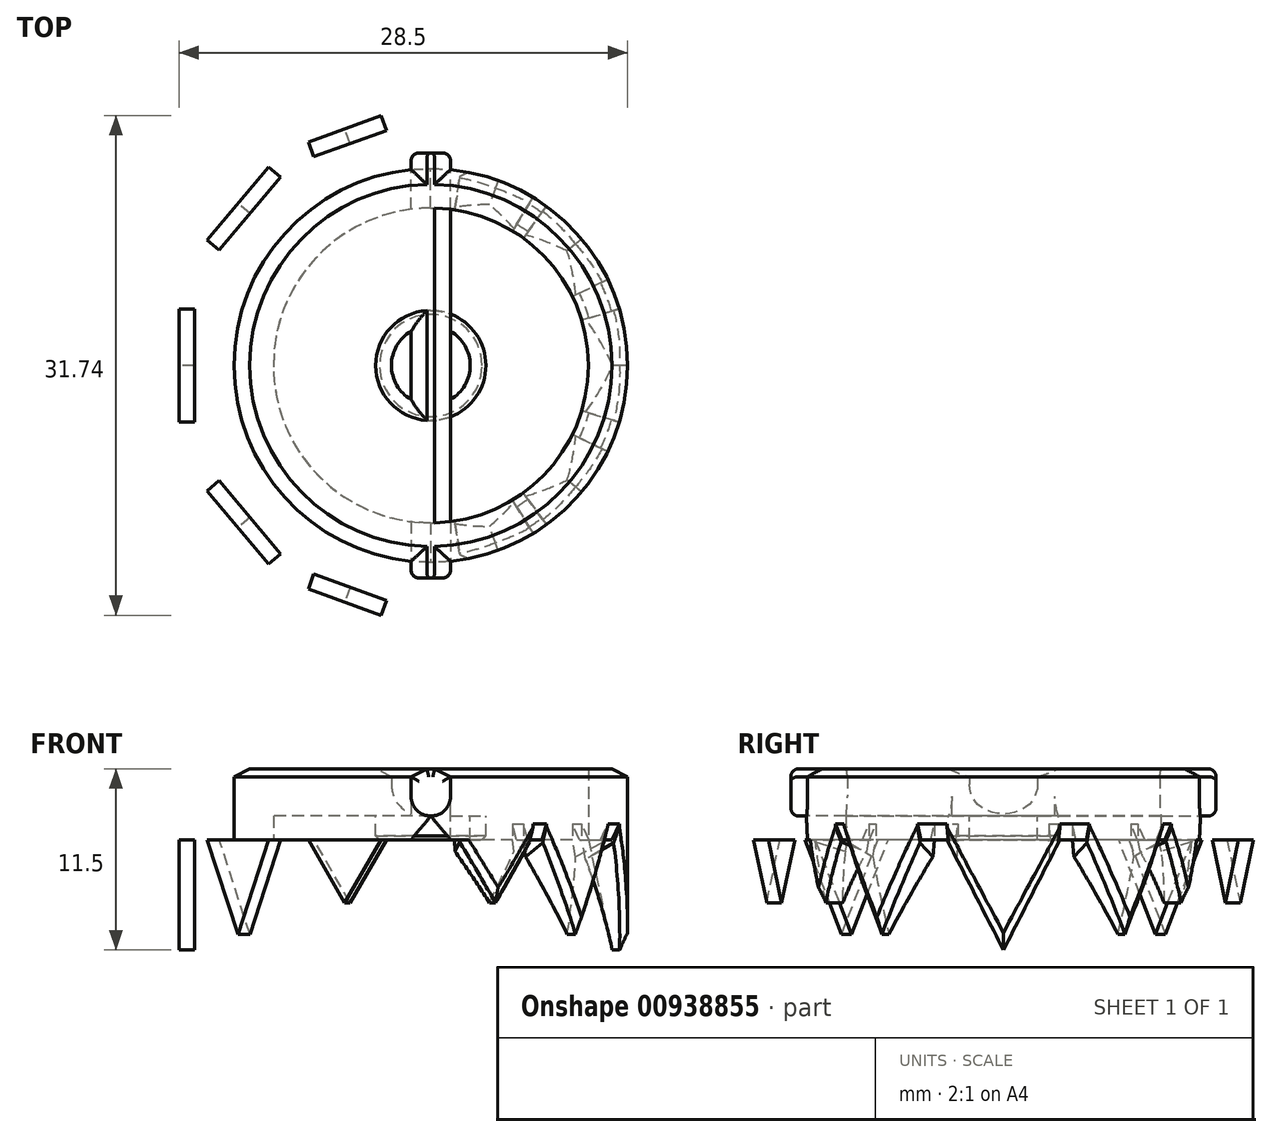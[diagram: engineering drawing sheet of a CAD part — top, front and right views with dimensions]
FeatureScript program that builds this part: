
annotation { "Feature Type Name" : "Feature", "Feature Type Description" : "" }
export const myFeature = defineFeature(function(context is Context, id is Id, definition is map)
    precondition{}
    {
        {
            var Q0;
            Q0=qCreatedBy(makeId("Top.planeOp"),FACE);
            var sketch = newSketch(context, id + "F0", { "sketchPlane" : qUnion([Q0])});
            skCircle(sketch, "E0", {"center": v(0, 0) * mm, "radius": 12.5 * mm});
            skArc(sketch, "E1", {"start": v(-1.25, 9.92) * mm, "mid": v(-10, 0) * mm, "end": v(-1.25, -9.92) * mm});
            skCircle(sketch, "E2", {"center": v(0, 0) * mm, "radius": 3.5 * mm});
            skLineSegment(sketch, "E3", {"start": v(0, 0) * mm, "end": v(1.25, 0) * mm, "construction": true});
            skLineSegment(sketch, "E4", {"start": v(1.25, 3.27) * mm, "end": v(1.25, 9.92) * mm});
            skLineSegment(sketch, "E5", {"start": v(0, 0) * mm, "end": v(-1.25, 0) * mm, "construction": true});
            skLineSegment(sketch, "E6", {"start": v(-1.25, 3.27) * mm, "end": v(-1.25, 9.92) * mm});
            skLineSegment(sketch, "E7", {"start": v(-1.25, -3.27) * mm, "end": v(-1.25, -9.92) * mm});
            skLineSegment(sketch, "E8", {"start": v(1.25, -3.27) * mm, "end": v(1.25, -9.92) * mm});
            skArc(sketch, "E9.trimOffspring", {"start": v(1.25, -9.92) * mm, "mid": v(10, 0) * mm, "end": v(1.25, 9.92) * mm});
            skCircle(sketch, "E10", {"center": v(0, 0) * mm, "radius": 10 * mm});
            skCircle(sketch, "E11", {"center": v(0, 0) * mm, "radius": 2.5 * mm});
            skLineSegment(sketch, "E12", {"start": v(-1.25, -9.92) * mm, "end": v(-1.25, 9.92) * mm});
            skLineSegment(sketch, "E13", {"start": v(1.25, -9.92) * mm, "end": v(1.25, 9.92) * mm});
            skSolve(sketch);
        }
        {
            var Q0;
            Q0 = qSketchRegion(id + "F0", true);
            var Q1;
            {var subQ0=sQuery(id+"F0.wireOp",EDGE,"E4");Q1=makeQuery(id+"F0.imprint","IMPRINT",FACE,{"disambiguationData":[TD([[makeQuery(id+"F0.imprint","IMPRINT",EDGE,{"derivedFrom":subQ0}),1.0]])]});}
            var Q2;
            {var subQ0=sQuery(id+"F0.wireOp",EDGE,"E7");Q2=makeQuery(id+"F0.imprint","IMPRINT",FACE,{"disambiguationData":[TD([[makeQuery(id+"F0.imprint","IMPRINT",EDGE,{"derivedFrom":subQ0}),1.0]])]});}
            var Q3;
            Q3=makeQuery(id+"F0.imprint","IMPRINT",FACE,{"disambiguationData":[TD([[makeQuery(id+"F0.imprint","IMPRINT",EDGE,{"derivedFrom":sQuery(id+"F0.wireOp",EDGE,"E11")}),1.0]])]});
            var Q4;
            {var subQ0=sQuery(id+"F0.wireOp",EDGE,"E12");var subQ1=sQuery(id+"F0.wireOp",EDGE,"E2");var subQ2=makeQuery(id+"F0.imprint","INTERSECT",VERTEX,{"disambiguationData":[OD(1.0)],"derivedFrom":[subQ1,subQ0]});Q4=makeQuery(id+"F0.imprint","IMPRINT",FACE,{"disambiguationData":[TD([[makeQuery(id+"F0.imprint","IMPRINT",EDGE,{"disambiguationData":[TD([[subQ2,-1.0]])],"derivedFrom":subQ1}),-1.0]])]});}
            var Q5;
            {var subQ0=sQuery(id+"F0.wireOp",EDGE,"E12");var subQ1=sQuery(id+"F0.wireOp",EDGE,"E2");var subQ2=makeQuery(id+"F0.imprint","INTERSECT",VERTEX,{"disambiguationData":[OD(1.0)],"derivedFrom":[subQ1,subQ0]});Q5=makeQuery(id+"F0.imprint","IMPRINT",FACE,{"disambiguationData":[TD([[makeQuery(id+"F0.imprint","IMPRINT",EDGE,{"disambiguationData":[TD([[subQ2,-1.0]])],"derivedFrom":subQ1}),1.0]])]});}
            var Q6;
            {var subQ0=sQuery(id+"F0.wireOp",EDGE,"E12");var subQ1=sQuery(id+"F0.wireOp",EDGE,"E11");var subQ2=makeQuery(id+"F0.imprint","INTERSECT",VERTEX,{"disambiguationData":[OD(0.0)],"derivedFrom":[subQ1,subQ0]});Q6=makeQuery(id+"F0.imprint","IMPRINT",FACE,{"disambiguationData":[TD([[makeQuery(id+"F0.imprint","IMPRINT",EDGE,{"disambiguationData":[TD([[subQ2,-1.0]])],"derivedFrom":subQ1}),1.0]])]});}
            var Q7;
            {var subQ0=sQuery(id+"F0.wireOp",EDGE,"E13");var subQ1=sQuery(id+"F0.wireOp",EDGE,"E11");var subQ2=makeQuery(id+"F0.imprint","INTERSECT",VERTEX,{"disambiguationData":[OD(0.0)],"derivedFrom":[subQ1,subQ0]});Q7=makeQuery(id+"F0.imprint","IMPRINT",FACE,{"disambiguationData":[TD([[makeQuery(id+"F0.imprint","IMPRINT",EDGE,{"disambiguationData":[TD([[subQ2,1.0]])],"derivedFrom":subQ1}),1.0]])]});}
            var Q8;
            {var subQ0=sQuery(id+"F0.wireOp",EDGE,"E12");var subQ1=sQuery(id+"F0.wireOp",EDGE,"E2");var subQ2=makeQuery(id+"F0.imprint","INTERSECT",VERTEX,{"disambiguationData":[OD(0.0)],"derivedFrom":[subQ1,subQ0]});Q8=makeQuery(id+"F0.imprint","IMPRINT",FACE,{"disambiguationData":[TD([[makeQuery(id+"F0.imprint","IMPRINT",EDGE,{"disambiguationData":[TD([[subQ2,1.0]])],"derivedFrom":subQ1}),1.0]])]});}
            var Q9;
            {var subQ0=sQuery(id+"F0.wireOp",EDGE,"E12");var subQ1=sQuery(id+"F0.wireOp",EDGE,"E2");var subQ2=makeQuery(id+"F0.imprint","INTERSECT",VERTEX,{"disambiguationData":[OD(0.0)],"derivedFrom":[subQ1,subQ0]});Q9=makeQuery(id+"F0.imprint","IMPRINT",FACE,{"disambiguationData":[TD([[makeQuery(id+"F0.imprint","IMPRINT",EDGE,{"disambiguationData":[TD([[subQ2,1.0]])],"derivedFrom":subQ1}),-1.0]])]});}
            extrude(context, id + "F1", {"entities" : qUnion([Q0, Q1, Q2, Q3, Q4, Q5, Q6, Q7, Q8, Q9]), "depth" : 3 * mm, "offsetDistance" : 25 * mm});
        }
        {
            var Q0;
            Q0=makeQuery(id+"F0.imprint","IMPRINT",FACE,{"disambiguationData":[TD([[makeQuery(id+"F0.imprint","IMPRINT",EDGE,{"derivedFrom":sQuery(id+"F0.wireOp",EDGE,"E0")}),1.0]])]});
            var Q1;
            {var subQ0=sQuery(id+"F0.wireOp",EDGE,"E12");var subQ1=sQuery(id+"F0.wireOp",EDGE,"E2");var subQ2=makeQuery(id+"F0.imprint","INTERSECT",VERTEX,{"disambiguationData":[OD(0.0)],"derivedFrom":[subQ1,subQ0]});Q1=makeQuery(id+"F0.imprint","IMPRINT",FACE,{"disambiguationData":[TD([[makeQuery(id+"F0.imprint","IMPRINT",EDGE,{"disambiguationData":[TD([[subQ2,-1.0]])],"derivedFrom":subQ1}),1.0]])]});}
            var Q2;
            {var subQ0=sQuery(id+"F0.wireOp",EDGE,"E12");var subQ1=sQuery(id+"F0.wireOp",EDGE,"E11");var subQ2=makeQuery(id+"F0.imprint","INTERSECT",VERTEX,{"disambiguationData":[OD(0.0)],"derivedFrom":[subQ1,subQ0]});Q2=makeQuery(id+"F0.imprint","IMPRINT",FACE,{"disambiguationData":[TD([[makeQuery(id+"F0.imprint","IMPRINT",EDGE,{"disambiguationData":[TD([[subQ2,-1.0]])],"derivedFrom":subQ1}),1.0]])]});}
            var Q3;
            {var subQ0=sQuery(id+"F0.wireOp",EDGE,"E12");var subQ1=sQuery(id+"F0.wireOp",EDGE,"E2");var subQ2=makeQuery(id+"F0.imprint","INTERSECT",VERTEX,{"disambiguationData":[OD(1.0)],"derivedFrom":[subQ1,subQ0]});Q3=makeQuery(id+"F0.imprint","IMPRINT",FACE,{"disambiguationData":[TD([[makeQuery(id+"F0.imprint","IMPRINT",EDGE,{"disambiguationData":[TD([[subQ2,-1.0]])],"derivedFrom":subQ1}),1.0]])]});}
            var Q4;
            {var subQ0=sQuery(id+"F0.wireOp",EDGE,"E13");var subQ1=sQuery(id+"F0.wireOp",EDGE,"E2");var subQ2=makeQuery(id+"F0.imprint","INTERSECT",VERTEX,{"disambiguationData":[OD(0.0)],"derivedFrom":[subQ1,subQ0]});Q4=makeQuery(id+"F0.imprint","IMPRINT",FACE,{"disambiguationData":[TD([[makeQuery(id+"F0.imprint","IMPRINT",EDGE,{"disambiguationData":[TD([[subQ2,1.0]])],"derivedFrom":subQ1}),1.0]])]});}
            var Q5;
            {var subQ0=sQuery(id+"F0.wireOp",EDGE,"E13");var subQ1=sQuery(id+"F0.wireOp",EDGE,"E11");var subQ2=makeQuery(id+"F0.imprint","INTERSECT",VERTEX,{"disambiguationData":[OD(0.0)],"derivedFrom":[subQ1,subQ0]});Q5=makeQuery(id+"F0.imprint","IMPRINT",FACE,{"disambiguationData":[TD([[makeQuery(id+"F0.imprint","IMPRINT",EDGE,{"disambiguationData":[TD([[subQ2,1.0]])],"derivedFrom":subQ1}),1.0]])]});}
            var Q6;
            {var subQ0=sQuery(id+"F0.wireOp",EDGE,"E12");var subQ1=sQuery(id+"F0.wireOp",EDGE,"E11");var subQ2=makeQuery(id+"F0.imprint","INTERSECT",VERTEX,{"disambiguationData":[OD(0.0)],"derivedFrom":[subQ1,subQ0]});Q6=makeQuery(id+"F0.imprint","IMPRINT",FACE,{"disambiguationData":[TD([[makeQuery(id+"F0.imprint","IMPRINT",EDGE,{"disambiguationData":[TD([[subQ2,1.0]])],"derivedFrom":subQ1}),1.0]])]});}
            var Q7;
            {var subQ0=sQuery(id+"F0.wireOp",EDGE,"E12");var subQ1=sQuery(id+"F0.wireOp",EDGE,"E2");var subQ2=makeQuery(id+"F0.imprint","INTERSECT",VERTEX,{"disambiguationData":[OD(0.0)],"derivedFrom":[subQ1,subQ0]});Q7=makeQuery(id+"F0.imprint","IMPRINT",FACE,{"disambiguationData":[TD([[makeQuery(id+"F0.imprint","IMPRINT",EDGE,{"disambiguationData":[TD([[subQ2,1.0]])],"derivedFrom":subQ1}),1.0]])]});}
            extrude(context, id + "F2", {"entities" : qUnion([Q0, Q1, Q2, Q3, Q4, Q5, Q6, Q7]), "operationType" : NewBodyOperationType.ADD, "oppositeDirection" : true, "depth" : 1.5 * mm, "offsetDistance" : 25 * mm});
        }
        {
            var Q0;
            Q0=makeQuery(id+"F2.opExtrude","CAP_FACE",FACE,{"disambiguationData":[OSD([sQuery(id+"F0.wireOp",EDGE,"E2")])],"isStart":false});
            var sketch = newSketch(context, id + "F3", { "sketchPlane" : qUnion([Q0])});
            skCircle(sketch, "E14", {"center": v(0, 0) * mm, "radius": 12.5 * mm});
            skLineSegment(sketch, "E15", {"start": v(0, 0) * mm, "end": v(0, 12.5) * mm, "construction": true});
            skLineSegment(sketch, "E16", {"start": v(0, 0) * mm, "end": v(0, -12.5) * mm, "construction": true});
            skLineSegment(sketch, "E17", {"start": v(0, 0) * mm, "end": v(-4.28, 11.75) * mm, "construction": true});
            skLineSegment(sketch, "E18", {"start": v(0, 0) * mm, "end": v(-9.58, 8.03) * mm, "construction": true});
            skLineSegment(sketch, "E19", {"start": v(0, 0) * mm, "end": v(-12.5, 0) * mm, "construction": true});
            skLineSegment(sketch, "E20", {"start": v(0, 0) * mm, "end": v(-9.58, -8.03) * mm, "construction": true});
            skLineSegment(sketch, "E21", {"start": v(0, 0) * mm, "end": v(-4.28, -11.75) * mm, "construction": true});
            skCircle(sketch, "E22", {"center": v(0, 0) * mm, "radius": 10 * mm});
            skLineSegment(sketch, "E23", {"start": v(-3.42, 9.4) * mm, "end": v(-1.54, 10.08) * mm, "construction": true});
            skLineSegment(sketch, "E24", {"start": v(-3.42, 9.4) * mm, "end": v(-5.3, 8.71) * mm, "construction": true});
            skLineSegment(sketch, "E25", {"start": v(-7.66, 6.43) * mm, "end": v(-6.05, 8.34) * mm, "construction": true});
            skLineSegment(sketch, "E26", {"start": v(-7.66, 6.43) * mm, "end": v(-9.27, 4.51) * mm, "construction": true});
            skLineSegment(sketch, "E27", {"start": v(-10, 0) * mm, "end": v(-10, 3) * mm, "construction": true});
            skLineSegment(sketch, "E28", {"start": v(-10, 0) * mm, "end": v(-10, -3) * mm, "construction": true});
            skLineSegment(sketch, "E29", {"start": v(-7.66, -6.43) * mm, "end": v(-9.27, -4.51) * mm, "construction": true});
            skLineSegment(sketch, "E30", {"start": v(-7.66, -6.43) * mm, "end": v(-6.05, -8.34) * mm, "construction": true});
            skLineSegment(sketch, "E31", {"start": v(-3.42, -9.4) * mm, "end": v(-5.3, -8.71) * mm, "construction": true});
            skLineSegment(sketch, "E32", {"start": v(-3.42, -9.4) * mm, "end": v(-1.54, -10.08) * mm, "construction": true});
            skLineSegment(sketch, "E33", {"start": v(-1.51, 9.89) * mm, "end": v(-1.54, 10.08) * mm});
            skLineSegment(sketch, "E34", {"start": v(-1.54, 10.08) * mm, "end": v(-1.89, 12.36) * mm});
            skLineSegment(sketch, "E35", {"start": v(-5.2, 8.54) * mm, "end": v(-5.3, 8.71) * mm});
            skLineSegment(sketch, "E36", {"start": v(-5.3, 8.71) * mm, "end": v(-6.5, 10.68) * mm});
            skLineSegment(sketch, "E37", {"start": v(-5.87, 8.1) * mm, "end": v(-6.05, 8.34) * mm});
            skLineSegment(sketch, "E38", {"start": v(-6.05, 8.34) * mm, "end": v(-7.34, 10.12) * mm});
            skLineSegment(sketch, "E39", {"start": v(-9, 4.38) * mm, "end": v(-9.27, 4.51) * mm});
            skLineSegment(sketch, "E40", {"start": v(-9.27, 4.51) * mm, "end": v(-11.24, 5.47) * mm});
            skLineSegment(sketch, "E41", {"start": v(-9.58, 2.87) * mm, "end": v(-10, 3) * mm});
            skLineSegment(sketch, "E42", {"start": v(-10, 3) * mm, "end": v(-11.97, 3.6) * mm});
            skLineSegment(sketch, "E43", {"start": v(-9.58, -2.87) * mm, "end": v(-10, -3) * mm});
            skLineSegment(sketch, "E44", {"start": v(-10, -3) * mm, "end": v(-11.97, -3.6) * mm});
            skLineSegment(sketch, "E45", {"start": v(-9, -4.38) * mm, "end": v(-9.27, -4.51) * mm});
            skLineSegment(sketch, "E46", {"start": v(-9.27, -4.51) * mm, "end": v(-11.24, -5.47) * mm});
            skLineSegment(sketch, "E47", {"start": v(-5.87, -8.1) * mm, "end": v(-6.05, -8.34) * mm});
            skLineSegment(sketch, "E48", {"start": v(-6.05, -8.34) * mm, "end": v(-7.34, -10.12) * mm});
            skLineSegment(sketch, "E49", {"start": v(-5.2, -8.54) * mm, "end": v(-5.3, -8.71) * mm});
            skLineSegment(sketch, "E50", {"start": v(-5.3, -8.71) * mm, "end": v(-6.5, -10.68) * mm});
            skLineSegment(sketch, "E51", {"start": v(-1.51, -9.89) * mm, "end": v(-1.54, -10.08) * mm});
            skLineSegment(sketch, "E52", {"start": v(-1.54, -10.08) * mm, "end": v(-1.89, -12.36) * mm});
            skLineSegment(sketch, "E53", {"start": v(-1.89, 12.36) * mm, "end": v(-1.51, 9.89) * mm});
            skLineSegment(sketch, "E54", {"start": v(-6.5, 10.68) * mm, "end": v(-5.2, 8.54) * mm});
            skLineSegment(sketch, "E55", {"start": v(-7.34, 10.12) * mm, "end": v(-5.87, 8.1) * mm});
            skLineSegment(sketch, "E56", {"start": v(-11.24, 5.47) * mm, "end": v(-9, 4.38) * mm});
            skLineSegment(sketch, "E57", {"start": v(-11.97, 3.6) * mm, "end": v(-9.58, 2.87) * mm});
            skLineSegment(sketch, "E58", {"start": v(-11.97, -3.6) * mm, "end": v(-9.58, -2.87) * mm});
            skLineSegment(sketch, "E59", {"start": v(-11.24, -5.47) * mm, "end": v(-9, -4.38) * mm});
            skLineSegment(sketch, "E60", {"start": v(-7.34, -10.12) * mm, "end": v(-5.87, -8.1) * mm});
            skLineSegment(sketch, "E61", {"start": v(-6.5, -10.68) * mm, "end": v(-5.2, -8.54) * mm});
            skLineSegment(sketch, "E62", {"start": v(-1.89, -12.36) * mm, "end": v(-1.51, -9.89) * mm});
            skLineSegment(sketch, "E63.trimOffspring", {"start": v(1.51, -9.89) * mm, "end": v(1.89, -12.36) * mm});
            skLineSegment(sketch, "E64.trimOffspring", {"start": v(5.2, -8.54) * mm, "end": v(6.5, -10.68) * mm});
            skLineSegment(sketch, "E65.trimOffspring", {"start": v(5.87, -8.1) * mm, "end": v(7.34, -10.12) * mm});
            skLineSegment(sketch, "E66.trimOffspring", {"start": v(9, -4.38) * mm, "end": v(11.24, -5.47) * mm});
            skLineSegment(sketch, "E67.trimOffspring", {"start": v(9.58, -2.87) * mm, "end": v(11.97, -3.6) * mm});
            skLineSegment(sketch, "E68.trimOffspring", {"start": v(9.58, 2.87) * mm, "end": v(11.97, 3.6) * mm});
            skLineSegment(sketch, "E69.trimOffspring", {"start": v(9, 4.38) * mm, "end": v(11.24, 5.47) * mm});
            skLineSegment(sketch, "E70.trimOffspring", {"start": v(5.87, 8.1) * mm, "end": v(7.34, 10.12) * mm});
            skLineSegment(sketch, "E71.trimOffspring", {"start": v(5.2, 8.54) * mm, "end": v(6.5, 10.68) * mm});
            skLineSegment(sketch, "E72.trimOffspring", {"start": v(1.51, 9.89) * mm, "end": v(1.89, 12.36) * mm});
            skLineSegment(sketch, "E73", {"start": v(-5.3, -8.71) * mm, "end": v(-7, -13.41) * mm, "construction": true});
            skLineSegment(sketch, "E74", {"start": v(-1.54, -10.08) * mm, "end": v(-3.25, -14.78) * mm, "construction": true});
            skLineSegment(sketch, "E75", {"start": v(-3.25, -14.78) * mm, "end": v(-7, -13.41) * mm, "construction": true});
            skLineSegment(sketch, "E76", {"start": v(-7, -13.41) * mm, "end": v(-8.42, -12.9) * mm, "construction": true});
            skLineSegment(sketch, "E77", {"start": v(-3.25, -14.78) * mm, "end": v(-1.84, -15.3) * mm, "construction": true});
            skLineSegment(sketch, "E78", {"start": v(-6.5, -10.68) * mm, "end": v(-7.43, -13.26) * mm, "construction": true});
            skLineSegment(sketch, "E79", {"start": v(-1.89, -12.36) * mm, "end": v(-2.83, -14.93) * mm, "construction": true});
            skLineSegment(sketch, "E80", {"start": v(-7.43, -13.26) * mm, "end": v(-7.78, -14.2) * mm});
            skLineSegment(sketch, "E81", {"start": v(-2.83, -14.93) * mm, "end": v(-3.17, -15.87) * mm});
            skLineSegment(sketch, "E82", {"start": v(-3.17, -15.87) * mm, "end": v(-7.78, -14.2) * mm});
            skLineSegment(sketch, "E83", {"start": v(-7.43, -13.26) * mm, "end": v(-2.83, -14.93) * mm});
            skLineSegment(sketch, "E84", {"start": v(-9.27, -4.51) * mm, "end": v(-13.1, -7.73) * mm, "construction": true});
            skLineSegment(sketch, "E85", {"start": v(-6.05, -8.34) * mm, "end": v(-9.88, -11.56) * mm, "construction": true});
            skLineSegment(sketch, "E86", {"start": v(-9.88, -11.56) * mm, "end": v(-13.1, -7.73) * mm, "construction": true});
            skLineSegment(sketch, "E87", {"start": v(-13.1, -7.73) * mm, "end": v(-14.06, -6.58) * mm, "construction": true});
            skLineSegment(sketch, "E88", {"start": v(-9.88, -11.56) * mm, "end": v(-8.92, -12.7) * mm, "construction": true});
            skLineSegment(sketch, "E89", {"start": v(-11.24, -5.47) * mm, "end": v(-13.44, -7.32) * mm, "construction": true});
            skLineSegment(sketch, "E90", {"start": v(-7.34, -10.12) * mm, "end": v(-9.54, -11.96) * mm, "construction": true});
            skLineSegment(sketch, "E91", {"start": v(-13.44, -7.32) * mm, "end": v(-9.54, -11.96) * mm});
            skLineSegment(sketch, "E92", {"start": v(-9.54, -11.96) * mm, "end": v(-10.3, -12.6) * mm});
            skLineSegment(sketch, "E93", {"start": v(-13.44, -7.32) * mm, "end": v(-14.2, -7.96) * mm});
            skLineSegment(sketch, "E94", {"start": v(-14.2, -7.96) * mm, "end": v(-10.3, -12.6) * mm});
            skLineSegment(sketch, "E95", {"start": v(-10, 3) * mm, "end": v(-15, 3) * mm, "construction": true});
            skLineSegment(sketch, "E96", {"start": v(-10, -3) * mm, "end": v(-15, -3) * mm, "construction": true});
            skLineSegment(sketch, "E97", {"start": v(-15, -3) * mm, "end": v(-15, 3) * mm, "construction": true});
            skLineSegment(sketch, "E98", {"start": v(-15, 3) * mm, "end": v(-15, 4) * mm, "construction": true});
            skLineSegment(sketch, "E99", {"start": v(-15, -3) * mm, "end": v(-15, -4) * mm, "construction": true});
            skLineSegment(sketch, "E100", {"start": v(-11.97, -3.6) * mm, "end": v(-15, -3.6) * mm, "construction": true});
            skLineSegment(sketch, "E101", {"start": v(-11.97, 3.6) * mm, "end": v(-15, 3.6) * mm, "construction": true});
            skLineSegment(sketch, "E102", {"start": v(-15, 3.6) * mm, "end": v(-16, 3.6) * mm});
            skLineSegment(sketch, "E103", {"start": v(-15, -3.6) * mm, "end": v(-16, -3.6) * mm});
            skLineSegment(sketch, "E104", {"start": v(-16, -3.6) * mm, "end": v(-16, 3.6) * mm});
            skLineSegment(sketch, "E105", {"start": v(-15, 3.6) * mm, "end": v(-15, -3.6) * mm});
            skLineSegment(sketch, "E106", {"start": v(-6.05, 8.34) * mm, "end": v(-9.88, 11.56) * mm, "construction": true});
            skLineSegment(sketch, "E107", {"start": v(-9.27, 4.51) * mm, "end": v(-13.1, 7.73) * mm, "construction": true});
            skLineSegment(sketch, "E108", {"start": v(-13.1, 7.73) * mm, "end": v(-9.88, 11.56) * mm, "construction": true});
            skLineSegment(sketch, "E109", {"start": v(-9.88, 11.56) * mm, "end": v(-9.24, 12.32) * mm, "construction": true});
            skLineSegment(sketch, "E110", {"start": v(-13.1, 7.73) * mm, "end": v(-13.74, 6.96) * mm, "construction": true});
            skLineSegment(sketch, "E111", {"start": v(-7.34, 10.12) * mm, "end": v(-9.54, 11.96) * mm, "construction": true});
            skLineSegment(sketch, "E112", {"start": v(-11.24, 5.47) * mm, "end": v(-13.44, 7.32) * mm, "construction": true});
            skLineSegment(sketch, "E113", {"start": v(-13.44, 7.32) * mm, "end": v(-14.2, 7.96) * mm});
            skLineSegment(sketch, "E114", {"start": v(-9.54, 11.96) * mm, "end": v(-10.3, 12.6) * mm});
            skLineSegment(sketch, "E115", {"start": v(-10.3, 12.6) * mm, "end": v(-14.2, 7.96) * mm});
            skLineSegment(sketch, "E116", {"start": v(-13.44, 7.32) * mm, "end": v(-9.54, 11.96) * mm});
            skLineSegment(sketch, "E117", {"start": v(-5.3, 8.71) * mm, "end": v(-7, 13.41) * mm, "construction": true});
            skLineSegment(sketch, "E118", {"start": v(-1.54, 10.08) * mm, "end": v(-3.25, 14.78) * mm, "construction": true});
            skLineSegment(sketch, "E119", {"start": v(-3.25, 14.78) * mm, "end": v(-7, 13.41) * mm, "construction": true});
            skLineSegment(sketch, "E120", {"start": v(-7, 13.41) * mm, "end": v(-7.95, 13.07) * mm, "construction": true});
            skLineSegment(sketch, "E121", {"start": v(-3.25, 14.78) * mm, "end": v(-2.31, 15.12) * mm, "construction": true});
            skLineSegment(sketch, "E122", {"start": v(-1.89, 12.36) * mm, "end": v(-2.83, 14.93) * mm, "construction": true});
            skLineSegment(sketch, "E123", {"start": v(-6.5, 10.68) * mm, "end": v(-7.43, 13.26) * mm, "construction": true});
            skLineSegment(sketch, "E124", {"start": v(-7.43, 13.26) * mm, "end": v(-7.78, 14.2) * mm});
            skLineSegment(sketch, "E125", {"start": v(-2.83, 14.93) * mm, "end": v(-3.17, 15.87) * mm});
            skLineSegment(sketch, "E126", {"start": v(-3.17, 15.87) * mm, "end": v(-7.78, 14.2) * mm});
            skLineSegment(sketch, "E127", {"start": v(-7.43, 13.26) * mm, "end": v(-2.83, 14.93) * mm});
            skSolve(sketch);
        }
        {
            var Q0;
            {var subQ0=sQuery(id+"F3.wireOp",EDGE,"E53");Q0=makeQuery(id+"F3.imprint","IMPRINT",FACE,{"disambiguationData":[TD([[makeQuery(id+"F3.imprint","IMPRINT",EDGE,{"derivedFrom":subQ0}),-1.0]])]});}
            var Q1;
            {var subQ0=sQuery(id+"F3.wireOp",EDGE,"E71.trimOffspring");Q1=makeQuery(id+"F3.imprint","IMPRINT",FACE,{"disambiguationData":[TD([[makeQuery(id+"F3.imprint","IMPRINT",EDGE,{"derivedFrom":subQ0}),1.0]])]});}
            var Q2;
            {var subQ0=sQuery(id+"F3.wireOp",EDGE,"E63.trimOffspring");Q2=makeQuery(id+"F3.imprint","IMPRINT",FACE,{"disambiguationData":[TD([[makeQuery(id+"F3.imprint","IMPRINT",EDGE,{"derivedFrom":subQ0}),1.0]])]});}
            var Q3;
            {var subQ0=sQuery(id+"F3.wireOp",EDGE,"E61");Q3=makeQuery(id+"F3.imprint","IMPRINT",FACE,{"disambiguationData":[TD([[makeQuery(id+"F3.imprint","IMPRINT",EDGE,{"derivedFrom":subQ0}),-1.0]])]});}
            extrude(context, id + "F4", {"entities" : qUnion([Q0, Q1, Q2, Q3]), "operationType" : NewBodyOperationType.ADD, "depth" : 4 * mm, "offsetDistance" : 25 * mm});
        }
        {
            var Q0;
            {var subQ0=sQuery(id+"F3.wireOp",EDGE,"E55");Q0=makeQuery(id+"F3.imprint","IMPRINT",FACE,{"disambiguationData":[TD([[makeQuery(id+"F3.imprint","IMPRINT",EDGE,{"derivedFrom":subQ0}),-1.0]])]});}
            var Q1;
            {var subQ0=sQuery(id+"F3.wireOp",EDGE,"E69.trimOffspring");Q1=makeQuery(id+"F3.imprint","IMPRINT",FACE,{"disambiguationData":[TD([[makeQuery(id+"F3.imprint","IMPRINT",EDGE,{"derivedFrom":subQ0}),1.0]])]});}
            var Q2;
            {var subQ0=sQuery(id+"F3.wireOp",EDGE,"E65.trimOffspring");Q2=makeQuery(id+"F3.imprint","IMPRINT",FACE,{"disambiguationData":[TD([[makeQuery(id+"F3.imprint","IMPRINT",EDGE,{"derivedFrom":subQ0}),1.0]])]});}
            var Q3;
            {var subQ0=sQuery(id+"F3.wireOp",EDGE,"E59");Q3=makeQuery(id+"F3.imprint","IMPRINT",FACE,{"disambiguationData":[TD([[makeQuery(id+"F3.imprint","IMPRINT",EDGE,{"derivedFrom":subQ0}),-1.0]])]});}
            extrude(context, id + "F5", {"entities" : qUnion([Q0, Q1, Q2, Q3]), "operationType" : NewBodyOperationType.ADD, "depth" : 6 * mm, "offsetDistance" : 25 * mm});
        }
        {
            var Q0;
            {var subQ0=sQuery(id+"F3.wireOp",EDGE,"E57");Q0=makeQuery(id+"F3.imprint","IMPRINT",FACE,{"disambiguationData":[TD([[makeQuery(id+"F3.imprint","IMPRINT",EDGE,{"derivedFrom":subQ0}),-1.0]])]});}
            var Q1;
            {var subQ0=sQuery(id+"F3.wireOp",EDGE,"E67.trimOffspring");Q1=makeQuery(id+"F3.imprint","IMPRINT",FACE,{"disambiguationData":[TD([[makeQuery(id+"F3.imprint","IMPRINT",EDGE,{"derivedFrom":subQ0}),1.0]])]});}
            extrude(context, id + "F6", {"entities" : qUnion([Q0, Q1]), "operationType" : NewBodyOperationType.ADD, "depth" : 7 * mm, "offsetDistance" : 25 * mm});
        }
        {
            var Q0;
            Q0=makeQuery(id+"F3.imprint","IMPRINT",FACE,{"disambiguationData":[TD([[makeQuery(id+"F3.imprint","IMPRINT",EDGE,{"derivedFrom":sQuery(id+"F3.wireOp",EDGE,"E80")}),1.0]])]});
            extrude(context, id + "F7", {"entities" : qUnion([Q0]), "depth" : 4 * mm, "offsetDistance" : 25 * mm});
        }
        {
            var Q0;
            Q0=makeQuery(id+"F7.opExtrude","SWEPT_FACE",FACE,{"disambiguationData":[OSD([sQuery(id+"F3.wireOp",EDGE,"E82")])]});
            var sketch = newSketch(context, id + "F8", { "sketchPlane" : qUnion([Q0])});
            skLineSegment(sketch, "E128", {"start": v(2.45, -1.5) * mm, "end": v(0, -5.5) * mm});
            skLineSegment(sketch, "E129", {"start": v(0, -5.5) * mm, "end": v(-2.45, -1.5) * mm});
            skSolve(sketch);
        }
        {
            var Q0;
            {var subQ0=sQuery(id+"F8.wireOp",EDGE,"E128");Q0=makeQuery(id+"F8.imprint","IMPRINT",FACE,{"disambiguationData":[TD([[makeQuery(id+"F8.imprint","IMPRINT",EDGE,{"derivedFrom":subQ0}),1.0]])]});}
            var Q1;
            {var subQ0=sQuery(id+"F8.wireOp",EDGE,"E129");Q1=makeQuery(id+"F8.imprint","IMPRINT",FACE,{"disambiguationData":[TD([[makeQuery(id+"F8.imprint","IMPRINT",EDGE,{"derivedFrom":subQ0}),1.0]])]});}
            extrude(context, id + "F9", {"entities" : qUnion([Q0, Q1]), "operationType" : NewBodyOperationType.REMOVE, "oppositeDirection" : true, "depth" : 40 * mm, "offsetDistance" : 25 * mm});
        }
        {
            var Q0;
            Q0=makeQuery(id+"F3.imprint","IMPRINT",FACE,{"disambiguationData":[TD([[makeQuery(id+"F3.imprint","IMPRINT",EDGE,{"derivedFrom":sQuery(id+"F3.wireOp",EDGE,"E91")}),-1.0]])]});
            extrude(context, id + "F10", {"entities" : qUnion([Q0]), "depth" : 6 * mm, "offsetDistance" : 25 * mm});
        }
        {
            var Q0;
            Q0=makeQuery(id+"F10.opExtrude","SWEPT_FACE",FACE,{"disambiguationData":[OSD([sQuery(id+"F3.wireOp",EDGE,"E94")])]});
            var sketch = newSketch(context, id + "F11", { "sketchPlane" : qUnion([Q0])});
            skLineSegment(sketch, "E130", {"start": v(3.03, -1.5) * mm, "end": v(0, -7.5) * mm});
            skLineSegment(sketch, "E131", {"start": v(0, -7.5) * mm, "end": v(-3.03, -1.5) * mm});
            skSolve(sketch);
        }
        {
            var Q0;
            {var subQ0=sQuery(id+"F11.wireOp",EDGE,"E130");Q0=makeQuery(id+"F11.imprint","IMPRINT",FACE,{"disambiguationData":[TD([[makeQuery(id+"F11.imprint","IMPRINT",EDGE,{"derivedFrom":subQ0}),1.0]])]});}
            var Q1;
            {var subQ0=sQuery(id+"F11.wireOp",EDGE,"E131");Q1=makeQuery(id+"F11.imprint","IMPRINT",FACE,{"disambiguationData":[TD([[makeQuery(id+"F11.imprint","IMPRINT",EDGE,{"derivedFrom":subQ0}),1.0]])]});}
            extrude(context, id + "F12", {"entities" : qUnion([Q0, Q1]), "operationType" : NewBodyOperationType.REMOVE, "oppositeDirection" : true, "depth" : 40 * mm, "offsetDistance" : 25 * mm});
        }
        {
            var Q0;
            Q0=makeQuery(id+"F3.imprint","IMPRINT",FACE,{"disambiguationData":[TD([[makeQuery(id+"F3.imprint","IMPRINT",EDGE,{"derivedFrom":sQuery(id+"F3.wireOp",EDGE,"E102")}),1.0]])]});
            extrude(context, id + "F13", {"entities" : qUnion([Q0]), "depth" : 7 * mm, "offsetDistance" : 25 * mm});
        }
        {
            var Q0;
            Q0=makeQuery(id+"F13.opExtrude","SWEPT_FACE",FACE,{"disambiguationData":[OSD([sQuery(id+"F3.wireOp",EDGE,"E104")])]});
            var sketch = newSketch(context, id + "F14", { "sketchPlane" : qUnion([Q0])});
            skLineSegment(sketch, "E132", {"start": v(3.6, -1.5) * mm, "end": v(0, -8.5) * mm});
            skLineSegment(sketch, "E133", {"start": v(0, -8.5) * mm, "end": v(-3.6, -1.5) * mm});
            skSolve(sketch);
        }
        {
            var Q0;
            {var subQ0=sQuery(id+"F14.wireOp",EDGE,"E132");Q0=makeQuery(id+"F14.imprint","IMPRINT",FACE,{"disambiguationData":[TD([[makeQuery(id+"F14.imprint","IMPRINT",EDGE,{"derivedFrom":subQ0}),1.0]])]});}
            var Q1;
            {var subQ0=sQuery(id+"F14.wireOp",EDGE,"E133");Q1=makeQuery(id+"F14.imprint","IMPRINT",FACE,{"disambiguationData":[TD([[makeQuery(id+"F14.imprint","IMPRINT",EDGE,{"derivedFrom":subQ0}),1.0]])]});}
            extrude(context, id + "F15", {"entities" : qUnion([Q0, Q1]), "operationType" : NewBodyOperationType.REMOVE, "oppositeDirection" : true, "depth" : 40 * mm, "offsetDistance" : 25 * mm});
        }
        {
            var Q0;
            Q0=makeQuery(id+"F3.imprint","IMPRINT",FACE,{"disambiguationData":[TD([[makeQuery(id+"F3.imprint","IMPRINT",EDGE,{"derivedFrom":sQuery(id+"F3.wireOp",EDGE,"E113")}),-1.0]])]});
            extrude(context, id + "F16", {"entities" : qUnion([Q0]), "depth" : 6 * mm, "offsetDistance" : 25 * mm});
        }
        {
            var Q0;
            Q0=makeQuery(id+"F3.imprint","IMPRINT",FACE,{"disambiguationData":[TD([[makeQuery(id+"F3.imprint","IMPRINT",EDGE,{"derivedFrom":sQuery(id+"F3.wireOp",EDGE,"E124")}),-1.0]])]});
            extrude(context, id + "F17", {"entities" : qUnion([Q0]), "depth" : 4 * mm, "offsetDistance" : 25 * mm});
        }
        {
            var Q0;
            Q0=makeQuery(id+"F16.opExtrude","SWEPT_FACE",FACE,{"disambiguationData":[OSD([sQuery(id+"F3.wireOp",EDGE,"E115")])]});
            var sketch = newSketch(context, id + "F18", { "sketchPlane" : qUnion([Q0])});
            skLineSegment(sketch, "E134", {"start": v(3.03, -1.5) * mm, "end": v(0, -7.5) * mm});
            skLineSegment(sketch, "E135", {"start": v(0, -7.5) * mm, "end": v(-3.03, -1.5) * mm});
            skSolve(sketch);
        }
        {
            var Q0;
            Q0=makeQuery(id+"F17.opExtrude","SWEPT_FACE",FACE,{"disambiguationData":[OSD([sQuery(id+"F3.wireOp",EDGE,"E126")])]});
            var sketch = newSketch(context, id + "F19", { "sketchPlane" : qUnion([Q0])});
            skLineSegment(sketch, "E136", {"start": v(2.45, -1.5) * mm, "end": v(0, -5.5) * mm});
            skLineSegment(sketch, "E137", {"start": v(0, -5.5) * mm, "end": v(-2.45, -1.5) * mm});
            skSolve(sketch);
        }
        {
            var Q0;
            {var subQ0=sQuery(id+"F18.wireOp",EDGE,"E134");Q0=makeQuery(id+"F18.imprint","IMPRINT",FACE,{"disambiguationData":[TD([[makeQuery(id+"F18.imprint","IMPRINT",EDGE,{"derivedFrom":subQ0}),1.0]])]});}
            var Q1;
            {var subQ0=sQuery(id+"F18.wireOp",EDGE,"E135");Q1=makeQuery(id+"F18.imprint","IMPRINT",FACE,{"disambiguationData":[TD([[makeQuery(id+"F18.imprint","IMPRINT",EDGE,{"derivedFrom":subQ0}),1.0]])]});}
            extrude(context, id + "F20", {"entities" : qUnion([Q0, Q1]), "operationType" : NewBodyOperationType.REMOVE, "oppositeDirection" : true, "depth" : 40 * mm, "offsetDistance" : 25 * mm});
        }
        {
            var Q0;
            {var subQ0=sQuery(id+"F19.wireOp",EDGE,"E136");Q0=makeQuery(id+"F19.imprint","IMPRINT",FACE,{"disambiguationData":[TD([[makeQuery(id+"F19.imprint","IMPRINT",EDGE,{"derivedFrom":subQ0}),1.0]])]});}
            var Q1;
            {var subQ0=sQuery(id+"F19.wireOp",EDGE,"E137");Q1=makeQuery(id+"F19.imprint","IMPRINT",FACE,{"disambiguationData":[TD([[makeQuery(id+"F19.imprint","IMPRINT",EDGE,{"derivedFrom":subQ0}),1.0]])]});}
            extrude(context, id + "F21", {"entities" : qUnion([Q0, Q1]), "operationType" : NewBodyOperationType.REMOVE, "oppositeDirection" : true, "depth" : 40 * mm, "offsetDistance" : 25 * mm});
        }
        {
            var Q0;
            Q0=qCreatedBy(makeId("Front.planeOp"),FACE);
            var sketch = newSketch(context, id + "F22", { "sketchPlane" : qUnion([Q0])});
            skLineSegment(sketch, "E138", {"start": v(0, 0) * mm, "end": v(-10, 0) * mm});
            skLineSegment(sketch, "E139", {"start": v(-11.3, -8.62) * mm, "end": v(-9.25, -8.62) * mm});
            skLineSegment(sketch, "E140", {"start": v(0, 0) * mm, "end": v(0, -14.5) * mm});
            skLineSegment(sketch, "E141", {"start": v(-10, 0) * mm, "end": v(-10, -1.5) * mm});
            skLineSegment(sketch, "E142", {"start": v(-9.25, -8.62) * mm, "end": v(-10, -1.5) * mm});
            skLineSegment(sketch, "E143", {"start": v(-11.3, -8.62) * mm, "end": v(-11.55, -8.62) * mm});
            skLineSegment(sketch, "E144", {"start": v(-11.55, -8.62) * mm, "end": v(-10, -1.5) * mm});
            skSolve(sketch);
        }
        {
            var Q0;
            Q0=makeQuery(id+"F22.imprint","IMPRINT",FACE,{"disambiguationData":[TD([[makeQuery(id+"F22.imprint","IMPRINT",EDGE,{"derivedFrom":sQuery(id+"F22.wireOp",EDGE,"E139")}),1.0]])]});
            var Q1;
            Q1=sQuery(id+"F22.wireOp",EDGE,"E140");
            revolve(context, id + "F23", {"operationType" : NewBodyOperationType.REMOVE, "surfaceOperationType" : NewSurfaceOperationType.NEW, "entities" : qUnion([Q0]), "axis" : qUnion([Q1]), "revolveType" : RevolveType.FULL, "oppositeDirection" : true});
        }
        {
            var Q0;
            {var subQ0=sQuery(id+"F0.wireOp",EDGE,"E12");var subQ1=sQuery(id+"F0.wireOp",EDGE,"E11");Q0=makeQuery(id+"F1.opExtrude","CAP_EDGE",EDGE,{"disambiguationData":[OSD([subQ1]),TDD([makeQuery(id+"F0.imprint","IMPRINT",EDGE,{"disambiguationData":[TD([[makeQuery(id+"F0.imprint","INTERSECT",VERTEX,{"disambiguationData":[OD(0.0)],"derivedFrom":[subQ1,subQ0]}),-1.0]])],"derivedFrom":subQ1})])],"isStart":true});}
            var Q1;
            {var subQ0=sQuery(id+"F0.wireOp",EDGE,"E13");var subQ1=sQuery(id+"F0.wireOp",EDGE,"E11");Q1=makeQuery(id+"F1.opExtrude","CAP_EDGE",EDGE,{"disambiguationData":[OSD([subQ1]),TDD([makeQuery(id+"F0.imprint","IMPRINT",EDGE,{"disambiguationData":[TD([[makeQuery(id+"F0.imprint","INTERSECT",VERTEX,{"disambiguationData":[OD(0.0)],"derivedFrom":[subQ1,subQ0]}),1.0]])],"derivedFrom":subQ1})])],"isStart":true});}
            fillet(context, id + "F24", {"entities" : qUnion([Q0, Q1]), "radius" : 2 * mm, "tangentPropagation" : true, "allowEdgeOverflow" : false});
        }
        {
            var Q0;
            {var subQ0=sQuery(id+"F3.wireOp",EDGE,"E14");var subQ1=sQuery(id+"F0.wireOp",EDGE,"E0");Q0=makeQuery(id+"F15.boolean.opBoolean","INTERSECT",EDGE,{"disambiguationData":[OD(1.0)],"derivedFrom":[makeQuery(id+"F6.boolean.opBoolean","MERGE",FACE,{"derivedFrom":[makeQuery(id+"F5.boolean.opBoolean","MERGE",FACE,{"derivedFrom":[makeQuery(id+"F4.boolean.opBoolean","MERGE",FACE,{"derivedFrom":[makeQuery(id+"F2.boolean.opBoolean","MERGE",FACE,{"derivedFrom":[makeQuery(id+"F1.opExtrude","SWEPT_FACE",FACE,{"disambiguationData":[OSD([subQ1])]}),makeQuery(id+"F2.opExtrude","SWEPT_FACE",FACE,{"disambiguationData":[OSD([subQ1])]})]}),makeQuery(id+"F4.opExtrude","SWEPT_FACE",FACE,{"disambiguationData":[OSD([subQ0]),TDD([makeQuery(id+"F3.imprint","IMPRINT",EDGE,{"disambiguationData":[TD([[makeQuery(id+"F3.imprint","INTERSECT",VERTEX,{"derivedFrom":[subQ0,sQuery(id+"F3.wireOp",EDGE,"E71.trimOffspring")]}),-1.0]])],"derivedFrom":subQ0})])]}),makeQuery(id+"F4.opExtrude","SWEPT_FACE",FACE,{"disambiguationData":[OSD([subQ0]),TDD([makeQuery(id+"F3.imprint","IMPRINT",EDGE,{"disambiguationData":[TD([[makeQuery(id+"F3.imprint","INTERSECT",VERTEX,{"derivedFrom":[subQ0,sQuery(id+"F3.wireOp",EDGE,"E53")]}),-1.0]])],"derivedFrom":subQ0})])]}),makeQuery(id+"F4.opExtrude","SWEPT_FACE",FACE,{"disambiguationData":[OSD([subQ0]),TDD([makeQuery(id+"F3.imprint","IMPRINT",EDGE,{"disambiguationData":[TD([[makeQuery(id+"F3.imprint","INTERSECT",VERTEX,{"derivedFrom":[subQ0,sQuery(id+"F3.wireOp",EDGE,"E61")]}),-1.0]])],"derivedFrom":subQ0})])]}),makeQuery(id+"F4.opExtrude","SWEPT_FACE",FACE,{"disambiguationData":[OSD([subQ0]),TDD([makeQuery(id+"F3.imprint","IMPRINT",EDGE,{"disambiguationData":[TD([[makeQuery(id+"F3.imprint","INTERSECT",VERTEX,{"derivedFrom":[subQ0,sQuery(id+"F3.wireOp",EDGE,"E63.trimOffspring")]}),-1.0]])],"derivedFrom":subQ0})])]})]}),makeQuery(id+"F5.opExtrude","SWEPT_FACE",FACE,{"disambiguationData":[OSD([subQ0]),TDD([makeQuery(id+"F3.imprint","IMPRINT",EDGE,{"disambiguationData":[TD([[makeQuery(id+"F3.imprint","INTERSECT",VERTEX,{"derivedFrom":[subQ0,sQuery(id+"F3.wireOp",EDGE,"E69.trimOffspring")]}),-1.0]])],"derivedFrom":subQ0})])]}),makeQuery(id+"F5.opExtrude","SWEPT_FACE",FACE,{"disambiguationData":[OSD([subQ0]),TDD([makeQuery(id+"F3.imprint","IMPRINT",EDGE,{"disambiguationData":[TD([[makeQuery(id+"F3.imprint","INTERSECT",VERTEX,{"derivedFrom":[subQ0,sQuery(id+"F3.wireOp",EDGE,"E55")]}),-1.0]])],"derivedFrom":subQ0})])]}),makeQuery(id+"F5.opExtrude","SWEPT_FACE",FACE,{"disambiguationData":[OSD([subQ0]),TDD([makeQuery(id+"F3.imprint","IMPRINT",EDGE,{"disambiguationData":[TD([[makeQuery(id+"F3.imprint","INTERSECT",VERTEX,{"derivedFrom":[subQ0,sQuery(id+"F3.wireOp",EDGE,"E59")]}),-1.0]])],"derivedFrom":subQ0})])]}),makeQuery(id+"F5.opExtrude","SWEPT_FACE",FACE,{"disambiguationData":[OSD([subQ0]),TDD([makeQuery(id+"F3.imprint","IMPRINT",EDGE,{"disambiguationData":[TD([[makeQuery(id+"F3.imprint","INTERSECT",VERTEX,{"derivedFrom":[subQ0,sQuery(id+"F3.wireOp",EDGE,"E65.trimOffspring")]}),-1.0]])],"derivedFrom":subQ0})])]})]}),makeQuery(id+"F6.opExtrude","SWEPT_FACE",FACE,{"disambiguationData":[OSD([subQ0]),TDD([makeQuery(id+"F3.imprint","IMPRINT",EDGE,{"disambiguationData":[TD([[makeQuery(id+"F3.imprint","INTERSECT",VERTEX,{"derivedFrom":[subQ0,sQuery(id+"F3.wireOp",EDGE,"E57")]}),-1.0]])],"derivedFrom":subQ0})])]}),makeQuery(id+"F6.opExtrude","SWEPT_FACE",FACE,{"disambiguationData":[OSD([subQ0]),TDD([makeQuery(id+"F3.imprint","IMPRINT",EDGE,{"disambiguationData":[TD([[makeQuery(id+"F3.imprint","INTERSECT",VERTEX,{"derivedFrom":[subQ0,sQuery(id+"F3.wireOp",EDGE,"E67.trimOffspring")]}),-1.0]])],"derivedFrom":subQ0})])]})]}),makeQuery(id+"F15.opExtrude","SWEPT_FACE",FACE,{"disambiguationData":[OSD([sQuery(id+"F14.wireOp",EDGE,"E133")])]})]});}
            var Q1;
            {var subQ0=sQuery(id+"F3.wireOp",EDGE,"E14");var subQ1=sQuery(id+"F0.wireOp",EDGE,"E0");Q1=makeQuery(id+"F15.boolean.opBoolean","INTERSECT",EDGE,{"disambiguationData":[OD(1.0)],"derivedFrom":[makeQuery(id+"F6.boolean.opBoolean","MERGE",FACE,{"derivedFrom":[makeQuery(id+"F5.boolean.opBoolean","MERGE",FACE,{"derivedFrom":[makeQuery(id+"F4.boolean.opBoolean","MERGE",FACE,{"derivedFrom":[makeQuery(id+"F2.boolean.opBoolean","MERGE",FACE,{"derivedFrom":[makeQuery(id+"F1.opExtrude","SWEPT_FACE",FACE,{"disambiguationData":[OSD([subQ1])]}),makeQuery(id+"F2.opExtrude","SWEPT_FACE",FACE,{"disambiguationData":[OSD([subQ1])]})]}),makeQuery(id+"F4.opExtrude","SWEPT_FACE",FACE,{"disambiguationData":[OSD([subQ0]),TDD([makeQuery(id+"F3.imprint","IMPRINT",EDGE,{"disambiguationData":[TD([[makeQuery(id+"F3.imprint","INTERSECT",VERTEX,{"derivedFrom":[subQ0,sQuery(id+"F3.wireOp",EDGE,"E71.trimOffspring")]}),-1.0]])],"derivedFrom":subQ0})])]}),makeQuery(id+"F4.opExtrude","SWEPT_FACE",FACE,{"disambiguationData":[OSD([subQ0]),TDD([makeQuery(id+"F3.imprint","IMPRINT",EDGE,{"disambiguationData":[TD([[makeQuery(id+"F3.imprint","INTERSECT",VERTEX,{"derivedFrom":[subQ0,sQuery(id+"F3.wireOp",EDGE,"E53")]}),-1.0]])],"derivedFrom":subQ0})])]}),makeQuery(id+"F4.opExtrude","SWEPT_FACE",FACE,{"disambiguationData":[OSD([subQ0]),TDD([makeQuery(id+"F3.imprint","IMPRINT",EDGE,{"disambiguationData":[TD([[makeQuery(id+"F3.imprint","INTERSECT",VERTEX,{"derivedFrom":[subQ0,sQuery(id+"F3.wireOp",EDGE,"E61")]}),-1.0]])],"derivedFrom":subQ0})])]}),makeQuery(id+"F4.opExtrude","SWEPT_FACE",FACE,{"disambiguationData":[OSD([subQ0]),TDD([makeQuery(id+"F3.imprint","IMPRINT",EDGE,{"disambiguationData":[TD([[makeQuery(id+"F3.imprint","INTERSECT",VERTEX,{"derivedFrom":[subQ0,sQuery(id+"F3.wireOp",EDGE,"E63.trimOffspring")]}),-1.0]])],"derivedFrom":subQ0})])]})]}),makeQuery(id+"F5.opExtrude","SWEPT_FACE",FACE,{"disambiguationData":[OSD([subQ0]),TDD([makeQuery(id+"F3.imprint","IMPRINT",EDGE,{"disambiguationData":[TD([[makeQuery(id+"F3.imprint","INTERSECT",VERTEX,{"derivedFrom":[subQ0,sQuery(id+"F3.wireOp",EDGE,"E69.trimOffspring")]}),-1.0]])],"derivedFrom":subQ0})])]}),makeQuery(id+"F5.opExtrude","SWEPT_FACE",FACE,{"disambiguationData":[OSD([subQ0]),TDD([makeQuery(id+"F3.imprint","IMPRINT",EDGE,{"disambiguationData":[TD([[makeQuery(id+"F3.imprint","INTERSECT",VERTEX,{"derivedFrom":[subQ0,sQuery(id+"F3.wireOp",EDGE,"E55")]}),-1.0]])],"derivedFrom":subQ0})])]}),makeQuery(id+"F5.opExtrude","SWEPT_FACE",FACE,{"disambiguationData":[OSD([subQ0]),TDD([makeQuery(id+"F3.imprint","IMPRINT",EDGE,{"disambiguationData":[TD([[makeQuery(id+"F3.imprint","INTERSECT",VERTEX,{"derivedFrom":[subQ0,sQuery(id+"F3.wireOp",EDGE,"E59")]}),-1.0]])],"derivedFrom":subQ0})])]}),makeQuery(id+"F5.opExtrude","SWEPT_FACE",FACE,{"disambiguationData":[OSD([subQ0]),TDD([makeQuery(id+"F3.imprint","IMPRINT",EDGE,{"disambiguationData":[TD([[makeQuery(id+"F3.imprint","INTERSECT",VERTEX,{"derivedFrom":[subQ0,sQuery(id+"F3.wireOp",EDGE,"E65.trimOffspring")]}),-1.0]])],"derivedFrom":subQ0})])]})]}),makeQuery(id+"F6.opExtrude","SWEPT_FACE",FACE,{"disambiguationData":[OSD([subQ0]),TDD([makeQuery(id+"F3.imprint","IMPRINT",EDGE,{"disambiguationData":[TD([[makeQuery(id+"F3.imprint","INTERSECT",VERTEX,{"derivedFrom":[subQ0,sQuery(id+"F3.wireOp",EDGE,"E57")]}),-1.0]])],"derivedFrom":subQ0})])]}),makeQuery(id+"F6.opExtrude","SWEPT_FACE",FACE,{"disambiguationData":[OSD([subQ0]),TDD([makeQuery(id+"F3.imprint","IMPRINT",EDGE,{"disambiguationData":[TD([[makeQuery(id+"F3.imprint","INTERSECT",VERTEX,{"derivedFrom":[subQ0,sQuery(id+"F3.wireOp",EDGE,"E67.trimOffspring")]}),-1.0]])],"derivedFrom":subQ0})])]})]}),makeQuery(id+"F15.opExtrude","SWEPT_FACE",FACE,{"disambiguationData":[OSD([sQuery(id+"F14.wireOp",EDGE,"E132")])]})]});}
            var Q2;
            {var subQ0=sQuery(id+"F3.wireOp",EDGE,"E14");var subQ1=sQuery(id+"F0.wireOp",EDGE,"E0");Q2=makeQuery(id+"F12.boolean.opBoolean","INTERSECT",EDGE,{"disambiguationData":[OD(1.0)],"derivedFrom":[makeQuery(id+"F6.boolean.opBoolean","MERGE",FACE,{"derivedFrom":[makeQuery(id+"F5.boolean.opBoolean","MERGE",FACE,{"derivedFrom":[makeQuery(id+"F4.boolean.opBoolean","MERGE",FACE,{"derivedFrom":[makeQuery(id+"F2.boolean.opBoolean","MERGE",FACE,{"derivedFrom":[makeQuery(id+"F1.opExtrude","SWEPT_FACE",FACE,{"disambiguationData":[OSD([subQ1])]}),makeQuery(id+"F2.opExtrude","SWEPT_FACE",FACE,{"disambiguationData":[OSD([subQ1])]})]}),makeQuery(id+"F4.opExtrude","SWEPT_FACE",FACE,{"disambiguationData":[OSD([subQ0]),TDD([makeQuery(id+"F3.imprint","IMPRINT",EDGE,{"disambiguationData":[TD([[makeQuery(id+"F3.imprint","INTERSECT",VERTEX,{"derivedFrom":[subQ0,sQuery(id+"F3.wireOp",EDGE,"E71.trimOffspring")]}),-1.0]])],"derivedFrom":subQ0})])]}),makeQuery(id+"F4.opExtrude","SWEPT_FACE",FACE,{"disambiguationData":[OSD([subQ0]),TDD([makeQuery(id+"F3.imprint","IMPRINT",EDGE,{"disambiguationData":[TD([[makeQuery(id+"F3.imprint","INTERSECT",VERTEX,{"derivedFrom":[subQ0,sQuery(id+"F3.wireOp",EDGE,"E53")]}),-1.0]])],"derivedFrom":subQ0})])]}),makeQuery(id+"F4.opExtrude","SWEPT_FACE",FACE,{"disambiguationData":[OSD([subQ0]),TDD([makeQuery(id+"F3.imprint","IMPRINT",EDGE,{"disambiguationData":[TD([[makeQuery(id+"F3.imprint","INTERSECT",VERTEX,{"derivedFrom":[subQ0,sQuery(id+"F3.wireOp",EDGE,"E61")]}),-1.0]])],"derivedFrom":subQ0})])]}),makeQuery(id+"F4.opExtrude","SWEPT_FACE",FACE,{"disambiguationData":[OSD([subQ0]),TDD([makeQuery(id+"F3.imprint","IMPRINT",EDGE,{"disambiguationData":[TD([[makeQuery(id+"F3.imprint","INTERSECT",VERTEX,{"derivedFrom":[subQ0,sQuery(id+"F3.wireOp",EDGE,"E63.trimOffspring")]}),-1.0]])],"derivedFrom":subQ0})])]})]}),makeQuery(id+"F5.opExtrude","SWEPT_FACE",FACE,{"disambiguationData":[OSD([subQ0]),TDD([makeQuery(id+"F3.imprint","IMPRINT",EDGE,{"disambiguationData":[TD([[makeQuery(id+"F3.imprint","INTERSECT",VERTEX,{"derivedFrom":[subQ0,sQuery(id+"F3.wireOp",EDGE,"E69.trimOffspring")]}),-1.0]])],"derivedFrom":subQ0})])]}),makeQuery(id+"F5.opExtrude","SWEPT_FACE",FACE,{"disambiguationData":[OSD([subQ0]),TDD([makeQuery(id+"F3.imprint","IMPRINT",EDGE,{"disambiguationData":[TD([[makeQuery(id+"F3.imprint","INTERSECT",VERTEX,{"derivedFrom":[subQ0,sQuery(id+"F3.wireOp",EDGE,"E55")]}),-1.0]])],"derivedFrom":subQ0})])]}),makeQuery(id+"F5.opExtrude","SWEPT_FACE",FACE,{"disambiguationData":[OSD([subQ0]),TDD([makeQuery(id+"F3.imprint","IMPRINT",EDGE,{"disambiguationData":[TD([[makeQuery(id+"F3.imprint","INTERSECT",VERTEX,{"derivedFrom":[subQ0,sQuery(id+"F3.wireOp",EDGE,"E59")]}),-1.0]])],"derivedFrom":subQ0})])]}),makeQuery(id+"F5.opExtrude","SWEPT_FACE",FACE,{"disambiguationData":[OSD([subQ0]),TDD([makeQuery(id+"F3.imprint","IMPRINT",EDGE,{"disambiguationData":[TD([[makeQuery(id+"F3.imprint","INTERSECT",VERTEX,{"derivedFrom":[subQ0,sQuery(id+"F3.wireOp",EDGE,"E65.trimOffspring")]}),-1.0]])],"derivedFrom":subQ0})])]})]}),makeQuery(id+"F6.opExtrude","SWEPT_FACE",FACE,{"disambiguationData":[OSD([subQ0]),TDD([makeQuery(id+"F3.imprint","IMPRINT",EDGE,{"disambiguationData":[TD([[makeQuery(id+"F3.imprint","INTERSECT",VERTEX,{"derivedFrom":[subQ0,sQuery(id+"F3.wireOp",EDGE,"E57")]}),-1.0]])],"derivedFrom":subQ0})])]}),makeQuery(id+"F6.opExtrude","SWEPT_FACE",FACE,{"disambiguationData":[OSD([subQ0]),TDD([makeQuery(id+"F3.imprint","IMPRINT",EDGE,{"disambiguationData":[TD([[makeQuery(id+"F3.imprint","INTERSECT",VERTEX,{"derivedFrom":[subQ0,sQuery(id+"F3.wireOp",EDGE,"E67.trimOffspring")]}),-1.0]])],"derivedFrom":subQ0})])]})]}),makeQuery(id+"F12.opExtrude","SWEPT_FACE",FACE,{"disambiguationData":[OSD([sQuery(id+"F11.wireOp",EDGE,"E131")])]})]});}
            var Q3;
            {var subQ0=sQuery(id+"F3.wireOp",EDGE,"E14");var subQ1=sQuery(id+"F0.wireOp",EDGE,"E0");Q3=makeQuery(id+"F12.boolean.opBoolean","INTERSECT",EDGE,{"disambiguationData":[OD(1.0)],"derivedFrom":[makeQuery(id+"F6.boolean.opBoolean","MERGE",FACE,{"derivedFrom":[makeQuery(id+"F5.boolean.opBoolean","MERGE",FACE,{"derivedFrom":[makeQuery(id+"F4.boolean.opBoolean","MERGE",FACE,{"derivedFrom":[makeQuery(id+"F2.boolean.opBoolean","MERGE",FACE,{"derivedFrom":[makeQuery(id+"F1.opExtrude","SWEPT_FACE",FACE,{"disambiguationData":[OSD([subQ1])]}),makeQuery(id+"F2.opExtrude","SWEPT_FACE",FACE,{"disambiguationData":[OSD([subQ1])]})]}),makeQuery(id+"F4.opExtrude","SWEPT_FACE",FACE,{"disambiguationData":[OSD([subQ0]),TDD([makeQuery(id+"F3.imprint","IMPRINT",EDGE,{"disambiguationData":[TD([[makeQuery(id+"F3.imprint","INTERSECT",VERTEX,{"derivedFrom":[subQ0,sQuery(id+"F3.wireOp",EDGE,"E71.trimOffspring")]}),-1.0]])],"derivedFrom":subQ0})])]}),makeQuery(id+"F4.opExtrude","SWEPT_FACE",FACE,{"disambiguationData":[OSD([subQ0]),TDD([makeQuery(id+"F3.imprint","IMPRINT",EDGE,{"disambiguationData":[TD([[makeQuery(id+"F3.imprint","INTERSECT",VERTEX,{"derivedFrom":[subQ0,sQuery(id+"F3.wireOp",EDGE,"E53")]}),-1.0]])],"derivedFrom":subQ0})])]}),makeQuery(id+"F4.opExtrude","SWEPT_FACE",FACE,{"disambiguationData":[OSD([subQ0]),TDD([makeQuery(id+"F3.imprint","IMPRINT",EDGE,{"disambiguationData":[TD([[makeQuery(id+"F3.imprint","INTERSECT",VERTEX,{"derivedFrom":[subQ0,sQuery(id+"F3.wireOp",EDGE,"E61")]}),-1.0]])],"derivedFrom":subQ0})])]}),makeQuery(id+"F4.opExtrude","SWEPT_FACE",FACE,{"disambiguationData":[OSD([subQ0]),TDD([makeQuery(id+"F3.imprint","IMPRINT",EDGE,{"disambiguationData":[TD([[makeQuery(id+"F3.imprint","INTERSECT",VERTEX,{"derivedFrom":[subQ0,sQuery(id+"F3.wireOp",EDGE,"E63.trimOffspring")]}),-1.0]])],"derivedFrom":subQ0})])]})]}),makeQuery(id+"F5.opExtrude","SWEPT_FACE",FACE,{"disambiguationData":[OSD([subQ0]),TDD([makeQuery(id+"F3.imprint","IMPRINT",EDGE,{"disambiguationData":[TD([[makeQuery(id+"F3.imprint","INTERSECT",VERTEX,{"derivedFrom":[subQ0,sQuery(id+"F3.wireOp",EDGE,"E69.trimOffspring")]}),-1.0]])],"derivedFrom":subQ0})])]}),makeQuery(id+"F5.opExtrude","SWEPT_FACE",FACE,{"disambiguationData":[OSD([subQ0]),TDD([makeQuery(id+"F3.imprint","IMPRINT",EDGE,{"disambiguationData":[TD([[makeQuery(id+"F3.imprint","INTERSECT",VERTEX,{"derivedFrom":[subQ0,sQuery(id+"F3.wireOp",EDGE,"E55")]}),-1.0]])],"derivedFrom":subQ0})])]}),makeQuery(id+"F5.opExtrude","SWEPT_FACE",FACE,{"disambiguationData":[OSD([subQ0]),TDD([makeQuery(id+"F3.imprint","IMPRINT",EDGE,{"disambiguationData":[TD([[makeQuery(id+"F3.imprint","INTERSECT",VERTEX,{"derivedFrom":[subQ0,sQuery(id+"F3.wireOp",EDGE,"E59")]}),-1.0]])],"derivedFrom":subQ0})])]}),makeQuery(id+"F5.opExtrude","SWEPT_FACE",FACE,{"disambiguationData":[OSD([subQ0]),TDD([makeQuery(id+"F3.imprint","IMPRINT",EDGE,{"disambiguationData":[TD([[makeQuery(id+"F3.imprint","INTERSECT",VERTEX,{"derivedFrom":[subQ0,sQuery(id+"F3.wireOp",EDGE,"E65.trimOffspring")]}),-1.0]])],"derivedFrom":subQ0})])]})]}),makeQuery(id+"F6.opExtrude","SWEPT_FACE",FACE,{"disambiguationData":[OSD([subQ0]),TDD([makeQuery(id+"F3.imprint","IMPRINT",EDGE,{"disambiguationData":[TD([[makeQuery(id+"F3.imprint","INTERSECT",VERTEX,{"derivedFrom":[subQ0,sQuery(id+"F3.wireOp",EDGE,"E57")]}),-1.0]])],"derivedFrom":subQ0})])]}),makeQuery(id+"F6.opExtrude","SWEPT_FACE",FACE,{"disambiguationData":[OSD([subQ0]),TDD([makeQuery(id+"F3.imprint","IMPRINT",EDGE,{"disambiguationData":[TD([[makeQuery(id+"F3.imprint","INTERSECT",VERTEX,{"derivedFrom":[subQ0,sQuery(id+"F3.wireOp",EDGE,"E67.trimOffspring")]}),-1.0]])],"derivedFrom":subQ0})])]})]}),makeQuery(id+"F12.opExtrude","SWEPT_FACE",FACE,{"disambiguationData":[OSD([sQuery(id+"F11.wireOp",EDGE,"E130")])]})]});}
            var Q4;
            {var subQ0=sQuery(id+"F3.wireOp",EDGE,"E14");var subQ1=sQuery(id+"F0.wireOp",EDGE,"E0");Q4=makeQuery(id+"F9.boolean.opBoolean","INTERSECT",EDGE,{"disambiguationData":[OD(1.0)],"derivedFrom":[makeQuery(id+"F6.boolean.opBoolean","MERGE",FACE,{"derivedFrom":[makeQuery(id+"F5.boolean.opBoolean","MERGE",FACE,{"derivedFrom":[makeQuery(id+"F4.boolean.opBoolean","MERGE",FACE,{"derivedFrom":[makeQuery(id+"F2.boolean.opBoolean","MERGE",FACE,{"derivedFrom":[makeQuery(id+"F1.opExtrude","SWEPT_FACE",FACE,{"disambiguationData":[OSD([subQ1])]}),makeQuery(id+"F2.opExtrude","SWEPT_FACE",FACE,{"disambiguationData":[OSD([subQ1])]})]}),makeQuery(id+"F4.opExtrude","SWEPT_FACE",FACE,{"disambiguationData":[OSD([subQ0]),TDD([makeQuery(id+"F3.imprint","IMPRINT",EDGE,{"disambiguationData":[TD([[makeQuery(id+"F3.imprint","INTERSECT",VERTEX,{"derivedFrom":[subQ0,sQuery(id+"F3.wireOp",EDGE,"E71.trimOffspring")]}),-1.0]])],"derivedFrom":subQ0})])]}),makeQuery(id+"F4.opExtrude","SWEPT_FACE",FACE,{"disambiguationData":[OSD([subQ0]),TDD([makeQuery(id+"F3.imprint","IMPRINT",EDGE,{"disambiguationData":[TD([[makeQuery(id+"F3.imprint","INTERSECT",VERTEX,{"derivedFrom":[subQ0,sQuery(id+"F3.wireOp",EDGE,"E53")]}),-1.0]])],"derivedFrom":subQ0})])]}),makeQuery(id+"F4.opExtrude","SWEPT_FACE",FACE,{"disambiguationData":[OSD([subQ0]),TDD([makeQuery(id+"F3.imprint","IMPRINT",EDGE,{"disambiguationData":[TD([[makeQuery(id+"F3.imprint","INTERSECT",VERTEX,{"derivedFrom":[subQ0,sQuery(id+"F3.wireOp",EDGE,"E61")]}),-1.0]])],"derivedFrom":subQ0})])]}),makeQuery(id+"F4.opExtrude","SWEPT_FACE",FACE,{"disambiguationData":[OSD([subQ0]),TDD([makeQuery(id+"F3.imprint","IMPRINT",EDGE,{"disambiguationData":[TD([[makeQuery(id+"F3.imprint","INTERSECT",VERTEX,{"derivedFrom":[subQ0,sQuery(id+"F3.wireOp",EDGE,"E63.trimOffspring")]}),-1.0]])],"derivedFrom":subQ0})])]})]}),makeQuery(id+"F5.opExtrude","SWEPT_FACE",FACE,{"disambiguationData":[OSD([subQ0]),TDD([makeQuery(id+"F3.imprint","IMPRINT",EDGE,{"disambiguationData":[TD([[makeQuery(id+"F3.imprint","INTERSECT",VERTEX,{"derivedFrom":[subQ0,sQuery(id+"F3.wireOp",EDGE,"E69.trimOffspring")]}),-1.0]])],"derivedFrom":subQ0})])]}),makeQuery(id+"F5.opExtrude","SWEPT_FACE",FACE,{"disambiguationData":[OSD([subQ0]),TDD([makeQuery(id+"F3.imprint","IMPRINT",EDGE,{"disambiguationData":[TD([[makeQuery(id+"F3.imprint","INTERSECT",VERTEX,{"derivedFrom":[subQ0,sQuery(id+"F3.wireOp",EDGE,"E55")]}),-1.0]])],"derivedFrom":subQ0})])]}),makeQuery(id+"F5.opExtrude","SWEPT_FACE",FACE,{"disambiguationData":[OSD([subQ0]),TDD([makeQuery(id+"F3.imprint","IMPRINT",EDGE,{"disambiguationData":[TD([[makeQuery(id+"F3.imprint","INTERSECT",VERTEX,{"derivedFrom":[subQ0,sQuery(id+"F3.wireOp",EDGE,"E59")]}),-1.0]])],"derivedFrom":subQ0})])]}),makeQuery(id+"F5.opExtrude","SWEPT_FACE",FACE,{"disambiguationData":[OSD([subQ0]),TDD([makeQuery(id+"F3.imprint","IMPRINT",EDGE,{"disambiguationData":[TD([[makeQuery(id+"F3.imprint","INTERSECT",VERTEX,{"derivedFrom":[subQ0,sQuery(id+"F3.wireOp",EDGE,"E65.trimOffspring")]}),-1.0]])],"derivedFrom":subQ0})])]})]}),makeQuery(id+"F6.opExtrude","SWEPT_FACE",FACE,{"disambiguationData":[OSD([subQ0]),TDD([makeQuery(id+"F3.imprint","IMPRINT",EDGE,{"disambiguationData":[TD([[makeQuery(id+"F3.imprint","INTERSECT",VERTEX,{"derivedFrom":[subQ0,sQuery(id+"F3.wireOp",EDGE,"E57")]}),-1.0]])],"derivedFrom":subQ0})])]}),makeQuery(id+"F6.opExtrude","SWEPT_FACE",FACE,{"disambiguationData":[OSD([subQ0]),TDD([makeQuery(id+"F3.imprint","IMPRINT",EDGE,{"disambiguationData":[TD([[makeQuery(id+"F3.imprint","INTERSECT",VERTEX,{"derivedFrom":[subQ0,sQuery(id+"F3.wireOp",EDGE,"E67.trimOffspring")]}),-1.0]])],"derivedFrom":subQ0})])]})]}),makeQuery(id+"F9.opExtrude","SWEPT_FACE",FACE,{"disambiguationData":[OSD([sQuery(id+"F8.wireOp",EDGE,"E129")])]})]});}
            var Q5;
            {var subQ0=sQuery(id+"F3.wireOp",EDGE,"E14");var subQ1=sQuery(id+"F0.wireOp",EDGE,"E0");Q5=makeQuery(id+"F9.boolean.opBoolean","INTERSECT",EDGE,{"disambiguationData":[OD(1.0)],"derivedFrom":[makeQuery(id+"F6.boolean.opBoolean","MERGE",FACE,{"derivedFrom":[makeQuery(id+"F5.boolean.opBoolean","MERGE",FACE,{"derivedFrom":[makeQuery(id+"F4.boolean.opBoolean","MERGE",FACE,{"derivedFrom":[makeQuery(id+"F2.boolean.opBoolean","MERGE",FACE,{"derivedFrom":[makeQuery(id+"F1.opExtrude","SWEPT_FACE",FACE,{"disambiguationData":[OSD([subQ1])]}),makeQuery(id+"F2.opExtrude","SWEPT_FACE",FACE,{"disambiguationData":[OSD([subQ1])]})]}),makeQuery(id+"F4.opExtrude","SWEPT_FACE",FACE,{"disambiguationData":[OSD([subQ0]),TDD([makeQuery(id+"F3.imprint","IMPRINT",EDGE,{"disambiguationData":[TD([[makeQuery(id+"F3.imprint","INTERSECT",VERTEX,{"derivedFrom":[subQ0,sQuery(id+"F3.wireOp",EDGE,"E71.trimOffspring")]}),-1.0]])],"derivedFrom":subQ0})])]}),makeQuery(id+"F4.opExtrude","SWEPT_FACE",FACE,{"disambiguationData":[OSD([subQ0]),TDD([makeQuery(id+"F3.imprint","IMPRINT",EDGE,{"disambiguationData":[TD([[makeQuery(id+"F3.imprint","INTERSECT",VERTEX,{"derivedFrom":[subQ0,sQuery(id+"F3.wireOp",EDGE,"E53")]}),-1.0]])],"derivedFrom":subQ0})])]}),makeQuery(id+"F4.opExtrude","SWEPT_FACE",FACE,{"disambiguationData":[OSD([subQ0]),TDD([makeQuery(id+"F3.imprint","IMPRINT",EDGE,{"disambiguationData":[TD([[makeQuery(id+"F3.imprint","INTERSECT",VERTEX,{"derivedFrom":[subQ0,sQuery(id+"F3.wireOp",EDGE,"E61")]}),-1.0]])],"derivedFrom":subQ0})])]}),makeQuery(id+"F4.opExtrude","SWEPT_FACE",FACE,{"disambiguationData":[OSD([subQ0]),TDD([makeQuery(id+"F3.imprint","IMPRINT",EDGE,{"disambiguationData":[TD([[makeQuery(id+"F3.imprint","INTERSECT",VERTEX,{"derivedFrom":[subQ0,sQuery(id+"F3.wireOp",EDGE,"E63.trimOffspring")]}),-1.0]])],"derivedFrom":subQ0})])]})]}),makeQuery(id+"F5.opExtrude","SWEPT_FACE",FACE,{"disambiguationData":[OSD([subQ0]),TDD([makeQuery(id+"F3.imprint","IMPRINT",EDGE,{"disambiguationData":[TD([[makeQuery(id+"F3.imprint","INTERSECT",VERTEX,{"derivedFrom":[subQ0,sQuery(id+"F3.wireOp",EDGE,"E69.trimOffspring")]}),-1.0]])],"derivedFrom":subQ0})])]}),makeQuery(id+"F5.opExtrude","SWEPT_FACE",FACE,{"disambiguationData":[OSD([subQ0]),TDD([makeQuery(id+"F3.imprint","IMPRINT",EDGE,{"disambiguationData":[TD([[makeQuery(id+"F3.imprint","INTERSECT",VERTEX,{"derivedFrom":[subQ0,sQuery(id+"F3.wireOp",EDGE,"E55")]}),-1.0]])],"derivedFrom":subQ0})])]}),makeQuery(id+"F5.opExtrude","SWEPT_FACE",FACE,{"disambiguationData":[OSD([subQ0]),TDD([makeQuery(id+"F3.imprint","IMPRINT",EDGE,{"disambiguationData":[TD([[makeQuery(id+"F3.imprint","INTERSECT",VERTEX,{"derivedFrom":[subQ0,sQuery(id+"F3.wireOp",EDGE,"E59")]}),-1.0]])],"derivedFrom":subQ0})])]}),makeQuery(id+"F5.opExtrude","SWEPT_FACE",FACE,{"disambiguationData":[OSD([subQ0]),TDD([makeQuery(id+"F3.imprint","IMPRINT",EDGE,{"disambiguationData":[TD([[makeQuery(id+"F3.imprint","INTERSECT",VERTEX,{"derivedFrom":[subQ0,sQuery(id+"F3.wireOp",EDGE,"E65.trimOffspring")]}),-1.0]])],"derivedFrom":subQ0})])]})]}),makeQuery(id+"F6.opExtrude","SWEPT_FACE",FACE,{"disambiguationData":[OSD([subQ0]),TDD([makeQuery(id+"F3.imprint","IMPRINT",EDGE,{"disambiguationData":[TD([[makeQuery(id+"F3.imprint","INTERSECT",VERTEX,{"derivedFrom":[subQ0,sQuery(id+"F3.wireOp",EDGE,"E57")]}),-1.0]])],"derivedFrom":subQ0})])]}),makeQuery(id+"F6.opExtrude","SWEPT_FACE",FACE,{"disambiguationData":[OSD([subQ0]),TDD([makeQuery(id+"F3.imprint","IMPRINT",EDGE,{"disambiguationData":[TD([[makeQuery(id+"F3.imprint","INTERSECT",VERTEX,{"derivedFrom":[subQ0,sQuery(id+"F3.wireOp",EDGE,"E67.trimOffspring")]}),-1.0]])],"derivedFrom":subQ0})])]})]}),makeQuery(id+"F9.opExtrude","SWEPT_FACE",FACE,{"disambiguationData":[OSD([sQuery(id+"F8.wireOp",EDGE,"E128")])]})]});}
            var Q6;
            {var subQ0=sQuery(id+"F3.wireOp",EDGE,"E14");var subQ1=sQuery(id+"F0.wireOp",EDGE,"E0");Q6=makeQuery(id+"F21.boolean.opBoolean","INTERSECT",EDGE,{"disambiguationData":[OD(0.0)],"derivedFrom":[makeQuery(id+"F6.boolean.opBoolean","MERGE",FACE,{"derivedFrom":[makeQuery(id+"F5.boolean.opBoolean","MERGE",FACE,{"derivedFrom":[makeQuery(id+"F4.boolean.opBoolean","MERGE",FACE,{"derivedFrom":[makeQuery(id+"F2.boolean.opBoolean","MERGE",FACE,{"derivedFrom":[makeQuery(id+"F1.opExtrude","SWEPT_FACE",FACE,{"disambiguationData":[OSD([subQ1])]}),makeQuery(id+"F2.opExtrude","SWEPT_FACE",FACE,{"disambiguationData":[OSD([subQ1])]})]}),makeQuery(id+"F4.opExtrude","SWEPT_FACE",FACE,{"disambiguationData":[OSD([subQ0]),TDD([makeQuery(id+"F3.imprint","IMPRINT",EDGE,{"disambiguationData":[TD([[makeQuery(id+"F3.imprint","INTERSECT",VERTEX,{"derivedFrom":[subQ0,sQuery(id+"F3.wireOp",EDGE,"E71.trimOffspring")]}),-1.0]])],"derivedFrom":subQ0})])]}),makeQuery(id+"F4.opExtrude","SWEPT_FACE",FACE,{"disambiguationData":[OSD([subQ0]),TDD([makeQuery(id+"F3.imprint","IMPRINT",EDGE,{"disambiguationData":[TD([[makeQuery(id+"F3.imprint","INTERSECT",VERTEX,{"derivedFrom":[subQ0,sQuery(id+"F3.wireOp",EDGE,"E53")]}),-1.0]])],"derivedFrom":subQ0})])]}),makeQuery(id+"F4.opExtrude","SWEPT_FACE",FACE,{"disambiguationData":[OSD([subQ0]),TDD([makeQuery(id+"F3.imprint","IMPRINT",EDGE,{"disambiguationData":[TD([[makeQuery(id+"F3.imprint","INTERSECT",VERTEX,{"derivedFrom":[subQ0,sQuery(id+"F3.wireOp",EDGE,"E61")]}),-1.0]])],"derivedFrom":subQ0})])]}),makeQuery(id+"F4.opExtrude","SWEPT_FACE",FACE,{"disambiguationData":[OSD([subQ0]),TDD([makeQuery(id+"F3.imprint","IMPRINT",EDGE,{"disambiguationData":[TD([[makeQuery(id+"F3.imprint","INTERSECT",VERTEX,{"derivedFrom":[subQ0,sQuery(id+"F3.wireOp",EDGE,"E63.trimOffspring")]}),-1.0]])],"derivedFrom":subQ0})])]})]}),makeQuery(id+"F5.opExtrude","SWEPT_FACE",FACE,{"disambiguationData":[OSD([subQ0]),TDD([makeQuery(id+"F3.imprint","IMPRINT",EDGE,{"disambiguationData":[TD([[makeQuery(id+"F3.imprint","INTERSECT",VERTEX,{"derivedFrom":[subQ0,sQuery(id+"F3.wireOp",EDGE,"E69.trimOffspring")]}),-1.0]])],"derivedFrom":subQ0})])]}),makeQuery(id+"F5.opExtrude","SWEPT_FACE",FACE,{"disambiguationData":[OSD([subQ0]),TDD([makeQuery(id+"F3.imprint","IMPRINT",EDGE,{"disambiguationData":[TD([[makeQuery(id+"F3.imprint","INTERSECT",VERTEX,{"derivedFrom":[subQ0,sQuery(id+"F3.wireOp",EDGE,"E55")]}),-1.0]])],"derivedFrom":subQ0})])]}),makeQuery(id+"F5.opExtrude","SWEPT_FACE",FACE,{"disambiguationData":[OSD([subQ0]),TDD([makeQuery(id+"F3.imprint","IMPRINT",EDGE,{"disambiguationData":[TD([[makeQuery(id+"F3.imprint","INTERSECT",VERTEX,{"derivedFrom":[subQ0,sQuery(id+"F3.wireOp",EDGE,"E59")]}),-1.0]])],"derivedFrom":subQ0})])]}),makeQuery(id+"F5.opExtrude","SWEPT_FACE",FACE,{"disambiguationData":[OSD([subQ0]),TDD([makeQuery(id+"F3.imprint","IMPRINT",EDGE,{"disambiguationData":[TD([[makeQuery(id+"F3.imprint","INTERSECT",VERTEX,{"derivedFrom":[subQ0,sQuery(id+"F3.wireOp",EDGE,"E65.trimOffspring")]}),-1.0]])],"derivedFrom":subQ0})])]})]}),makeQuery(id+"F6.opExtrude","SWEPT_FACE",FACE,{"disambiguationData":[OSD([subQ0]),TDD([makeQuery(id+"F3.imprint","IMPRINT",EDGE,{"disambiguationData":[TD([[makeQuery(id+"F3.imprint","INTERSECT",VERTEX,{"derivedFrom":[subQ0,sQuery(id+"F3.wireOp",EDGE,"E57")]}),-1.0]])],"derivedFrom":subQ0})])]}),makeQuery(id+"F6.opExtrude","SWEPT_FACE",FACE,{"disambiguationData":[OSD([subQ0]),TDD([makeQuery(id+"F3.imprint","IMPRINT",EDGE,{"disambiguationData":[TD([[makeQuery(id+"F3.imprint","INTERSECT",VERTEX,{"derivedFrom":[subQ0,sQuery(id+"F3.wireOp",EDGE,"E67.trimOffspring")]}),-1.0]])],"derivedFrom":subQ0})])]})]}),makeQuery(id+"F21.opExtrude","SWEPT_FACE",FACE,{"disambiguationData":[OSD([sQuery(id+"F19.wireOp",EDGE,"E136")])]})]});}
            var Q7;
            {var subQ0=sQuery(id+"F3.wireOp",EDGE,"E14");var subQ1=sQuery(id+"F0.wireOp",EDGE,"E0");Q7=makeQuery(id+"F21.boolean.opBoolean","INTERSECT",EDGE,{"disambiguationData":[OD(0.0)],"derivedFrom":[makeQuery(id+"F6.boolean.opBoolean","MERGE",FACE,{"derivedFrom":[makeQuery(id+"F5.boolean.opBoolean","MERGE",FACE,{"derivedFrom":[makeQuery(id+"F4.boolean.opBoolean","MERGE",FACE,{"derivedFrom":[makeQuery(id+"F2.boolean.opBoolean","MERGE",FACE,{"derivedFrom":[makeQuery(id+"F1.opExtrude","SWEPT_FACE",FACE,{"disambiguationData":[OSD([subQ1])]}),makeQuery(id+"F2.opExtrude","SWEPT_FACE",FACE,{"disambiguationData":[OSD([subQ1])]})]}),makeQuery(id+"F4.opExtrude","SWEPT_FACE",FACE,{"disambiguationData":[OSD([subQ0]),TDD([makeQuery(id+"F3.imprint","IMPRINT",EDGE,{"disambiguationData":[TD([[makeQuery(id+"F3.imprint","INTERSECT",VERTEX,{"derivedFrom":[subQ0,sQuery(id+"F3.wireOp",EDGE,"E71.trimOffspring")]}),-1.0]])],"derivedFrom":subQ0})])]}),makeQuery(id+"F4.opExtrude","SWEPT_FACE",FACE,{"disambiguationData":[OSD([subQ0]),TDD([makeQuery(id+"F3.imprint","IMPRINT",EDGE,{"disambiguationData":[TD([[makeQuery(id+"F3.imprint","INTERSECT",VERTEX,{"derivedFrom":[subQ0,sQuery(id+"F3.wireOp",EDGE,"E53")]}),-1.0]])],"derivedFrom":subQ0})])]}),makeQuery(id+"F4.opExtrude","SWEPT_FACE",FACE,{"disambiguationData":[OSD([subQ0]),TDD([makeQuery(id+"F3.imprint","IMPRINT",EDGE,{"disambiguationData":[TD([[makeQuery(id+"F3.imprint","INTERSECT",VERTEX,{"derivedFrom":[subQ0,sQuery(id+"F3.wireOp",EDGE,"E61")]}),-1.0]])],"derivedFrom":subQ0})])]}),makeQuery(id+"F4.opExtrude","SWEPT_FACE",FACE,{"disambiguationData":[OSD([subQ0]),TDD([makeQuery(id+"F3.imprint","IMPRINT",EDGE,{"disambiguationData":[TD([[makeQuery(id+"F3.imprint","INTERSECT",VERTEX,{"derivedFrom":[subQ0,sQuery(id+"F3.wireOp",EDGE,"E63.trimOffspring")]}),-1.0]])],"derivedFrom":subQ0})])]})]}),makeQuery(id+"F5.opExtrude","SWEPT_FACE",FACE,{"disambiguationData":[OSD([subQ0]),TDD([makeQuery(id+"F3.imprint","IMPRINT",EDGE,{"disambiguationData":[TD([[makeQuery(id+"F3.imprint","INTERSECT",VERTEX,{"derivedFrom":[subQ0,sQuery(id+"F3.wireOp",EDGE,"E69.trimOffspring")]}),-1.0]])],"derivedFrom":subQ0})])]}),makeQuery(id+"F5.opExtrude","SWEPT_FACE",FACE,{"disambiguationData":[OSD([subQ0]),TDD([makeQuery(id+"F3.imprint","IMPRINT",EDGE,{"disambiguationData":[TD([[makeQuery(id+"F3.imprint","INTERSECT",VERTEX,{"derivedFrom":[subQ0,sQuery(id+"F3.wireOp",EDGE,"E55")]}),-1.0]])],"derivedFrom":subQ0})])]}),makeQuery(id+"F5.opExtrude","SWEPT_FACE",FACE,{"disambiguationData":[OSD([subQ0]),TDD([makeQuery(id+"F3.imprint","IMPRINT",EDGE,{"disambiguationData":[TD([[makeQuery(id+"F3.imprint","INTERSECT",VERTEX,{"derivedFrom":[subQ0,sQuery(id+"F3.wireOp",EDGE,"E59")]}),-1.0]])],"derivedFrom":subQ0})])]}),makeQuery(id+"F5.opExtrude","SWEPT_FACE",FACE,{"disambiguationData":[OSD([subQ0]),TDD([makeQuery(id+"F3.imprint","IMPRINT",EDGE,{"disambiguationData":[TD([[makeQuery(id+"F3.imprint","INTERSECT",VERTEX,{"derivedFrom":[subQ0,sQuery(id+"F3.wireOp",EDGE,"E65.trimOffspring")]}),-1.0]])],"derivedFrom":subQ0})])]})]}),makeQuery(id+"F6.opExtrude","SWEPT_FACE",FACE,{"disambiguationData":[OSD([subQ0]),TDD([makeQuery(id+"F3.imprint","IMPRINT",EDGE,{"disambiguationData":[TD([[makeQuery(id+"F3.imprint","INTERSECT",VERTEX,{"derivedFrom":[subQ0,sQuery(id+"F3.wireOp",EDGE,"E57")]}),-1.0]])],"derivedFrom":subQ0})])]}),makeQuery(id+"F6.opExtrude","SWEPT_FACE",FACE,{"disambiguationData":[OSD([subQ0]),TDD([makeQuery(id+"F3.imprint","IMPRINT",EDGE,{"disambiguationData":[TD([[makeQuery(id+"F3.imprint","INTERSECT",VERTEX,{"derivedFrom":[subQ0,sQuery(id+"F3.wireOp",EDGE,"E67.trimOffspring")]}),-1.0]])],"derivedFrom":subQ0})])]})]}),makeQuery(id+"F21.opExtrude","SWEPT_FACE",FACE,{"disambiguationData":[OSD([sQuery(id+"F19.wireOp",EDGE,"E137")])]})]});}
            var Q8;
            {var subQ0=sQuery(id+"F3.wireOp",EDGE,"E14");var subQ1=sQuery(id+"F0.wireOp",EDGE,"E0");Q8=makeQuery(id+"F20.boolean.opBoolean","INTERSECT",EDGE,{"disambiguationData":[OD(0.0)],"derivedFrom":[makeQuery(id+"F6.boolean.opBoolean","MERGE",FACE,{"derivedFrom":[makeQuery(id+"F5.boolean.opBoolean","MERGE",FACE,{"derivedFrom":[makeQuery(id+"F4.boolean.opBoolean","MERGE",FACE,{"derivedFrom":[makeQuery(id+"F2.boolean.opBoolean","MERGE",FACE,{"derivedFrom":[makeQuery(id+"F1.opExtrude","SWEPT_FACE",FACE,{"disambiguationData":[OSD([subQ1])]}),makeQuery(id+"F2.opExtrude","SWEPT_FACE",FACE,{"disambiguationData":[OSD([subQ1])]})]}),makeQuery(id+"F4.opExtrude","SWEPT_FACE",FACE,{"disambiguationData":[OSD([subQ0]),TDD([makeQuery(id+"F3.imprint","IMPRINT",EDGE,{"disambiguationData":[TD([[makeQuery(id+"F3.imprint","INTERSECT",VERTEX,{"derivedFrom":[subQ0,sQuery(id+"F3.wireOp",EDGE,"E71.trimOffspring")]}),-1.0]])],"derivedFrom":subQ0})])]}),makeQuery(id+"F4.opExtrude","SWEPT_FACE",FACE,{"disambiguationData":[OSD([subQ0]),TDD([makeQuery(id+"F3.imprint","IMPRINT",EDGE,{"disambiguationData":[TD([[makeQuery(id+"F3.imprint","INTERSECT",VERTEX,{"derivedFrom":[subQ0,sQuery(id+"F3.wireOp",EDGE,"E53")]}),-1.0]])],"derivedFrom":subQ0})])]}),makeQuery(id+"F4.opExtrude","SWEPT_FACE",FACE,{"disambiguationData":[OSD([subQ0]),TDD([makeQuery(id+"F3.imprint","IMPRINT",EDGE,{"disambiguationData":[TD([[makeQuery(id+"F3.imprint","INTERSECT",VERTEX,{"derivedFrom":[subQ0,sQuery(id+"F3.wireOp",EDGE,"E61")]}),-1.0]])],"derivedFrom":subQ0})])]}),makeQuery(id+"F4.opExtrude","SWEPT_FACE",FACE,{"disambiguationData":[OSD([subQ0]),TDD([makeQuery(id+"F3.imprint","IMPRINT",EDGE,{"disambiguationData":[TD([[makeQuery(id+"F3.imprint","INTERSECT",VERTEX,{"derivedFrom":[subQ0,sQuery(id+"F3.wireOp",EDGE,"E63.trimOffspring")]}),-1.0]])],"derivedFrom":subQ0})])]})]}),makeQuery(id+"F5.opExtrude","SWEPT_FACE",FACE,{"disambiguationData":[OSD([subQ0]),TDD([makeQuery(id+"F3.imprint","IMPRINT",EDGE,{"disambiguationData":[TD([[makeQuery(id+"F3.imprint","INTERSECT",VERTEX,{"derivedFrom":[subQ0,sQuery(id+"F3.wireOp",EDGE,"E69.trimOffspring")]}),-1.0]])],"derivedFrom":subQ0})])]}),makeQuery(id+"F5.opExtrude","SWEPT_FACE",FACE,{"disambiguationData":[OSD([subQ0]),TDD([makeQuery(id+"F3.imprint","IMPRINT",EDGE,{"disambiguationData":[TD([[makeQuery(id+"F3.imprint","INTERSECT",VERTEX,{"derivedFrom":[subQ0,sQuery(id+"F3.wireOp",EDGE,"E55")]}),-1.0]])],"derivedFrom":subQ0})])]}),makeQuery(id+"F5.opExtrude","SWEPT_FACE",FACE,{"disambiguationData":[OSD([subQ0]),TDD([makeQuery(id+"F3.imprint","IMPRINT",EDGE,{"disambiguationData":[TD([[makeQuery(id+"F3.imprint","INTERSECT",VERTEX,{"derivedFrom":[subQ0,sQuery(id+"F3.wireOp",EDGE,"E59")]}),-1.0]])],"derivedFrom":subQ0})])]}),makeQuery(id+"F5.opExtrude","SWEPT_FACE",FACE,{"disambiguationData":[OSD([subQ0]),TDD([makeQuery(id+"F3.imprint","IMPRINT",EDGE,{"disambiguationData":[TD([[makeQuery(id+"F3.imprint","INTERSECT",VERTEX,{"derivedFrom":[subQ0,sQuery(id+"F3.wireOp",EDGE,"E65.trimOffspring")]}),-1.0]])],"derivedFrom":subQ0})])]})]}),makeQuery(id+"F6.opExtrude","SWEPT_FACE",FACE,{"disambiguationData":[OSD([subQ0]),TDD([makeQuery(id+"F3.imprint","IMPRINT",EDGE,{"disambiguationData":[TD([[makeQuery(id+"F3.imprint","INTERSECT",VERTEX,{"derivedFrom":[subQ0,sQuery(id+"F3.wireOp",EDGE,"E57")]}),-1.0]])],"derivedFrom":subQ0})])]}),makeQuery(id+"F6.opExtrude","SWEPT_FACE",FACE,{"disambiguationData":[OSD([subQ0]),TDD([makeQuery(id+"F3.imprint","IMPRINT",EDGE,{"disambiguationData":[TD([[makeQuery(id+"F3.imprint","INTERSECT",VERTEX,{"derivedFrom":[subQ0,sQuery(id+"F3.wireOp",EDGE,"E67.trimOffspring")]}),-1.0]])],"derivedFrom":subQ0})])]})]}),makeQuery(id+"F20.opExtrude","SWEPT_FACE",FACE,{"disambiguationData":[OSD([sQuery(id+"F18.wireOp",EDGE,"E134")])]})]});}
            var Q9;
            {var subQ0=sQuery(id+"F3.wireOp",EDGE,"E14");var subQ1=sQuery(id+"F0.wireOp",EDGE,"E0");Q9=makeQuery(id+"F20.boolean.opBoolean","INTERSECT",EDGE,{"disambiguationData":[OD(0.0)],"derivedFrom":[makeQuery(id+"F6.boolean.opBoolean","MERGE",FACE,{"derivedFrom":[makeQuery(id+"F5.boolean.opBoolean","MERGE",FACE,{"derivedFrom":[makeQuery(id+"F4.boolean.opBoolean","MERGE",FACE,{"derivedFrom":[makeQuery(id+"F2.boolean.opBoolean","MERGE",FACE,{"derivedFrom":[makeQuery(id+"F1.opExtrude","SWEPT_FACE",FACE,{"disambiguationData":[OSD([subQ1])]}),makeQuery(id+"F2.opExtrude","SWEPT_FACE",FACE,{"disambiguationData":[OSD([subQ1])]})]}),makeQuery(id+"F4.opExtrude","SWEPT_FACE",FACE,{"disambiguationData":[OSD([subQ0]),TDD([makeQuery(id+"F3.imprint","IMPRINT",EDGE,{"disambiguationData":[TD([[makeQuery(id+"F3.imprint","INTERSECT",VERTEX,{"derivedFrom":[subQ0,sQuery(id+"F3.wireOp",EDGE,"E71.trimOffspring")]}),-1.0]])],"derivedFrom":subQ0})])]}),makeQuery(id+"F4.opExtrude","SWEPT_FACE",FACE,{"disambiguationData":[OSD([subQ0]),TDD([makeQuery(id+"F3.imprint","IMPRINT",EDGE,{"disambiguationData":[TD([[makeQuery(id+"F3.imprint","INTERSECT",VERTEX,{"derivedFrom":[subQ0,sQuery(id+"F3.wireOp",EDGE,"E53")]}),-1.0]])],"derivedFrom":subQ0})])]}),makeQuery(id+"F4.opExtrude","SWEPT_FACE",FACE,{"disambiguationData":[OSD([subQ0]),TDD([makeQuery(id+"F3.imprint","IMPRINT",EDGE,{"disambiguationData":[TD([[makeQuery(id+"F3.imprint","INTERSECT",VERTEX,{"derivedFrom":[subQ0,sQuery(id+"F3.wireOp",EDGE,"E61")]}),-1.0]])],"derivedFrom":subQ0})])]}),makeQuery(id+"F4.opExtrude","SWEPT_FACE",FACE,{"disambiguationData":[OSD([subQ0]),TDD([makeQuery(id+"F3.imprint","IMPRINT",EDGE,{"disambiguationData":[TD([[makeQuery(id+"F3.imprint","INTERSECT",VERTEX,{"derivedFrom":[subQ0,sQuery(id+"F3.wireOp",EDGE,"E63.trimOffspring")]}),-1.0]])],"derivedFrom":subQ0})])]})]}),makeQuery(id+"F5.opExtrude","SWEPT_FACE",FACE,{"disambiguationData":[OSD([subQ0]),TDD([makeQuery(id+"F3.imprint","IMPRINT",EDGE,{"disambiguationData":[TD([[makeQuery(id+"F3.imprint","INTERSECT",VERTEX,{"derivedFrom":[subQ0,sQuery(id+"F3.wireOp",EDGE,"E69.trimOffspring")]}),-1.0]])],"derivedFrom":subQ0})])]}),makeQuery(id+"F5.opExtrude","SWEPT_FACE",FACE,{"disambiguationData":[OSD([subQ0]),TDD([makeQuery(id+"F3.imprint","IMPRINT",EDGE,{"disambiguationData":[TD([[makeQuery(id+"F3.imprint","INTERSECT",VERTEX,{"derivedFrom":[subQ0,sQuery(id+"F3.wireOp",EDGE,"E55")]}),-1.0]])],"derivedFrom":subQ0})])]}),makeQuery(id+"F5.opExtrude","SWEPT_FACE",FACE,{"disambiguationData":[OSD([subQ0]),TDD([makeQuery(id+"F3.imprint","IMPRINT",EDGE,{"disambiguationData":[TD([[makeQuery(id+"F3.imprint","INTERSECT",VERTEX,{"derivedFrom":[subQ0,sQuery(id+"F3.wireOp",EDGE,"E59")]}),-1.0]])],"derivedFrom":subQ0})])]}),makeQuery(id+"F5.opExtrude","SWEPT_FACE",FACE,{"disambiguationData":[OSD([subQ0]),TDD([makeQuery(id+"F3.imprint","IMPRINT",EDGE,{"disambiguationData":[TD([[makeQuery(id+"F3.imprint","INTERSECT",VERTEX,{"derivedFrom":[subQ0,sQuery(id+"F3.wireOp",EDGE,"E65.trimOffspring")]}),-1.0]])],"derivedFrom":subQ0})])]})]}),makeQuery(id+"F6.opExtrude","SWEPT_FACE",FACE,{"disambiguationData":[OSD([subQ0]),TDD([makeQuery(id+"F3.imprint","IMPRINT",EDGE,{"disambiguationData":[TD([[makeQuery(id+"F3.imprint","INTERSECT",VERTEX,{"derivedFrom":[subQ0,sQuery(id+"F3.wireOp",EDGE,"E57")]}),-1.0]])],"derivedFrom":subQ0})])]}),makeQuery(id+"F6.opExtrude","SWEPT_FACE",FACE,{"disambiguationData":[OSD([subQ0]),TDD([makeQuery(id+"F3.imprint","IMPRINT",EDGE,{"disambiguationData":[TD([[makeQuery(id+"F3.imprint","INTERSECT",VERTEX,{"derivedFrom":[subQ0,sQuery(id+"F3.wireOp",EDGE,"E67.trimOffspring")]}),-1.0]])],"derivedFrom":subQ0})])]})]}),makeQuery(id+"F20.opExtrude","SWEPT_FACE",FACE,{"disambiguationData":[OSD([sQuery(id+"F18.wireOp",EDGE,"E135")])]})]});}
            var Q10;
            {var subQ0=sQuery(id+"F3.wireOp",EDGE,"E14");var subQ1=sQuery(id+"F0.wireOp",EDGE,"E0");Q10=makeQuery(id+"F15.boolean.opBoolean","INTERSECT",EDGE,{"disambiguationData":[OD(0.0)],"derivedFrom":[makeQuery(id+"F6.boolean.opBoolean","MERGE",FACE,{"derivedFrom":[makeQuery(id+"F5.boolean.opBoolean","MERGE",FACE,{"derivedFrom":[makeQuery(id+"F4.boolean.opBoolean","MERGE",FACE,{"derivedFrom":[makeQuery(id+"F2.boolean.opBoolean","MERGE",FACE,{"derivedFrom":[makeQuery(id+"F1.opExtrude","SWEPT_FACE",FACE,{"disambiguationData":[OSD([subQ1])]}),makeQuery(id+"F2.opExtrude","SWEPT_FACE",FACE,{"disambiguationData":[OSD([subQ1])]})]}),makeQuery(id+"F4.opExtrude","SWEPT_FACE",FACE,{"disambiguationData":[OSD([subQ0]),TDD([makeQuery(id+"F3.imprint","IMPRINT",EDGE,{"disambiguationData":[TD([[makeQuery(id+"F3.imprint","INTERSECT",VERTEX,{"derivedFrom":[subQ0,sQuery(id+"F3.wireOp",EDGE,"E71.trimOffspring")]}),-1.0]])],"derivedFrom":subQ0})])]}),makeQuery(id+"F4.opExtrude","SWEPT_FACE",FACE,{"disambiguationData":[OSD([subQ0]),TDD([makeQuery(id+"F3.imprint","IMPRINT",EDGE,{"disambiguationData":[TD([[makeQuery(id+"F3.imprint","INTERSECT",VERTEX,{"derivedFrom":[subQ0,sQuery(id+"F3.wireOp",EDGE,"E53")]}),-1.0]])],"derivedFrom":subQ0})])]}),makeQuery(id+"F4.opExtrude","SWEPT_FACE",FACE,{"disambiguationData":[OSD([subQ0]),TDD([makeQuery(id+"F3.imprint","IMPRINT",EDGE,{"disambiguationData":[TD([[makeQuery(id+"F3.imprint","INTERSECT",VERTEX,{"derivedFrom":[subQ0,sQuery(id+"F3.wireOp",EDGE,"E61")]}),-1.0]])],"derivedFrom":subQ0})])]}),makeQuery(id+"F4.opExtrude","SWEPT_FACE",FACE,{"disambiguationData":[OSD([subQ0]),TDD([makeQuery(id+"F3.imprint","IMPRINT",EDGE,{"disambiguationData":[TD([[makeQuery(id+"F3.imprint","INTERSECT",VERTEX,{"derivedFrom":[subQ0,sQuery(id+"F3.wireOp",EDGE,"E63.trimOffspring")]}),-1.0]])],"derivedFrom":subQ0})])]})]}),makeQuery(id+"F5.opExtrude","SWEPT_FACE",FACE,{"disambiguationData":[OSD([subQ0]),TDD([makeQuery(id+"F3.imprint","IMPRINT",EDGE,{"disambiguationData":[TD([[makeQuery(id+"F3.imprint","INTERSECT",VERTEX,{"derivedFrom":[subQ0,sQuery(id+"F3.wireOp",EDGE,"E69.trimOffspring")]}),-1.0]])],"derivedFrom":subQ0})])]}),makeQuery(id+"F5.opExtrude","SWEPT_FACE",FACE,{"disambiguationData":[OSD([subQ0]),TDD([makeQuery(id+"F3.imprint","IMPRINT",EDGE,{"disambiguationData":[TD([[makeQuery(id+"F3.imprint","INTERSECT",VERTEX,{"derivedFrom":[subQ0,sQuery(id+"F3.wireOp",EDGE,"E55")]}),-1.0]])],"derivedFrom":subQ0})])]}),makeQuery(id+"F5.opExtrude","SWEPT_FACE",FACE,{"disambiguationData":[OSD([subQ0]),TDD([makeQuery(id+"F3.imprint","IMPRINT",EDGE,{"disambiguationData":[TD([[makeQuery(id+"F3.imprint","INTERSECT",VERTEX,{"derivedFrom":[subQ0,sQuery(id+"F3.wireOp",EDGE,"E59")]}),-1.0]])],"derivedFrom":subQ0})])]}),makeQuery(id+"F5.opExtrude","SWEPT_FACE",FACE,{"disambiguationData":[OSD([subQ0]),TDD([makeQuery(id+"F3.imprint","IMPRINT",EDGE,{"disambiguationData":[TD([[makeQuery(id+"F3.imprint","INTERSECT",VERTEX,{"derivedFrom":[subQ0,sQuery(id+"F3.wireOp",EDGE,"E65.trimOffspring")]}),-1.0]])],"derivedFrom":subQ0})])]})]}),makeQuery(id+"F6.opExtrude","SWEPT_FACE",FACE,{"disambiguationData":[OSD([subQ0]),TDD([makeQuery(id+"F3.imprint","IMPRINT",EDGE,{"disambiguationData":[TD([[makeQuery(id+"F3.imprint","INTERSECT",VERTEX,{"derivedFrom":[subQ0,sQuery(id+"F3.wireOp",EDGE,"E57")]}),-1.0]])],"derivedFrom":subQ0})])]}),makeQuery(id+"F6.opExtrude","SWEPT_FACE",FACE,{"disambiguationData":[OSD([subQ0]),TDD([makeQuery(id+"F3.imprint","IMPRINT",EDGE,{"disambiguationData":[TD([[makeQuery(id+"F3.imprint","INTERSECT",VERTEX,{"derivedFrom":[subQ0,sQuery(id+"F3.wireOp",EDGE,"E67.trimOffspring")]}),-1.0]])],"derivedFrom":subQ0})])]})]}),makeQuery(id+"F15.opExtrude","SWEPT_FACE",FACE,{"disambiguationData":[OSD([sQuery(id+"F14.wireOp",EDGE,"E132")])]})]});}
            var Q11;
            {var subQ0=sQuery(id+"F3.wireOp",EDGE,"E14");var subQ1=sQuery(id+"F0.wireOp",EDGE,"E0");Q11=makeQuery(id+"F15.boolean.opBoolean","INTERSECT",EDGE,{"disambiguationData":[OD(0.0)],"derivedFrom":[makeQuery(id+"F6.boolean.opBoolean","MERGE",FACE,{"derivedFrom":[makeQuery(id+"F5.boolean.opBoolean","MERGE",FACE,{"derivedFrom":[makeQuery(id+"F4.boolean.opBoolean","MERGE",FACE,{"derivedFrom":[makeQuery(id+"F2.boolean.opBoolean","MERGE",FACE,{"derivedFrom":[makeQuery(id+"F1.opExtrude","SWEPT_FACE",FACE,{"disambiguationData":[OSD([subQ1])]}),makeQuery(id+"F2.opExtrude","SWEPT_FACE",FACE,{"disambiguationData":[OSD([subQ1])]})]}),makeQuery(id+"F4.opExtrude","SWEPT_FACE",FACE,{"disambiguationData":[OSD([subQ0]),TDD([makeQuery(id+"F3.imprint","IMPRINT",EDGE,{"disambiguationData":[TD([[makeQuery(id+"F3.imprint","INTERSECT",VERTEX,{"derivedFrom":[subQ0,sQuery(id+"F3.wireOp",EDGE,"E71.trimOffspring")]}),-1.0]])],"derivedFrom":subQ0})])]}),makeQuery(id+"F4.opExtrude","SWEPT_FACE",FACE,{"disambiguationData":[OSD([subQ0]),TDD([makeQuery(id+"F3.imprint","IMPRINT",EDGE,{"disambiguationData":[TD([[makeQuery(id+"F3.imprint","INTERSECT",VERTEX,{"derivedFrom":[subQ0,sQuery(id+"F3.wireOp",EDGE,"E53")]}),-1.0]])],"derivedFrom":subQ0})])]}),makeQuery(id+"F4.opExtrude","SWEPT_FACE",FACE,{"disambiguationData":[OSD([subQ0]),TDD([makeQuery(id+"F3.imprint","IMPRINT",EDGE,{"disambiguationData":[TD([[makeQuery(id+"F3.imprint","INTERSECT",VERTEX,{"derivedFrom":[subQ0,sQuery(id+"F3.wireOp",EDGE,"E61")]}),-1.0]])],"derivedFrom":subQ0})])]}),makeQuery(id+"F4.opExtrude","SWEPT_FACE",FACE,{"disambiguationData":[OSD([subQ0]),TDD([makeQuery(id+"F3.imprint","IMPRINT",EDGE,{"disambiguationData":[TD([[makeQuery(id+"F3.imprint","INTERSECT",VERTEX,{"derivedFrom":[subQ0,sQuery(id+"F3.wireOp",EDGE,"E63.trimOffspring")]}),-1.0]])],"derivedFrom":subQ0})])]})]}),makeQuery(id+"F5.opExtrude","SWEPT_FACE",FACE,{"disambiguationData":[OSD([subQ0]),TDD([makeQuery(id+"F3.imprint","IMPRINT",EDGE,{"disambiguationData":[TD([[makeQuery(id+"F3.imprint","INTERSECT",VERTEX,{"derivedFrom":[subQ0,sQuery(id+"F3.wireOp",EDGE,"E69.trimOffspring")]}),-1.0]])],"derivedFrom":subQ0})])]}),makeQuery(id+"F5.opExtrude","SWEPT_FACE",FACE,{"disambiguationData":[OSD([subQ0]),TDD([makeQuery(id+"F3.imprint","IMPRINT",EDGE,{"disambiguationData":[TD([[makeQuery(id+"F3.imprint","INTERSECT",VERTEX,{"derivedFrom":[subQ0,sQuery(id+"F3.wireOp",EDGE,"E55")]}),-1.0]])],"derivedFrom":subQ0})])]}),makeQuery(id+"F5.opExtrude","SWEPT_FACE",FACE,{"disambiguationData":[OSD([subQ0]),TDD([makeQuery(id+"F3.imprint","IMPRINT",EDGE,{"disambiguationData":[TD([[makeQuery(id+"F3.imprint","INTERSECT",VERTEX,{"derivedFrom":[subQ0,sQuery(id+"F3.wireOp",EDGE,"E59")]}),-1.0]])],"derivedFrom":subQ0})])]}),makeQuery(id+"F5.opExtrude","SWEPT_FACE",FACE,{"disambiguationData":[OSD([subQ0]),TDD([makeQuery(id+"F3.imprint","IMPRINT",EDGE,{"disambiguationData":[TD([[makeQuery(id+"F3.imprint","INTERSECT",VERTEX,{"derivedFrom":[subQ0,sQuery(id+"F3.wireOp",EDGE,"E65.trimOffspring")]}),-1.0]])],"derivedFrom":subQ0})])]})]}),makeQuery(id+"F6.opExtrude","SWEPT_FACE",FACE,{"disambiguationData":[OSD([subQ0]),TDD([makeQuery(id+"F3.imprint","IMPRINT",EDGE,{"disambiguationData":[TD([[makeQuery(id+"F3.imprint","INTERSECT",VERTEX,{"derivedFrom":[subQ0,sQuery(id+"F3.wireOp",EDGE,"E57")]}),-1.0]])],"derivedFrom":subQ0})])]}),makeQuery(id+"F6.opExtrude","SWEPT_FACE",FACE,{"disambiguationData":[OSD([subQ0]),TDD([makeQuery(id+"F3.imprint","IMPRINT",EDGE,{"disambiguationData":[TD([[makeQuery(id+"F3.imprint","INTERSECT",VERTEX,{"derivedFrom":[subQ0,sQuery(id+"F3.wireOp",EDGE,"E67.trimOffspring")]}),-1.0]])],"derivedFrom":subQ0})])]})]}),makeQuery(id+"F15.opExtrude","SWEPT_FACE",FACE,{"disambiguationData":[OSD([sQuery(id+"F14.wireOp",EDGE,"E133")])]})]});}
            var Q12;
            {var subQ0=sQuery(id+"F3.wireOp",EDGE,"E14");var subQ1=sQuery(id+"F0.wireOp",EDGE,"E0");Q12=makeQuery(id+"F12.boolean.opBoolean","INTERSECT",EDGE,{"disambiguationData":[OD(0.0)],"derivedFrom":[makeQuery(id+"F6.boolean.opBoolean","MERGE",FACE,{"derivedFrom":[makeQuery(id+"F5.boolean.opBoolean","MERGE",FACE,{"derivedFrom":[makeQuery(id+"F4.boolean.opBoolean","MERGE",FACE,{"derivedFrom":[makeQuery(id+"F2.boolean.opBoolean","MERGE",FACE,{"derivedFrom":[makeQuery(id+"F1.opExtrude","SWEPT_FACE",FACE,{"disambiguationData":[OSD([subQ1])]}),makeQuery(id+"F2.opExtrude","SWEPT_FACE",FACE,{"disambiguationData":[OSD([subQ1])]})]}),makeQuery(id+"F4.opExtrude","SWEPT_FACE",FACE,{"disambiguationData":[OSD([subQ0]),TDD([makeQuery(id+"F3.imprint","IMPRINT",EDGE,{"disambiguationData":[TD([[makeQuery(id+"F3.imprint","INTERSECT",VERTEX,{"derivedFrom":[subQ0,sQuery(id+"F3.wireOp",EDGE,"E71.trimOffspring")]}),-1.0]])],"derivedFrom":subQ0})])]}),makeQuery(id+"F4.opExtrude","SWEPT_FACE",FACE,{"disambiguationData":[OSD([subQ0]),TDD([makeQuery(id+"F3.imprint","IMPRINT",EDGE,{"disambiguationData":[TD([[makeQuery(id+"F3.imprint","INTERSECT",VERTEX,{"derivedFrom":[subQ0,sQuery(id+"F3.wireOp",EDGE,"E53")]}),-1.0]])],"derivedFrom":subQ0})])]}),makeQuery(id+"F4.opExtrude","SWEPT_FACE",FACE,{"disambiguationData":[OSD([subQ0]),TDD([makeQuery(id+"F3.imprint","IMPRINT",EDGE,{"disambiguationData":[TD([[makeQuery(id+"F3.imprint","INTERSECT",VERTEX,{"derivedFrom":[subQ0,sQuery(id+"F3.wireOp",EDGE,"E61")]}),-1.0]])],"derivedFrom":subQ0})])]}),makeQuery(id+"F4.opExtrude","SWEPT_FACE",FACE,{"disambiguationData":[OSD([subQ0]),TDD([makeQuery(id+"F3.imprint","IMPRINT",EDGE,{"disambiguationData":[TD([[makeQuery(id+"F3.imprint","INTERSECT",VERTEX,{"derivedFrom":[subQ0,sQuery(id+"F3.wireOp",EDGE,"E63.trimOffspring")]}),-1.0]])],"derivedFrom":subQ0})])]})]}),makeQuery(id+"F5.opExtrude","SWEPT_FACE",FACE,{"disambiguationData":[OSD([subQ0]),TDD([makeQuery(id+"F3.imprint","IMPRINT",EDGE,{"disambiguationData":[TD([[makeQuery(id+"F3.imprint","INTERSECT",VERTEX,{"derivedFrom":[subQ0,sQuery(id+"F3.wireOp",EDGE,"E69.trimOffspring")]}),-1.0]])],"derivedFrom":subQ0})])]}),makeQuery(id+"F5.opExtrude","SWEPT_FACE",FACE,{"disambiguationData":[OSD([subQ0]),TDD([makeQuery(id+"F3.imprint","IMPRINT",EDGE,{"disambiguationData":[TD([[makeQuery(id+"F3.imprint","INTERSECT",VERTEX,{"derivedFrom":[subQ0,sQuery(id+"F3.wireOp",EDGE,"E55")]}),-1.0]])],"derivedFrom":subQ0})])]}),makeQuery(id+"F5.opExtrude","SWEPT_FACE",FACE,{"disambiguationData":[OSD([subQ0]),TDD([makeQuery(id+"F3.imprint","IMPRINT",EDGE,{"disambiguationData":[TD([[makeQuery(id+"F3.imprint","INTERSECT",VERTEX,{"derivedFrom":[subQ0,sQuery(id+"F3.wireOp",EDGE,"E59")]}),-1.0]])],"derivedFrom":subQ0})])]}),makeQuery(id+"F5.opExtrude","SWEPT_FACE",FACE,{"disambiguationData":[OSD([subQ0]),TDD([makeQuery(id+"F3.imprint","IMPRINT",EDGE,{"disambiguationData":[TD([[makeQuery(id+"F3.imprint","INTERSECT",VERTEX,{"derivedFrom":[subQ0,sQuery(id+"F3.wireOp",EDGE,"E65.trimOffspring")]}),-1.0]])],"derivedFrom":subQ0})])]})]}),makeQuery(id+"F6.opExtrude","SWEPT_FACE",FACE,{"disambiguationData":[OSD([subQ0]),TDD([makeQuery(id+"F3.imprint","IMPRINT",EDGE,{"disambiguationData":[TD([[makeQuery(id+"F3.imprint","INTERSECT",VERTEX,{"derivedFrom":[subQ0,sQuery(id+"F3.wireOp",EDGE,"E57")]}),-1.0]])],"derivedFrom":subQ0})])]}),makeQuery(id+"F6.opExtrude","SWEPT_FACE",FACE,{"disambiguationData":[OSD([subQ0]),TDD([makeQuery(id+"F3.imprint","IMPRINT",EDGE,{"disambiguationData":[TD([[makeQuery(id+"F3.imprint","INTERSECT",VERTEX,{"derivedFrom":[subQ0,sQuery(id+"F3.wireOp",EDGE,"E67.trimOffspring")]}),-1.0]])],"derivedFrom":subQ0})])]})]}),makeQuery(id+"F12.opExtrude","SWEPT_FACE",FACE,{"disambiguationData":[OSD([sQuery(id+"F11.wireOp",EDGE,"E130")])]})]});}
            var Q13;
            {var subQ0=sQuery(id+"F3.wireOp",EDGE,"E14");var subQ1=sQuery(id+"F0.wireOp",EDGE,"E0");Q13=makeQuery(id+"F12.boolean.opBoolean","INTERSECT",EDGE,{"disambiguationData":[OD(0.0)],"derivedFrom":[makeQuery(id+"F6.boolean.opBoolean","MERGE",FACE,{"derivedFrom":[makeQuery(id+"F5.boolean.opBoolean","MERGE",FACE,{"derivedFrom":[makeQuery(id+"F4.boolean.opBoolean","MERGE",FACE,{"derivedFrom":[makeQuery(id+"F2.boolean.opBoolean","MERGE",FACE,{"derivedFrom":[makeQuery(id+"F1.opExtrude","SWEPT_FACE",FACE,{"disambiguationData":[OSD([subQ1])]}),makeQuery(id+"F2.opExtrude","SWEPT_FACE",FACE,{"disambiguationData":[OSD([subQ1])]})]}),makeQuery(id+"F4.opExtrude","SWEPT_FACE",FACE,{"disambiguationData":[OSD([subQ0]),TDD([makeQuery(id+"F3.imprint","IMPRINT",EDGE,{"disambiguationData":[TD([[makeQuery(id+"F3.imprint","INTERSECT",VERTEX,{"derivedFrom":[subQ0,sQuery(id+"F3.wireOp",EDGE,"E71.trimOffspring")]}),-1.0]])],"derivedFrom":subQ0})])]}),makeQuery(id+"F4.opExtrude","SWEPT_FACE",FACE,{"disambiguationData":[OSD([subQ0]),TDD([makeQuery(id+"F3.imprint","IMPRINT",EDGE,{"disambiguationData":[TD([[makeQuery(id+"F3.imprint","INTERSECT",VERTEX,{"derivedFrom":[subQ0,sQuery(id+"F3.wireOp",EDGE,"E53")]}),-1.0]])],"derivedFrom":subQ0})])]}),makeQuery(id+"F4.opExtrude","SWEPT_FACE",FACE,{"disambiguationData":[OSD([subQ0]),TDD([makeQuery(id+"F3.imprint","IMPRINT",EDGE,{"disambiguationData":[TD([[makeQuery(id+"F3.imprint","INTERSECT",VERTEX,{"derivedFrom":[subQ0,sQuery(id+"F3.wireOp",EDGE,"E61")]}),-1.0]])],"derivedFrom":subQ0})])]}),makeQuery(id+"F4.opExtrude","SWEPT_FACE",FACE,{"disambiguationData":[OSD([subQ0]),TDD([makeQuery(id+"F3.imprint","IMPRINT",EDGE,{"disambiguationData":[TD([[makeQuery(id+"F3.imprint","INTERSECT",VERTEX,{"derivedFrom":[subQ0,sQuery(id+"F3.wireOp",EDGE,"E63.trimOffspring")]}),-1.0]])],"derivedFrom":subQ0})])]})]}),makeQuery(id+"F5.opExtrude","SWEPT_FACE",FACE,{"disambiguationData":[OSD([subQ0]),TDD([makeQuery(id+"F3.imprint","IMPRINT",EDGE,{"disambiguationData":[TD([[makeQuery(id+"F3.imprint","INTERSECT",VERTEX,{"derivedFrom":[subQ0,sQuery(id+"F3.wireOp",EDGE,"E69.trimOffspring")]}),-1.0]])],"derivedFrom":subQ0})])]}),makeQuery(id+"F5.opExtrude","SWEPT_FACE",FACE,{"disambiguationData":[OSD([subQ0]),TDD([makeQuery(id+"F3.imprint","IMPRINT",EDGE,{"disambiguationData":[TD([[makeQuery(id+"F3.imprint","INTERSECT",VERTEX,{"derivedFrom":[subQ0,sQuery(id+"F3.wireOp",EDGE,"E55")]}),-1.0]])],"derivedFrom":subQ0})])]}),makeQuery(id+"F5.opExtrude","SWEPT_FACE",FACE,{"disambiguationData":[OSD([subQ0]),TDD([makeQuery(id+"F3.imprint","IMPRINT",EDGE,{"disambiguationData":[TD([[makeQuery(id+"F3.imprint","INTERSECT",VERTEX,{"derivedFrom":[subQ0,sQuery(id+"F3.wireOp",EDGE,"E59")]}),-1.0]])],"derivedFrom":subQ0})])]}),makeQuery(id+"F5.opExtrude","SWEPT_FACE",FACE,{"disambiguationData":[OSD([subQ0]),TDD([makeQuery(id+"F3.imprint","IMPRINT",EDGE,{"disambiguationData":[TD([[makeQuery(id+"F3.imprint","INTERSECT",VERTEX,{"derivedFrom":[subQ0,sQuery(id+"F3.wireOp",EDGE,"E65.trimOffspring")]}),-1.0]])],"derivedFrom":subQ0})])]})]}),makeQuery(id+"F6.opExtrude","SWEPT_FACE",FACE,{"disambiguationData":[OSD([subQ0]),TDD([makeQuery(id+"F3.imprint","IMPRINT",EDGE,{"disambiguationData":[TD([[makeQuery(id+"F3.imprint","INTERSECT",VERTEX,{"derivedFrom":[subQ0,sQuery(id+"F3.wireOp",EDGE,"E57")]}),-1.0]])],"derivedFrom":subQ0})])]}),makeQuery(id+"F6.opExtrude","SWEPT_FACE",FACE,{"disambiguationData":[OSD([subQ0]),TDD([makeQuery(id+"F3.imprint","IMPRINT",EDGE,{"disambiguationData":[TD([[makeQuery(id+"F3.imprint","INTERSECT",VERTEX,{"derivedFrom":[subQ0,sQuery(id+"F3.wireOp",EDGE,"E67.trimOffspring")]}),-1.0]])],"derivedFrom":subQ0})])]})]}),makeQuery(id+"F12.opExtrude","SWEPT_FACE",FACE,{"disambiguationData":[OSD([sQuery(id+"F11.wireOp",EDGE,"E131")])]})]});}
            var Q14;
            {var subQ0=sQuery(id+"F3.wireOp",EDGE,"E14");var subQ1=sQuery(id+"F0.wireOp",EDGE,"E0");Q14=makeQuery(id+"F9.boolean.opBoolean","INTERSECT",EDGE,{"disambiguationData":[OD(0.0)],"derivedFrom":[makeQuery(id+"F6.boolean.opBoolean","MERGE",FACE,{"derivedFrom":[makeQuery(id+"F5.boolean.opBoolean","MERGE",FACE,{"derivedFrom":[makeQuery(id+"F4.boolean.opBoolean","MERGE",FACE,{"derivedFrom":[makeQuery(id+"F2.boolean.opBoolean","MERGE",FACE,{"derivedFrom":[makeQuery(id+"F1.opExtrude","SWEPT_FACE",FACE,{"disambiguationData":[OSD([subQ1])]}),makeQuery(id+"F2.opExtrude","SWEPT_FACE",FACE,{"disambiguationData":[OSD([subQ1])]})]}),makeQuery(id+"F4.opExtrude","SWEPT_FACE",FACE,{"disambiguationData":[OSD([subQ0]),TDD([makeQuery(id+"F3.imprint","IMPRINT",EDGE,{"disambiguationData":[TD([[makeQuery(id+"F3.imprint","INTERSECT",VERTEX,{"derivedFrom":[subQ0,sQuery(id+"F3.wireOp",EDGE,"E71.trimOffspring")]}),-1.0]])],"derivedFrom":subQ0})])]}),makeQuery(id+"F4.opExtrude","SWEPT_FACE",FACE,{"disambiguationData":[OSD([subQ0]),TDD([makeQuery(id+"F3.imprint","IMPRINT",EDGE,{"disambiguationData":[TD([[makeQuery(id+"F3.imprint","INTERSECT",VERTEX,{"derivedFrom":[subQ0,sQuery(id+"F3.wireOp",EDGE,"E53")]}),-1.0]])],"derivedFrom":subQ0})])]}),makeQuery(id+"F4.opExtrude","SWEPT_FACE",FACE,{"disambiguationData":[OSD([subQ0]),TDD([makeQuery(id+"F3.imprint","IMPRINT",EDGE,{"disambiguationData":[TD([[makeQuery(id+"F3.imprint","INTERSECT",VERTEX,{"derivedFrom":[subQ0,sQuery(id+"F3.wireOp",EDGE,"E61")]}),-1.0]])],"derivedFrom":subQ0})])]}),makeQuery(id+"F4.opExtrude","SWEPT_FACE",FACE,{"disambiguationData":[OSD([subQ0]),TDD([makeQuery(id+"F3.imprint","IMPRINT",EDGE,{"disambiguationData":[TD([[makeQuery(id+"F3.imprint","INTERSECT",VERTEX,{"derivedFrom":[subQ0,sQuery(id+"F3.wireOp",EDGE,"E63.trimOffspring")]}),-1.0]])],"derivedFrom":subQ0})])]})]}),makeQuery(id+"F5.opExtrude","SWEPT_FACE",FACE,{"disambiguationData":[OSD([subQ0]),TDD([makeQuery(id+"F3.imprint","IMPRINT",EDGE,{"disambiguationData":[TD([[makeQuery(id+"F3.imprint","INTERSECT",VERTEX,{"derivedFrom":[subQ0,sQuery(id+"F3.wireOp",EDGE,"E69.trimOffspring")]}),-1.0]])],"derivedFrom":subQ0})])]}),makeQuery(id+"F5.opExtrude","SWEPT_FACE",FACE,{"disambiguationData":[OSD([subQ0]),TDD([makeQuery(id+"F3.imprint","IMPRINT",EDGE,{"disambiguationData":[TD([[makeQuery(id+"F3.imprint","INTERSECT",VERTEX,{"derivedFrom":[subQ0,sQuery(id+"F3.wireOp",EDGE,"E55")]}),-1.0]])],"derivedFrom":subQ0})])]}),makeQuery(id+"F5.opExtrude","SWEPT_FACE",FACE,{"disambiguationData":[OSD([subQ0]),TDD([makeQuery(id+"F3.imprint","IMPRINT",EDGE,{"disambiguationData":[TD([[makeQuery(id+"F3.imprint","INTERSECT",VERTEX,{"derivedFrom":[subQ0,sQuery(id+"F3.wireOp",EDGE,"E59")]}),-1.0]])],"derivedFrom":subQ0})])]}),makeQuery(id+"F5.opExtrude","SWEPT_FACE",FACE,{"disambiguationData":[OSD([subQ0]),TDD([makeQuery(id+"F3.imprint","IMPRINT",EDGE,{"disambiguationData":[TD([[makeQuery(id+"F3.imprint","INTERSECT",VERTEX,{"derivedFrom":[subQ0,sQuery(id+"F3.wireOp",EDGE,"E65.trimOffspring")]}),-1.0]])],"derivedFrom":subQ0})])]})]}),makeQuery(id+"F6.opExtrude","SWEPT_FACE",FACE,{"disambiguationData":[OSD([subQ0]),TDD([makeQuery(id+"F3.imprint","IMPRINT",EDGE,{"disambiguationData":[TD([[makeQuery(id+"F3.imprint","INTERSECT",VERTEX,{"derivedFrom":[subQ0,sQuery(id+"F3.wireOp",EDGE,"E57")]}),-1.0]])],"derivedFrom":subQ0})])]}),makeQuery(id+"F6.opExtrude","SWEPT_FACE",FACE,{"disambiguationData":[OSD([subQ0]),TDD([makeQuery(id+"F3.imprint","IMPRINT",EDGE,{"disambiguationData":[TD([[makeQuery(id+"F3.imprint","INTERSECT",VERTEX,{"derivedFrom":[subQ0,sQuery(id+"F3.wireOp",EDGE,"E67.trimOffspring")]}),-1.0]])],"derivedFrom":subQ0})])]})]}),makeQuery(id+"F9.opExtrude","SWEPT_FACE",FACE,{"disambiguationData":[OSD([sQuery(id+"F8.wireOp",EDGE,"E129")])]})]});}
            var Q15;
            {var subQ0=sQuery(id+"F3.wireOp",EDGE,"E14");var subQ1=sQuery(id+"F0.wireOp",EDGE,"E0");Q15=makeQuery(id+"F9.boolean.opBoolean","INTERSECT",EDGE,{"disambiguationData":[OD(0.0)],"derivedFrom":[makeQuery(id+"F6.boolean.opBoolean","MERGE",FACE,{"derivedFrom":[makeQuery(id+"F5.boolean.opBoolean","MERGE",FACE,{"derivedFrom":[makeQuery(id+"F4.boolean.opBoolean","MERGE",FACE,{"derivedFrom":[makeQuery(id+"F2.boolean.opBoolean","MERGE",FACE,{"derivedFrom":[makeQuery(id+"F1.opExtrude","SWEPT_FACE",FACE,{"disambiguationData":[OSD([subQ1])]}),makeQuery(id+"F2.opExtrude","SWEPT_FACE",FACE,{"disambiguationData":[OSD([subQ1])]})]}),makeQuery(id+"F4.opExtrude","SWEPT_FACE",FACE,{"disambiguationData":[OSD([subQ0]),TDD([makeQuery(id+"F3.imprint","IMPRINT",EDGE,{"disambiguationData":[TD([[makeQuery(id+"F3.imprint","INTERSECT",VERTEX,{"derivedFrom":[subQ0,sQuery(id+"F3.wireOp",EDGE,"E71.trimOffspring")]}),-1.0]])],"derivedFrom":subQ0})])]}),makeQuery(id+"F4.opExtrude","SWEPT_FACE",FACE,{"disambiguationData":[OSD([subQ0]),TDD([makeQuery(id+"F3.imprint","IMPRINT",EDGE,{"disambiguationData":[TD([[makeQuery(id+"F3.imprint","INTERSECT",VERTEX,{"derivedFrom":[subQ0,sQuery(id+"F3.wireOp",EDGE,"E53")]}),-1.0]])],"derivedFrom":subQ0})])]}),makeQuery(id+"F4.opExtrude","SWEPT_FACE",FACE,{"disambiguationData":[OSD([subQ0]),TDD([makeQuery(id+"F3.imprint","IMPRINT",EDGE,{"disambiguationData":[TD([[makeQuery(id+"F3.imprint","INTERSECT",VERTEX,{"derivedFrom":[subQ0,sQuery(id+"F3.wireOp",EDGE,"E61")]}),-1.0]])],"derivedFrom":subQ0})])]}),makeQuery(id+"F4.opExtrude","SWEPT_FACE",FACE,{"disambiguationData":[OSD([subQ0]),TDD([makeQuery(id+"F3.imprint","IMPRINT",EDGE,{"disambiguationData":[TD([[makeQuery(id+"F3.imprint","INTERSECT",VERTEX,{"derivedFrom":[subQ0,sQuery(id+"F3.wireOp",EDGE,"E63.trimOffspring")]}),-1.0]])],"derivedFrom":subQ0})])]})]}),makeQuery(id+"F5.opExtrude","SWEPT_FACE",FACE,{"disambiguationData":[OSD([subQ0]),TDD([makeQuery(id+"F3.imprint","IMPRINT",EDGE,{"disambiguationData":[TD([[makeQuery(id+"F3.imprint","INTERSECT",VERTEX,{"derivedFrom":[subQ0,sQuery(id+"F3.wireOp",EDGE,"E69.trimOffspring")]}),-1.0]])],"derivedFrom":subQ0})])]}),makeQuery(id+"F5.opExtrude","SWEPT_FACE",FACE,{"disambiguationData":[OSD([subQ0]),TDD([makeQuery(id+"F3.imprint","IMPRINT",EDGE,{"disambiguationData":[TD([[makeQuery(id+"F3.imprint","INTERSECT",VERTEX,{"derivedFrom":[subQ0,sQuery(id+"F3.wireOp",EDGE,"E55")]}),-1.0]])],"derivedFrom":subQ0})])]}),makeQuery(id+"F5.opExtrude","SWEPT_FACE",FACE,{"disambiguationData":[OSD([subQ0]),TDD([makeQuery(id+"F3.imprint","IMPRINT",EDGE,{"disambiguationData":[TD([[makeQuery(id+"F3.imprint","INTERSECT",VERTEX,{"derivedFrom":[subQ0,sQuery(id+"F3.wireOp",EDGE,"E59")]}),-1.0]])],"derivedFrom":subQ0})])]}),makeQuery(id+"F5.opExtrude","SWEPT_FACE",FACE,{"disambiguationData":[OSD([subQ0]),TDD([makeQuery(id+"F3.imprint","IMPRINT",EDGE,{"disambiguationData":[TD([[makeQuery(id+"F3.imprint","INTERSECT",VERTEX,{"derivedFrom":[subQ0,sQuery(id+"F3.wireOp",EDGE,"E65.trimOffspring")]}),-1.0]])],"derivedFrom":subQ0})])]})]}),makeQuery(id+"F6.opExtrude","SWEPT_FACE",FACE,{"disambiguationData":[OSD([subQ0]),TDD([makeQuery(id+"F3.imprint","IMPRINT",EDGE,{"disambiguationData":[TD([[makeQuery(id+"F3.imprint","INTERSECT",VERTEX,{"derivedFrom":[subQ0,sQuery(id+"F3.wireOp",EDGE,"E57")]}),-1.0]])],"derivedFrom":subQ0})])]}),makeQuery(id+"F6.opExtrude","SWEPT_FACE",FACE,{"disambiguationData":[OSD([subQ0]),TDD([makeQuery(id+"F3.imprint","IMPRINT",EDGE,{"disambiguationData":[TD([[makeQuery(id+"F3.imprint","INTERSECT",VERTEX,{"derivedFrom":[subQ0,sQuery(id+"F3.wireOp",EDGE,"E67.trimOffspring")]}),-1.0]])],"derivedFrom":subQ0})])]})]}),makeQuery(id+"F9.opExtrude","SWEPT_FACE",FACE,{"disambiguationData":[OSD([sQuery(id+"F8.wireOp",EDGE,"E128")])]})]});}
            var Q16;
            {var subQ0=sQuery(id+"F3.wireOp",EDGE,"E14");var subQ1=sQuery(id+"F0.wireOp",EDGE,"E0");Q16=makeQuery(id+"F21.boolean.opBoolean","INTERSECT",EDGE,{"disambiguationData":[OD(1.0)],"derivedFrom":[makeQuery(id+"F6.boolean.opBoolean","MERGE",FACE,{"derivedFrom":[makeQuery(id+"F5.boolean.opBoolean","MERGE",FACE,{"derivedFrom":[makeQuery(id+"F4.boolean.opBoolean","MERGE",FACE,{"derivedFrom":[makeQuery(id+"F2.boolean.opBoolean","MERGE",FACE,{"derivedFrom":[makeQuery(id+"F1.opExtrude","SWEPT_FACE",FACE,{"disambiguationData":[OSD([subQ1])]}),makeQuery(id+"F2.opExtrude","SWEPT_FACE",FACE,{"disambiguationData":[OSD([subQ1])]})]}),makeQuery(id+"F4.opExtrude","SWEPT_FACE",FACE,{"disambiguationData":[OSD([subQ0]),TDD([makeQuery(id+"F3.imprint","IMPRINT",EDGE,{"disambiguationData":[TD([[makeQuery(id+"F3.imprint","INTERSECT",VERTEX,{"derivedFrom":[subQ0,sQuery(id+"F3.wireOp",EDGE,"E71.trimOffspring")]}),-1.0]])],"derivedFrom":subQ0})])]}),makeQuery(id+"F4.opExtrude","SWEPT_FACE",FACE,{"disambiguationData":[OSD([subQ0]),TDD([makeQuery(id+"F3.imprint","IMPRINT",EDGE,{"disambiguationData":[TD([[makeQuery(id+"F3.imprint","INTERSECT",VERTEX,{"derivedFrom":[subQ0,sQuery(id+"F3.wireOp",EDGE,"E53")]}),-1.0]])],"derivedFrom":subQ0})])]}),makeQuery(id+"F4.opExtrude","SWEPT_FACE",FACE,{"disambiguationData":[OSD([subQ0]),TDD([makeQuery(id+"F3.imprint","IMPRINT",EDGE,{"disambiguationData":[TD([[makeQuery(id+"F3.imprint","INTERSECT",VERTEX,{"derivedFrom":[subQ0,sQuery(id+"F3.wireOp",EDGE,"E61")]}),-1.0]])],"derivedFrom":subQ0})])]}),makeQuery(id+"F4.opExtrude","SWEPT_FACE",FACE,{"disambiguationData":[OSD([subQ0]),TDD([makeQuery(id+"F3.imprint","IMPRINT",EDGE,{"disambiguationData":[TD([[makeQuery(id+"F3.imprint","INTERSECT",VERTEX,{"derivedFrom":[subQ0,sQuery(id+"F3.wireOp",EDGE,"E63.trimOffspring")]}),-1.0]])],"derivedFrom":subQ0})])]})]}),makeQuery(id+"F5.opExtrude","SWEPT_FACE",FACE,{"disambiguationData":[OSD([subQ0]),TDD([makeQuery(id+"F3.imprint","IMPRINT",EDGE,{"disambiguationData":[TD([[makeQuery(id+"F3.imprint","INTERSECT",VERTEX,{"derivedFrom":[subQ0,sQuery(id+"F3.wireOp",EDGE,"E69.trimOffspring")]}),-1.0]])],"derivedFrom":subQ0})])]}),makeQuery(id+"F5.opExtrude","SWEPT_FACE",FACE,{"disambiguationData":[OSD([subQ0]),TDD([makeQuery(id+"F3.imprint","IMPRINT",EDGE,{"disambiguationData":[TD([[makeQuery(id+"F3.imprint","INTERSECT",VERTEX,{"derivedFrom":[subQ0,sQuery(id+"F3.wireOp",EDGE,"E55")]}),-1.0]])],"derivedFrom":subQ0})])]}),makeQuery(id+"F5.opExtrude","SWEPT_FACE",FACE,{"disambiguationData":[OSD([subQ0]),TDD([makeQuery(id+"F3.imprint","IMPRINT",EDGE,{"disambiguationData":[TD([[makeQuery(id+"F3.imprint","INTERSECT",VERTEX,{"derivedFrom":[subQ0,sQuery(id+"F3.wireOp",EDGE,"E59")]}),-1.0]])],"derivedFrom":subQ0})])]}),makeQuery(id+"F5.opExtrude","SWEPT_FACE",FACE,{"disambiguationData":[OSD([subQ0]),TDD([makeQuery(id+"F3.imprint","IMPRINT",EDGE,{"disambiguationData":[TD([[makeQuery(id+"F3.imprint","INTERSECT",VERTEX,{"derivedFrom":[subQ0,sQuery(id+"F3.wireOp",EDGE,"E65.trimOffspring")]}),-1.0]])],"derivedFrom":subQ0})])]})]}),makeQuery(id+"F6.opExtrude","SWEPT_FACE",FACE,{"disambiguationData":[OSD([subQ0]),TDD([makeQuery(id+"F3.imprint","IMPRINT",EDGE,{"disambiguationData":[TD([[makeQuery(id+"F3.imprint","INTERSECT",VERTEX,{"derivedFrom":[subQ0,sQuery(id+"F3.wireOp",EDGE,"E57")]}),-1.0]])],"derivedFrom":subQ0})])]}),makeQuery(id+"F6.opExtrude","SWEPT_FACE",FACE,{"disambiguationData":[OSD([subQ0]),TDD([makeQuery(id+"F3.imprint","IMPRINT",EDGE,{"disambiguationData":[TD([[makeQuery(id+"F3.imprint","INTERSECT",VERTEX,{"derivedFrom":[subQ0,sQuery(id+"F3.wireOp",EDGE,"E67.trimOffspring")]}),-1.0]])],"derivedFrom":subQ0})])]})]}),makeQuery(id+"F21.opExtrude","SWEPT_FACE",FACE,{"disambiguationData":[OSD([sQuery(id+"F19.wireOp",EDGE,"E136")])]})]});}
            var Q17;
            {var subQ0=sQuery(id+"F3.wireOp",EDGE,"E14");var subQ1=sQuery(id+"F0.wireOp",EDGE,"E0");Q17=makeQuery(id+"F21.boolean.opBoolean","INTERSECT",EDGE,{"disambiguationData":[OD(1.0)],"derivedFrom":[makeQuery(id+"F6.boolean.opBoolean","MERGE",FACE,{"derivedFrom":[makeQuery(id+"F5.boolean.opBoolean","MERGE",FACE,{"derivedFrom":[makeQuery(id+"F4.boolean.opBoolean","MERGE",FACE,{"derivedFrom":[makeQuery(id+"F2.boolean.opBoolean","MERGE",FACE,{"derivedFrom":[makeQuery(id+"F1.opExtrude","SWEPT_FACE",FACE,{"disambiguationData":[OSD([subQ1])]}),makeQuery(id+"F2.opExtrude","SWEPT_FACE",FACE,{"disambiguationData":[OSD([subQ1])]})]}),makeQuery(id+"F4.opExtrude","SWEPT_FACE",FACE,{"disambiguationData":[OSD([subQ0]),TDD([makeQuery(id+"F3.imprint","IMPRINT",EDGE,{"disambiguationData":[TD([[makeQuery(id+"F3.imprint","INTERSECT",VERTEX,{"derivedFrom":[subQ0,sQuery(id+"F3.wireOp",EDGE,"E71.trimOffspring")]}),-1.0]])],"derivedFrom":subQ0})])]}),makeQuery(id+"F4.opExtrude","SWEPT_FACE",FACE,{"disambiguationData":[OSD([subQ0]),TDD([makeQuery(id+"F3.imprint","IMPRINT",EDGE,{"disambiguationData":[TD([[makeQuery(id+"F3.imprint","INTERSECT",VERTEX,{"derivedFrom":[subQ0,sQuery(id+"F3.wireOp",EDGE,"E53")]}),-1.0]])],"derivedFrom":subQ0})])]}),makeQuery(id+"F4.opExtrude","SWEPT_FACE",FACE,{"disambiguationData":[OSD([subQ0]),TDD([makeQuery(id+"F3.imprint","IMPRINT",EDGE,{"disambiguationData":[TD([[makeQuery(id+"F3.imprint","INTERSECT",VERTEX,{"derivedFrom":[subQ0,sQuery(id+"F3.wireOp",EDGE,"E61")]}),-1.0]])],"derivedFrom":subQ0})])]}),makeQuery(id+"F4.opExtrude","SWEPT_FACE",FACE,{"disambiguationData":[OSD([subQ0]),TDD([makeQuery(id+"F3.imprint","IMPRINT",EDGE,{"disambiguationData":[TD([[makeQuery(id+"F3.imprint","INTERSECT",VERTEX,{"derivedFrom":[subQ0,sQuery(id+"F3.wireOp",EDGE,"E63.trimOffspring")]}),-1.0]])],"derivedFrom":subQ0})])]})]}),makeQuery(id+"F5.opExtrude","SWEPT_FACE",FACE,{"disambiguationData":[OSD([subQ0]),TDD([makeQuery(id+"F3.imprint","IMPRINT",EDGE,{"disambiguationData":[TD([[makeQuery(id+"F3.imprint","INTERSECT",VERTEX,{"derivedFrom":[subQ0,sQuery(id+"F3.wireOp",EDGE,"E69.trimOffspring")]}),-1.0]])],"derivedFrom":subQ0})])]}),makeQuery(id+"F5.opExtrude","SWEPT_FACE",FACE,{"disambiguationData":[OSD([subQ0]),TDD([makeQuery(id+"F3.imprint","IMPRINT",EDGE,{"disambiguationData":[TD([[makeQuery(id+"F3.imprint","INTERSECT",VERTEX,{"derivedFrom":[subQ0,sQuery(id+"F3.wireOp",EDGE,"E55")]}),-1.0]])],"derivedFrom":subQ0})])]}),makeQuery(id+"F5.opExtrude","SWEPT_FACE",FACE,{"disambiguationData":[OSD([subQ0]),TDD([makeQuery(id+"F3.imprint","IMPRINT",EDGE,{"disambiguationData":[TD([[makeQuery(id+"F3.imprint","INTERSECT",VERTEX,{"derivedFrom":[subQ0,sQuery(id+"F3.wireOp",EDGE,"E59")]}),-1.0]])],"derivedFrom":subQ0})])]}),makeQuery(id+"F5.opExtrude","SWEPT_FACE",FACE,{"disambiguationData":[OSD([subQ0]),TDD([makeQuery(id+"F3.imprint","IMPRINT",EDGE,{"disambiguationData":[TD([[makeQuery(id+"F3.imprint","INTERSECT",VERTEX,{"derivedFrom":[subQ0,sQuery(id+"F3.wireOp",EDGE,"E65.trimOffspring")]}),-1.0]])],"derivedFrom":subQ0})])]})]}),makeQuery(id+"F6.opExtrude","SWEPT_FACE",FACE,{"disambiguationData":[OSD([subQ0]),TDD([makeQuery(id+"F3.imprint","IMPRINT",EDGE,{"disambiguationData":[TD([[makeQuery(id+"F3.imprint","INTERSECT",VERTEX,{"derivedFrom":[subQ0,sQuery(id+"F3.wireOp",EDGE,"E57")]}),-1.0]])],"derivedFrom":subQ0})])]}),makeQuery(id+"F6.opExtrude","SWEPT_FACE",FACE,{"disambiguationData":[OSD([subQ0]),TDD([makeQuery(id+"F3.imprint","IMPRINT",EDGE,{"disambiguationData":[TD([[makeQuery(id+"F3.imprint","INTERSECT",VERTEX,{"derivedFrom":[subQ0,sQuery(id+"F3.wireOp",EDGE,"E67.trimOffspring")]}),-1.0]])],"derivedFrom":subQ0})])]})]}),makeQuery(id+"F21.opExtrude","SWEPT_FACE",FACE,{"disambiguationData":[OSD([sQuery(id+"F19.wireOp",EDGE,"E137")])]})]});}
            var Q18;
            {var subQ0=sQuery(id+"F3.wireOp",EDGE,"E14");var subQ1=sQuery(id+"F0.wireOp",EDGE,"E0");Q18=makeQuery(id+"F20.boolean.opBoolean","INTERSECT",EDGE,{"disambiguationData":[OD(1.0)],"derivedFrom":[makeQuery(id+"F6.boolean.opBoolean","MERGE",FACE,{"derivedFrom":[makeQuery(id+"F5.boolean.opBoolean","MERGE",FACE,{"derivedFrom":[makeQuery(id+"F4.boolean.opBoolean","MERGE",FACE,{"derivedFrom":[makeQuery(id+"F2.boolean.opBoolean","MERGE",FACE,{"derivedFrom":[makeQuery(id+"F1.opExtrude","SWEPT_FACE",FACE,{"disambiguationData":[OSD([subQ1])]}),makeQuery(id+"F2.opExtrude","SWEPT_FACE",FACE,{"disambiguationData":[OSD([subQ1])]})]}),makeQuery(id+"F4.opExtrude","SWEPT_FACE",FACE,{"disambiguationData":[OSD([subQ0]),TDD([makeQuery(id+"F3.imprint","IMPRINT",EDGE,{"disambiguationData":[TD([[makeQuery(id+"F3.imprint","INTERSECT",VERTEX,{"derivedFrom":[subQ0,sQuery(id+"F3.wireOp",EDGE,"E71.trimOffspring")]}),-1.0]])],"derivedFrom":subQ0})])]}),makeQuery(id+"F4.opExtrude","SWEPT_FACE",FACE,{"disambiguationData":[OSD([subQ0]),TDD([makeQuery(id+"F3.imprint","IMPRINT",EDGE,{"disambiguationData":[TD([[makeQuery(id+"F3.imprint","INTERSECT",VERTEX,{"derivedFrom":[subQ0,sQuery(id+"F3.wireOp",EDGE,"E53")]}),-1.0]])],"derivedFrom":subQ0})])]}),makeQuery(id+"F4.opExtrude","SWEPT_FACE",FACE,{"disambiguationData":[OSD([subQ0]),TDD([makeQuery(id+"F3.imprint","IMPRINT",EDGE,{"disambiguationData":[TD([[makeQuery(id+"F3.imprint","INTERSECT",VERTEX,{"derivedFrom":[subQ0,sQuery(id+"F3.wireOp",EDGE,"E61")]}),-1.0]])],"derivedFrom":subQ0})])]}),makeQuery(id+"F4.opExtrude","SWEPT_FACE",FACE,{"disambiguationData":[OSD([subQ0]),TDD([makeQuery(id+"F3.imprint","IMPRINT",EDGE,{"disambiguationData":[TD([[makeQuery(id+"F3.imprint","INTERSECT",VERTEX,{"derivedFrom":[subQ0,sQuery(id+"F3.wireOp",EDGE,"E63.trimOffspring")]}),-1.0]])],"derivedFrom":subQ0})])]})]}),makeQuery(id+"F5.opExtrude","SWEPT_FACE",FACE,{"disambiguationData":[OSD([subQ0]),TDD([makeQuery(id+"F3.imprint","IMPRINT",EDGE,{"disambiguationData":[TD([[makeQuery(id+"F3.imprint","INTERSECT",VERTEX,{"derivedFrom":[subQ0,sQuery(id+"F3.wireOp",EDGE,"E69.trimOffspring")]}),-1.0]])],"derivedFrom":subQ0})])]}),makeQuery(id+"F5.opExtrude","SWEPT_FACE",FACE,{"disambiguationData":[OSD([subQ0]),TDD([makeQuery(id+"F3.imprint","IMPRINT",EDGE,{"disambiguationData":[TD([[makeQuery(id+"F3.imprint","INTERSECT",VERTEX,{"derivedFrom":[subQ0,sQuery(id+"F3.wireOp",EDGE,"E55")]}),-1.0]])],"derivedFrom":subQ0})])]}),makeQuery(id+"F5.opExtrude","SWEPT_FACE",FACE,{"disambiguationData":[OSD([subQ0]),TDD([makeQuery(id+"F3.imprint","IMPRINT",EDGE,{"disambiguationData":[TD([[makeQuery(id+"F3.imprint","INTERSECT",VERTEX,{"derivedFrom":[subQ0,sQuery(id+"F3.wireOp",EDGE,"E59")]}),-1.0]])],"derivedFrom":subQ0})])]}),makeQuery(id+"F5.opExtrude","SWEPT_FACE",FACE,{"disambiguationData":[OSD([subQ0]),TDD([makeQuery(id+"F3.imprint","IMPRINT",EDGE,{"disambiguationData":[TD([[makeQuery(id+"F3.imprint","INTERSECT",VERTEX,{"derivedFrom":[subQ0,sQuery(id+"F3.wireOp",EDGE,"E65.trimOffspring")]}),-1.0]])],"derivedFrom":subQ0})])]})]}),makeQuery(id+"F6.opExtrude","SWEPT_FACE",FACE,{"disambiguationData":[OSD([subQ0]),TDD([makeQuery(id+"F3.imprint","IMPRINT",EDGE,{"disambiguationData":[TD([[makeQuery(id+"F3.imprint","INTERSECT",VERTEX,{"derivedFrom":[subQ0,sQuery(id+"F3.wireOp",EDGE,"E57")]}),-1.0]])],"derivedFrom":subQ0})])]}),makeQuery(id+"F6.opExtrude","SWEPT_FACE",FACE,{"disambiguationData":[OSD([subQ0]),TDD([makeQuery(id+"F3.imprint","IMPRINT",EDGE,{"disambiguationData":[TD([[makeQuery(id+"F3.imprint","INTERSECT",VERTEX,{"derivedFrom":[subQ0,sQuery(id+"F3.wireOp",EDGE,"E67.trimOffspring")]}),-1.0]])],"derivedFrom":subQ0})])]})]}),makeQuery(id+"F20.opExtrude","SWEPT_FACE",FACE,{"disambiguationData":[OSD([sQuery(id+"F18.wireOp",EDGE,"E134")])]})]});}
            var Q19;
            {var subQ0=sQuery(id+"F3.wireOp",EDGE,"E14");var subQ1=sQuery(id+"F0.wireOp",EDGE,"E0");Q19=makeQuery(id+"F20.boolean.opBoolean","INTERSECT",EDGE,{"disambiguationData":[OD(1.0)],"derivedFrom":[makeQuery(id+"F6.boolean.opBoolean","MERGE",FACE,{"derivedFrom":[makeQuery(id+"F5.boolean.opBoolean","MERGE",FACE,{"derivedFrom":[makeQuery(id+"F4.boolean.opBoolean","MERGE",FACE,{"derivedFrom":[makeQuery(id+"F2.boolean.opBoolean","MERGE",FACE,{"derivedFrom":[makeQuery(id+"F1.opExtrude","SWEPT_FACE",FACE,{"disambiguationData":[OSD([subQ1])]}),makeQuery(id+"F2.opExtrude","SWEPT_FACE",FACE,{"disambiguationData":[OSD([subQ1])]})]}),makeQuery(id+"F4.opExtrude","SWEPT_FACE",FACE,{"disambiguationData":[OSD([subQ0]),TDD([makeQuery(id+"F3.imprint","IMPRINT",EDGE,{"disambiguationData":[TD([[makeQuery(id+"F3.imprint","INTERSECT",VERTEX,{"derivedFrom":[subQ0,sQuery(id+"F3.wireOp",EDGE,"E71.trimOffspring")]}),-1.0]])],"derivedFrom":subQ0})])]}),makeQuery(id+"F4.opExtrude","SWEPT_FACE",FACE,{"disambiguationData":[OSD([subQ0]),TDD([makeQuery(id+"F3.imprint","IMPRINT",EDGE,{"disambiguationData":[TD([[makeQuery(id+"F3.imprint","INTERSECT",VERTEX,{"derivedFrom":[subQ0,sQuery(id+"F3.wireOp",EDGE,"E53")]}),-1.0]])],"derivedFrom":subQ0})])]}),makeQuery(id+"F4.opExtrude","SWEPT_FACE",FACE,{"disambiguationData":[OSD([subQ0]),TDD([makeQuery(id+"F3.imprint","IMPRINT",EDGE,{"disambiguationData":[TD([[makeQuery(id+"F3.imprint","INTERSECT",VERTEX,{"derivedFrom":[subQ0,sQuery(id+"F3.wireOp",EDGE,"E61")]}),-1.0]])],"derivedFrom":subQ0})])]}),makeQuery(id+"F4.opExtrude","SWEPT_FACE",FACE,{"disambiguationData":[OSD([subQ0]),TDD([makeQuery(id+"F3.imprint","IMPRINT",EDGE,{"disambiguationData":[TD([[makeQuery(id+"F3.imprint","INTERSECT",VERTEX,{"derivedFrom":[subQ0,sQuery(id+"F3.wireOp",EDGE,"E63.trimOffspring")]}),-1.0]])],"derivedFrom":subQ0})])]})]}),makeQuery(id+"F5.opExtrude","SWEPT_FACE",FACE,{"disambiguationData":[OSD([subQ0]),TDD([makeQuery(id+"F3.imprint","IMPRINT",EDGE,{"disambiguationData":[TD([[makeQuery(id+"F3.imprint","INTERSECT",VERTEX,{"derivedFrom":[subQ0,sQuery(id+"F3.wireOp",EDGE,"E69.trimOffspring")]}),-1.0]])],"derivedFrom":subQ0})])]}),makeQuery(id+"F5.opExtrude","SWEPT_FACE",FACE,{"disambiguationData":[OSD([subQ0]),TDD([makeQuery(id+"F3.imprint","IMPRINT",EDGE,{"disambiguationData":[TD([[makeQuery(id+"F3.imprint","INTERSECT",VERTEX,{"derivedFrom":[subQ0,sQuery(id+"F3.wireOp",EDGE,"E55")]}),-1.0]])],"derivedFrom":subQ0})])]}),makeQuery(id+"F5.opExtrude","SWEPT_FACE",FACE,{"disambiguationData":[OSD([subQ0]),TDD([makeQuery(id+"F3.imprint","IMPRINT",EDGE,{"disambiguationData":[TD([[makeQuery(id+"F3.imprint","INTERSECT",VERTEX,{"derivedFrom":[subQ0,sQuery(id+"F3.wireOp",EDGE,"E59")]}),-1.0]])],"derivedFrom":subQ0})])]}),makeQuery(id+"F5.opExtrude","SWEPT_FACE",FACE,{"disambiguationData":[OSD([subQ0]),TDD([makeQuery(id+"F3.imprint","IMPRINT",EDGE,{"disambiguationData":[TD([[makeQuery(id+"F3.imprint","INTERSECT",VERTEX,{"derivedFrom":[subQ0,sQuery(id+"F3.wireOp",EDGE,"E65.trimOffspring")]}),-1.0]])],"derivedFrom":subQ0})])]})]}),makeQuery(id+"F6.opExtrude","SWEPT_FACE",FACE,{"disambiguationData":[OSD([subQ0]),TDD([makeQuery(id+"F3.imprint","IMPRINT",EDGE,{"disambiguationData":[TD([[makeQuery(id+"F3.imprint","INTERSECT",VERTEX,{"derivedFrom":[subQ0,sQuery(id+"F3.wireOp",EDGE,"E57")]}),-1.0]])],"derivedFrom":subQ0})])]}),makeQuery(id+"F6.opExtrude","SWEPT_FACE",FACE,{"disambiguationData":[OSD([subQ0]),TDD([makeQuery(id+"F3.imprint","IMPRINT",EDGE,{"disambiguationData":[TD([[makeQuery(id+"F3.imprint","INTERSECT",VERTEX,{"derivedFrom":[subQ0,sQuery(id+"F3.wireOp",EDGE,"E67.trimOffspring")]}),-1.0]])],"derivedFrom":subQ0})])]})]}),makeQuery(id+"F20.opExtrude","SWEPT_FACE",FACE,{"disambiguationData":[OSD([sQuery(id+"F18.wireOp",EDGE,"E135")])]})]});}
            chamfer(context, id + "F25", {"entities" : qUnion([Q0, Q1, Q2, Q3, Q4, Q5, Q6, Q7, Q8, Q9, Q10, Q11, Q12, Q13, Q14, Q15, Q16, Q17, Q18, Q19]), "width" : .5 * mm, "tangentPropagation" : true});
        }
        {
            var Q0;
            {var subQ1=sQuery(id+"F3.wireOp",EDGE,"E64.trimOffspring");var subQ2=makeQuery(id+"F4.opExtrude","SWEPT_FACE",FACE,{"disambiguationData":[OSD([subQ1])]});var subQ8=sQuery(id+"F0.wireOp",EDGE,"E10");Q0=makeQuery(id+"F5.boolean.opBoolean","SPLIT",EDGE,{"disambiguationData":[TD([subQ2])],"derivedFrom":makeQuery(id+"F4.boolean.opBoolean","SPLIT",EDGE,{"disambiguationData":[TD([subQ2])],"derivedFrom":makeQuery(id+"F2.opExtrude","CAP_EDGE",EDGE,{"disambiguationData":[OSD([subQ8])],"isStart":false})})});}
            var Q1;
            {var subQ4=sQuery(id+"F3.wireOp",EDGE,"E64.trimOffspring");var subQ9=sQuery(id+"F0.wireOp",EDGE,"E10");var subQ17=sQuery(id+"F3.wireOp",EDGE,"E66.trimOffspring");var subQ18=makeQuery(id+"F5.opExtrude","SWEPT_FACE",FACE,{"disambiguationData":[OSD([subQ17])]});Q1=makeQuery(id+"F6.boolean.opBoolean","SPLIT",EDGE,{"disambiguationData":[TD([subQ18])],"derivedFrom":makeQuery(id+"F5.boolean.opBoolean","SPLIT",EDGE,{"disambiguationData":[TD([subQ18])],"derivedFrom":makeQuery(id+"F4.boolean.opBoolean","SPLIT",EDGE,{"disambiguationData":[TD([makeQuery(id+"F4.opExtrude","SWEPT_FACE",FACE,{"disambiguationData":[OSD([subQ4])]})])],"derivedFrom":makeQuery(id+"F2.opExtrude","CAP_EDGE",EDGE,{"disambiguationData":[OSD([subQ9])],"isStart":false})})})});}
            var Q2;
            {var subQ0=sQuery(id+"F0.wireOp",EDGE,"E10");var subQ3=sQuery(id+"F3.wireOp",EDGE,"E62");Q2=makeQuery(id+"F4.boolean.opBoolean","SPLIT",EDGE,{"disambiguationData":[TD([makeQuery(id+"F4.opExtrude","SWEPT_FACE",FACE,{"disambiguationData":[OSD([subQ3])]})])],"derivedFrom":makeQuery(id+"F2.opExtrude","CAP_EDGE",EDGE,{"disambiguationData":[OSD([subQ0])],"isStart":false})});}
            var Q3;
            {var subQ2=sQuery(id+"F3.wireOp",EDGE,"E69.trimOffspring");var subQ4=sQuery(id+"F3.wireOp",EDGE,"E64.trimOffspring");var subQ9=sQuery(id+"F0.wireOp",EDGE,"E10");var subQ18=sQuery(id+"F3.wireOp",EDGE,"E66.trimOffspring");var subQ20=makeQuery(id+"F5.opExtrude","SWEPT_FACE",FACE,{"disambiguationData":[OSD([subQ2])]});Q3=makeQuery(id+"F6.boolean.opBoolean","SPLIT",EDGE,{"disambiguationData":[TD([subQ20])],"derivedFrom":makeQuery(id+"F5.boolean.opBoolean","SPLIT",EDGE,{"disambiguationData":[TD([makeQuery(id+"F5.opExtrude","SWEPT_FACE",FACE,{"disambiguationData":[OSD([subQ18])]})])],"derivedFrom":makeQuery(id+"F4.boolean.opBoolean","SPLIT",EDGE,{"disambiguationData":[TD([makeQuery(id+"F4.opExtrude","SWEPT_FACE",FACE,{"disambiguationData":[OSD([subQ4])]})])],"derivedFrom":makeQuery(id+"F2.opExtrude","CAP_EDGE",EDGE,{"disambiguationData":[OSD([subQ9])],"isStart":false})})})});}
            var Q4;
            {var subQ2=sQuery(id+"F3.wireOp",EDGE,"E71.trimOffspring");var subQ3=makeQuery(id+"F4.opExtrude","SWEPT_FACE",FACE,{"disambiguationData":[OSD([subQ2])]});var subQ4=sQuery(id+"F3.wireOp",EDGE,"E64.trimOffspring");var subQ9=sQuery(id+"F0.wireOp",EDGE,"E10");Q4=makeQuery(id+"F5.boolean.opBoolean","SPLIT",EDGE,{"disambiguationData":[TD([subQ3])],"derivedFrom":makeQuery(id+"F4.boolean.opBoolean","SPLIT",EDGE,{"disambiguationData":[TD([makeQuery(id+"F4.opExtrude","SWEPT_FACE",FACE,{"disambiguationData":[OSD([subQ4])]})])],"derivedFrom":makeQuery(id+"F2.opExtrude","CAP_EDGE",EDGE,{"disambiguationData":[OSD([subQ9])],"isStart":false})})});}
            var Q5;
            {var subQ0=sQuery(id+"F0.wireOp",EDGE,"E10");var subQ5=sQuery(id+"F3.wireOp",EDGE,"E53");Q5=makeQuery(id+"F4.boolean.opBoolean","SPLIT",EDGE,{"disambiguationData":[TD([makeQuery(id+"F4.opExtrude","SWEPT_FACE",FACE,{"disambiguationData":[OSD([subQ5])]})])],"derivedFrom":makeQuery(id+"F2.opExtrude","CAP_EDGE",EDGE,{"disambiguationData":[OSD([subQ0])],"isStart":false})});}
            var Q6;
            {var subQ4=sQuery(id+"F3.wireOp",EDGE,"E54");var subQ7=sQuery(id+"F0.wireOp",EDGE,"E10");var subQ11=makeQuery(id+"F4.opExtrude","SWEPT_FACE",FACE,{"disambiguationData":[OSD([subQ4])]});Q6=makeQuery(id+"F5.boolean.opBoolean","SPLIT",EDGE,{"disambiguationData":[TD([subQ11])],"derivedFrom":makeQuery(id+"F4.boolean.opBoolean","SPLIT",EDGE,{"disambiguationData":[TD([subQ11])],"derivedFrom":makeQuery(id+"F2.opExtrude","CAP_EDGE",EDGE,{"disambiguationData":[OSD([subQ7])],"isStart":false})})});}
            var Q7;
            {var subQ1=sQuery(id+"F3.wireOp",EDGE,"E56");var subQ7=sQuery(id+"F3.wireOp",EDGE,"E54");var subQ10=sQuery(id+"F0.wireOp",EDGE,"E10");var subQ14=makeQuery(id+"F5.opExtrude","SWEPT_FACE",FACE,{"disambiguationData":[OSD([subQ1])]});Q7=makeQuery(id+"F6.boolean.opBoolean","SPLIT",EDGE,{"disambiguationData":[TD([subQ14])],"derivedFrom":makeQuery(id+"F5.boolean.opBoolean","SPLIT",EDGE,{"disambiguationData":[TD([subQ14])],"derivedFrom":makeQuery(id+"F4.boolean.opBoolean","SPLIT",EDGE,{"disambiguationData":[TD([makeQuery(id+"F4.opExtrude","SWEPT_FACE",FACE,{"disambiguationData":[OSD([subQ7])]})])],"derivedFrom":makeQuery(id+"F2.opExtrude","CAP_EDGE",EDGE,{"disambiguationData":[OSD([subQ10])],"isStart":false})})})});}
            var Q8;
            {var subQ1=sQuery(id+"F3.wireOp",EDGE,"E56");var subQ7=sQuery(id+"F3.wireOp",EDGE,"E54");var subQ9=sQuery(id+"F3.wireOp",EDGE,"E59");var subQ10=makeQuery(id+"F5.opExtrude","SWEPT_FACE",FACE,{"disambiguationData":[OSD([subQ9])]});var subQ12=sQuery(id+"F0.wireOp",EDGE,"E10");Q8=makeQuery(id+"F6.boolean.opBoolean","SPLIT",EDGE,{"disambiguationData":[TD([subQ10])],"derivedFrom":makeQuery(id+"F5.boolean.opBoolean","SPLIT",EDGE,{"disambiguationData":[TD([makeQuery(id+"F5.opExtrude","SWEPT_FACE",FACE,{"disambiguationData":[OSD([subQ1])]})])],"derivedFrom":makeQuery(id+"F4.boolean.opBoolean","SPLIT",EDGE,{"disambiguationData":[TD([makeQuery(id+"F4.opExtrude","SWEPT_FACE",FACE,{"disambiguationData":[OSD([subQ7])]})])],"derivedFrom":makeQuery(id+"F2.opExtrude","CAP_EDGE",EDGE,{"disambiguationData":[OSD([subQ12])],"isStart":false})})})});}
            var Q9;
            {var subQ1=sQuery(id+"F3.wireOp",EDGE,"E61");var subQ2=makeQuery(id+"F4.opExtrude","SWEPT_FACE",FACE,{"disambiguationData":[OSD([subQ1])]});var subQ6=sQuery(id+"F3.wireOp",EDGE,"E54");var subQ9=sQuery(id+"F0.wireOp",EDGE,"E10");Q9=makeQuery(id+"F5.boolean.opBoolean","SPLIT",EDGE,{"disambiguationData":[TD([subQ2])],"derivedFrom":makeQuery(id+"F4.boolean.opBoolean","SPLIT",EDGE,{"disambiguationData":[TD([makeQuery(id+"F4.opExtrude","SWEPT_FACE",FACE,{"disambiguationData":[OSD([subQ6])]})])],"derivedFrom":makeQuery(id+"F2.opExtrude","CAP_EDGE",EDGE,{"disambiguationData":[OSD([subQ9])],"isStart":false})})});}
            chamfer(context, id + "F26", {"entities" : qUnion([Q0, Q1, Q2, Q3, Q4, Q5, Q6, Q7, Q8, Q9]), "chamferType" : ChamferType.TWO_OFFSETS, "width1" : .5 * mm, "oppositeDirection" : false, "width2" : 1 * mm, "tangentPropagation" : true});
        }
        {
            var Q0;
            {var subQ4=sQuery(id+"F0.wireOp",EDGE,"E0");var subQ6=sQuery(id+"F3.wireOp",EDGE,"E54");var subQ8=sQuery(id+"F3.wireOp",EDGE,"E56");var subQ17=makeQuery(id+"F5.opExtrude","SWEPT_FACE",FACE,{"disambiguationData":[OSD([subQ8])]});Q0=makeQuery(id+"F6.boolean.opBoolean","SPLIT",EDGE,{"disambiguationData":[TD([subQ17])],"derivedFrom":makeQuery(id+"F5.boolean.opBoolean","SPLIT",EDGE,{"disambiguationData":[TD([subQ17])],"derivedFrom":makeQuery(id+"F4.boolean.opBoolean","SPLIT",EDGE,{"disambiguationData":[TD([makeQuery(id+"F4.opExtrude","SWEPT_FACE",FACE,{"disambiguationData":[OSD([subQ6])]})])],"derivedFrom":makeQuery(id+"F2.opExtrude","CAP_EDGE",EDGE,{"disambiguationData":[OSD([subQ4])],"isStart":false})})})});}
            var Q1;
            {var subQ2=sQuery(id+"F3.wireOp",EDGE,"E54");var subQ4=sQuery(id+"F0.wireOp",EDGE,"E0");var subQ8=makeQuery(id+"F4.opExtrude","SWEPT_FACE",FACE,{"disambiguationData":[OSD([subQ2])]});Q1=makeQuery(id+"F5.boolean.opBoolean","SPLIT",EDGE,{"disambiguationData":[TD([subQ8])],"derivedFrom":makeQuery(id+"F4.boolean.opBoolean","SPLIT",EDGE,{"disambiguationData":[TD([subQ8])],"derivedFrom":makeQuery(id+"F2.opExtrude","CAP_EDGE",EDGE,{"disambiguationData":[OSD([subQ4])],"isStart":false})})});}
            var Q2;
            {var subQ2=sQuery(id+"F3.wireOp",EDGE,"E59");var subQ4=sQuery(id+"F0.wireOp",EDGE,"E0");var subQ6=sQuery(id+"F3.wireOp",EDGE,"E54");var subQ8=sQuery(id+"F3.wireOp",EDGE,"E56");var subQ17=makeQuery(id+"F5.opExtrude","SWEPT_FACE",FACE,{"disambiguationData":[OSD([subQ2])]});Q2=makeQuery(id+"F6.boolean.opBoolean","SPLIT",EDGE,{"disambiguationData":[TD([subQ17])],"derivedFrom":makeQuery(id+"F5.boolean.opBoolean","SPLIT",EDGE,{"disambiguationData":[TD([makeQuery(id+"F5.opExtrude","SWEPT_FACE",FACE,{"disambiguationData":[OSD([subQ8])]})])],"derivedFrom":makeQuery(id+"F4.boolean.opBoolean","SPLIT",EDGE,{"disambiguationData":[TD([makeQuery(id+"F4.opExtrude","SWEPT_FACE",FACE,{"disambiguationData":[OSD([subQ6])]})])],"derivedFrom":makeQuery(id+"F2.opExtrude","CAP_EDGE",EDGE,{"disambiguationData":[OSD([subQ4])],"isStart":false})})})});}
            var Q3;
            {var subQ0=sQuery(id+"F3.wireOp",EDGE,"E61");var subQ1=makeQuery(id+"F4.opExtrude","SWEPT_FACE",FACE,{"disambiguationData":[OSD([subQ0])]});var subQ4=sQuery(id+"F3.wireOp",EDGE,"E54");var subQ6=sQuery(id+"F0.wireOp",EDGE,"E0");Q3=makeQuery(id+"F5.boolean.opBoolean","SPLIT",EDGE,{"disambiguationData":[TD([subQ1])],"derivedFrom":makeQuery(id+"F4.boolean.opBoolean","SPLIT",EDGE,{"disambiguationData":[TD([makeQuery(id+"F4.opExtrude","SWEPT_FACE",FACE,{"disambiguationData":[OSD([subQ4])]})])],"derivedFrom":makeQuery(id+"F2.opExtrude","CAP_EDGE",EDGE,{"disambiguationData":[OSD([subQ6])],"isStart":false})})});}
            var Q4;
            {var subQ0=sQuery(id+"F0.wireOp",EDGE,"E0");var subQ1=sQuery(id+"F3.wireOp",EDGE,"E62");Q4=makeQuery(id+"F4.boolean.opBoolean","SPLIT",EDGE,{"disambiguationData":[TD([makeQuery(id+"F4.opExtrude","SWEPT_FACE",FACE,{"disambiguationData":[OSD([subQ1])]})])],"derivedFrom":makeQuery(id+"F2.opExtrude","CAP_EDGE",EDGE,{"disambiguationData":[OSD([subQ0])],"isStart":false})});}
            var Q5;
            {var subQ0=sQuery(id+"F3.wireOp",EDGE,"E64.trimOffspring");var subQ1=makeQuery(id+"F4.opExtrude","SWEPT_FACE",FACE,{"disambiguationData":[OSD([subQ0])]});var subQ5=sQuery(id+"F0.wireOp",EDGE,"E0");Q5=makeQuery(id+"F5.boolean.opBoolean","SPLIT",EDGE,{"disambiguationData":[TD([subQ1])],"derivedFrom":makeQuery(id+"F4.boolean.opBoolean","SPLIT",EDGE,{"disambiguationData":[TD([subQ1])],"derivedFrom":makeQuery(id+"F2.opExtrude","CAP_EDGE",EDGE,{"disambiguationData":[OSD([subQ5])],"isStart":false})})});}
            var Q6;
            {var subQ1=sQuery(id+"F3.wireOp",EDGE,"E64.trimOffspring");var subQ4=sQuery(id+"F0.wireOp",EDGE,"E0");var subQ16=sQuery(id+"F3.wireOp",EDGE,"E66.trimOffspring");var subQ18=makeQuery(id+"F5.opExtrude","SWEPT_FACE",FACE,{"disambiguationData":[OSD([subQ16])]});Q6=makeQuery(id+"F6.boolean.opBoolean","SPLIT",EDGE,{"disambiguationData":[TD([subQ18])],"derivedFrom":makeQuery(id+"F5.boolean.opBoolean","SPLIT",EDGE,{"disambiguationData":[TD([subQ18])],"derivedFrom":makeQuery(id+"F4.boolean.opBoolean","SPLIT",EDGE,{"disambiguationData":[TD([makeQuery(id+"F4.opExtrude","SWEPT_FACE",FACE,{"disambiguationData":[OSD([subQ1])]})])],"derivedFrom":makeQuery(id+"F2.opExtrude","CAP_EDGE",EDGE,{"disambiguationData":[OSD([subQ4])],"isStart":false})})})});}
            var Q7;
            {var subQ0=sQuery(id+"F0.wireOp",EDGE,"E0");var subQ3=sQuery(id+"F3.wireOp",EDGE,"E53");Q7=makeQuery(id+"F4.boolean.opBoolean","SPLIT",EDGE,{"disambiguationData":[TD([makeQuery(id+"F4.opExtrude","SWEPT_FACE",FACE,{"disambiguationData":[OSD([subQ3])]})])],"derivedFrom":makeQuery(id+"F2.opExtrude","CAP_EDGE",EDGE,{"disambiguationData":[OSD([subQ0])],"isStart":false})});}
            var Q8;
            {var subQ1=sQuery(id+"F3.wireOp",EDGE,"E64.trimOffspring");var subQ4=sQuery(id+"F0.wireOp",EDGE,"E0");var subQ6=sQuery(id+"F3.wireOp",EDGE,"E71.trimOffspring");var subQ7=makeQuery(id+"F4.opExtrude","SWEPT_FACE",FACE,{"disambiguationData":[OSD([subQ6])]});Q8=makeQuery(id+"F5.boolean.opBoolean","SPLIT",EDGE,{"disambiguationData":[TD([subQ7])],"derivedFrom":makeQuery(id+"F4.boolean.opBoolean","SPLIT",EDGE,{"disambiguationData":[TD([makeQuery(id+"F4.opExtrude","SWEPT_FACE",FACE,{"disambiguationData":[OSD([subQ1])]})])],"derivedFrom":makeQuery(id+"F2.opExtrude","CAP_EDGE",EDGE,{"disambiguationData":[OSD([subQ4])],"isStart":false})})});}
            var Q9;
            {var subQ1=sQuery(id+"F3.wireOp",EDGE,"E64.trimOffspring");var subQ4=sQuery(id+"F0.wireOp",EDGE,"E0");var subQ13=sQuery(id+"F3.wireOp",EDGE,"E69.trimOffspring");var subQ16=sQuery(id+"F3.wireOp",EDGE,"E66.trimOffspring");var subQ18=makeQuery(id+"F5.opExtrude","SWEPT_FACE",FACE,{"disambiguationData":[OSD([subQ13])]});Q9=makeQuery(id+"F6.boolean.opBoolean","SPLIT",EDGE,{"disambiguationData":[TD([subQ18])],"derivedFrom":makeQuery(id+"F5.boolean.opBoolean","SPLIT",EDGE,{"disambiguationData":[TD([makeQuery(id+"F5.opExtrude","SWEPT_FACE",FACE,{"disambiguationData":[OSD([subQ16])]})])],"derivedFrom":makeQuery(id+"F4.boolean.opBoolean","SPLIT",EDGE,{"disambiguationData":[TD([makeQuery(id+"F4.opExtrude","SWEPT_FACE",FACE,{"disambiguationData":[OSD([subQ1])]})])],"derivedFrom":makeQuery(id+"F2.opExtrude","CAP_EDGE",EDGE,{"disambiguationData":[OSD([subQ4])],"isStart":false})})})});}
            chamfer(context, id + "F27", {"entities" : qUnion([Q0, Q1, Q2, Q3, Q4, Q5, Q6, Q7, Q8, Q9]), "chamferType" : ChamferType.TWO_OFFSETS, "width1" : 1 * mm, "oppositeDirection" : false, "width2" : .5 * mm, "tangentPropagation" : true});
        }
        {
            var Q0;
            {var subQ0=sQuery(id+"F0.wireOp",EDGE,"E12");var subQ1=sQuery(id+"F0.wireOp",EDGE,"E11");var subQ2=sQuery(id+"F0.wireOp",EDGE,"E10");var subQ3=makeQuery(id+"F0.imprint","INTERSECT",VERTEX,{"disambiguationData":[OD(1.0)],"derivedFrom":[sQuery(id+"F0.wireOp",EDGE,"E2"),subQ0]});var subQ4=makeQuery(id+"F0.imprint","IMPRINT",EDGE,{"disambiguationData":[TD([[subQ3,-1.0]])],"derivedFrom":subQ0});var subQ5=makeQuery(id+"F0.imprint","IMPRINT",EDGE,{"disambiguationData":[TD([[makeQuery(id+"F0.imprint","INTERSECT",VERTEX,{"disambiguationData":[OD(0.0)],"derivedFrom":[subQ2,subQ0]}),-1.0]])],"derivedFrom":subQ0});Q0=makeQuery(id+"F2.boolean.opBoolean","SPLIT",EDGE,{"disambiguationData":[topologyDisambiguationEdgeConnected([makeQuery(id+"F1.opExtrude","CAP_FACE",FACE,{"disambiguationData":[OSD([sQuery(id+"F0.wireOp",EDGE,"E0"),subQ2,subQ1,subQ0,sQuery(id+"F0.wireOp",EDGE,"E13")])],"isStart":true})])],"derivedFrom":makeQuery(id+"F1.opExtrude","CAP_EDGE",EDGE,{"disambiguationData":[OSD([subQ0]),TDD([subQ5,subQ4])],"isStart":true})});}
            var Q1;
            {var subQ0=sQuery(id+"F0.wireOp",EDGE,"E13");var subQ1=sQuery(id+"F0.wireOp",EDGE,"E11");var subQ2=sQuery(id+"F0.wireOp",EDGE,"E10");var subQ3=makeQuery(id+"F0.imprint","INTERSECT",VERTEX,{"disambiguationData":[OD(1.0)],"derivedFrom":[sQuery(id+"F0.wireOp",EDGE,"E2"),subQ0]});var subQ4=makeQuery(id+"F0.imprint","IMPRINT",EDGE,{"disambiguationData":[TD([[subQ3,-1.0]])],"derivedFrom":subQ0});var subQ5=makeQuery(id+"F0.imprint","IMPRINT",EDGE,{"disambiguationData":[TD([[makeQuery(id+"F0.imprint","INTERSECT",VERTEX,{"disambiguationData":[OD(0.0)],"derivedFrom":[subQ2,subQ0]}),-1.0]])],"derivedFrom":subQ0});Q1=makeQuery(id+"F2.boolean.opBoolean","SPLIT",EDGE,{"disambiguationData":[topologyDisambiguationEdgeConnected([makeQuery(id+"F1.opExtrude","CAP_FACE",FACE,{"disambiguationData":[OSD([sQuery(id+"F0.wireOp",EDGE,"E0"),subQ2,subQ1,sQuery(id+"F0.wireOp",EDGE,"E12"),subQ0])],"isStart":true})])],"derivedFrom":makeQuery(id+"F1.opExtrude","CAP_EDGE",EDGE,{"disambiguationData":[OSD([subQ0]),TDD([subQ5,subQ4])],"isStart":true})});}
            var Q2;
            {var subQ0=sQuery(id+"F0.wireOp",EDGE,"E12");var subQ1=sQuery(id+"F0.wireOp",EDGE,"E11");var subQ2=sQuery(id+"F0.wireOp",EDGE,"E10");var subQ3=makeQuery(id+"F0.imprint","INTERSECT",VERTEX,{"disambiguationData":[OD(0.0)],"derivedFrom":[sQuery(id+"F0.wireOp",EDGE,"E2"),subQ0]});var subQ4=makeQuery(id+"F0.imprint","IMPRINT",EDGE,{"disambiguationData":[TD([[makeQuery(id+"F0.imprint","INTERSECT",VERTEX,{"disambiguationData":[OD(1.0)],"derivedFrom":[subQ2,subQ0]}),1.0]])],"derivedFrom":subQ0});var subQ5=makeQuery(id+"F0.imprint","IMPRINT",EDGE,{"disambiguationData":[TD([[subQ3,1.0]])],"derivedFrom":subQ0});Q2=makeQuery(id+"F2.boolean.opBoolean","SPLIT",EDGE,{"disambiguationData":[topologyDisambiguationEdgeConnected([makeQuery(id+"F1.opExtrude","CAP_FACE",FACE,{"disambiguationData":[OSD([sQuery(id+"F0.wireOp",EDGE,"E0"),subQ2,subQ1,subQ0,sQuery(id+"F0.wireOp",EDGE,"E13")])],"isStart":true})])],"derivedFrom":makeQuery(id+"F1.opExtrude","CAP_EDGE",EDGE,{"disambiguationData":[OSD([subQ0]),TDD([subQ5,subQ4])],"isStart":true})});}
            var Q3;
            {var subQ0=sQuery(id+"F0.wireOp",EDGE,"E13");var subQ1=sQuery(id+"F0.wireOp",EDGE,"E11");var subQ2=sQuery(id+"F0.wireOp",EDGE,"E10");var subQ3=makeQuery(id+"F0.imprint","INTERSECT",VERTEX,{"disambiguationData":[OD(0.0)],"derivedFrom":[sQuery(id+"F0.wireOp",EDGE,"E2"),subQ0]});var subQ4=makeQuery(id+"F0.imprint","IMPRINT",EDGE,{"disambiguationData":[TD([[makeQuery(id+"F0.imprint","INTERSECT",VERTEX,{"disambiguationData":[OD(1.0)],"derivedFrom":[subQ2,subQ0]}),1.0]])],"derivedFrom":subQ0});var subQ5=makeQuery(id+"F0.imprint","IMPRINT",EDGE,{"disambiguationData":[TD([[subQ3,1.0]])],"derivedFrom":subQ0});Q3=makeQuery(id+"F2.boolean.opBoolean","SPLIT",EDGE,{"disambiguationData":[topologyDisambiguationEdgeConnected([makeQuery(id+"F1.opExtrude","CAP_FACE",FACE,{"disambiguationData":[OSD([sQuery(id+"F0.wireOp",EDGE,"E0"),subQ2,subQ1,sQuery(id+"F0.wireOp",EDGE,"E12"),subQ0])],"isStart":true})])],"derivedFrom":makeQuery(id+"F1.opExtrude","CAP_EDGE",EDGE,{"disambiguationData":[OSD([subQ0]),TDD([subQ5,subQ4])],"isStart":true})});}
            fillet(context, id + "F28", {"entities" : qUnion([Q0, Q1, Q2, Q3]), "radius" : 1.25 * mm, "tangentPropagation" : true, "allowEdgeOverflow" : false});
        }
        {
            var Q0;
            Q0=makeQuery(id+"F2.opExtrude","CAP_EDGE",EDGE,{"disambiguationData":[OSD([sQuery(id+"F0.wireOp",EDGE,"E2")])],"isStart":false});
            chamfer(context, id + "F29", {"entities" : qUnion([Q0]), "width" : .25 * mm, "tangentPropagation" : true});
        }
        {
            var Q0;
            Q0=makeQuery(id+"F1.opExtrude","CAP_FACE",FACE,{"disambiguationData":[OSD([sQuery(id+"F0.wireOp",EDGE,"E0"),sQuery(id+"F0.wireOp",EDGE,"E10"),sQuery(id+"F0.wireOp",EDGE,"E11"),sQuery(id+"F0.wireOp",EDGE,"E12"),sQuery(id+"F0.wireOp",EDGE,"E13")])],"isStart":false});
            var sketch = newSketch(context, id + "F30", { "sketchPlane" : qUnion([Q0])});
            skLineSegment(sketch, "E145", {"start": v(0, 0) * mm, "end": v(1.25, 0) * mm});
            skLineSegment(sketch, "E146", {"start": v(1.25, 0) * mm, "end": v(1.25, 13.5) * mm});
            skLineSegment(sketch, "E147", {"start": v(1.25, 13.5) * mm, "end": v(-1.25, 13.5) * mm});
            skLineSegment(sketch, "E148", {"start": v(-1.25, 13.5) * mm, "end": v(-1.25, 0) * mm});
            skLineSegment(sketch, "E149", {"start": v(-1.25, 0) * mm, "end": v(-1.25, -13.5) * mm});
            skLineSegment(sketch, "E150", {"start": v(-1.25, -13.5) * mm, "end": v(1.25, -13.5) * mm});
            skLineSegment(sketch, "E151", {"start": v(1.25, -13.5) * mm, "end": v(1.25, 0) * mm});
            skLineSegment(sketch, "E152", {"start": v(0, 0) * mm, "end": v(-1.25, 0) * mm});
            skSolve(sketch);
        }
        {
            var Q0;
            {var subQ0=sQuery(id+"F30.wireOp",EDGE,"E150");Q0=makeQuery(id+"F30.imprint","IMPRINT",FACE,{"disambiguationData":[TD([[makeQuery(id+"F30.imprint","IMPRINT",EDGE,{"derivedFrom":subQ0}),1.0]])]});}
            var Q1;
            {var subQ0=sQuery(id+"F30.wireOp",EDGE,"E147");Q1=makeQuery(id+"F30.imprint","IMPRINT",FACE,{"disambiguationData":[TD([[makeQuery(id+"F30.imprint","IMPRINT",EDGE,{"derivedFrom":subQ0}),1.0]])]});}
            extrude(context, id + "F31", {"entities" : qUnion([Q0, Q1]), "operationType" : NewBodyOperationType.ADD, "oppositeDirection" : true, "depth" : 3 * mm, "offsetDistance" : 25 * mm});
        }
        {
            var Q0;
            Q0=makeQuery(id+"F31.opExtrude","CAP_EDGE",EDGE,{"disambiguationData":[OSD([sQuery(id+"F30.wireOp",EDGE,"E151")])],"isStart":false});
            var Q1;
            Q1=makeQuery(id+"F31.opExtrude","CAP_EDGE",EDGE,{"disambiguationData":[OSD([sQuery(id+"F30.wireOp",EDGE,"E149")])],"isStart":false});
            var Q2;
            Q2=makeQuery(id+"F31.opExtrude","CAP_EDGE",EDGE,{"disambiguationData":[OSD([sQuery(id+"F30.wireOp",EDGE,"E146")])],"isStart":false});
            var Q3;
            Q3=makeQuery(id+"F31.opExtrude","CAP_EDGE",EDGE,{"disambiguationData":[OSD([sQuery(id+"F30.wireOp",EDGE,"E148")])],"isStart":false});
            fillet(context, id + "F32", {"entities" : qUnion([Q0, Q1, Q2, Q3]), "radius" : 1.25 * mm, "tangentPropagation" : true, "allowEdgeOverflow" : false});
        }
        {
            var Q0;
            {var subQ0=sQuery(id+"F0.wireOp",EDGE,"E12");var subQ1=sQuery(id+"F0.wireOp",EDGE,"E10");Q0=makeQuery(id+"F1.opExtrude","CAP_EDGE",EDGE,{"disambiguationData":[OSD([subQ1]),TDD([makeQuery(id+"F0.imprint","IMPRINT",EDGE,{"disambiguationData":[TD([[makeQuery(id+"F0.imprint","INTERSECT",VERTEX,{"disambiguationData":[OD(0.0)],"derivedFrom":[subQ1,subQ0]}),1.0]])],"derivedFrom":subQ1})])],"isStart":false});}
            var Q1;
            {var subQ0=sQuery(id+"F0.wireOp",EDGE,"E13");var subQ1=sQuery(id+"F0.wireOp",EDGE,"E10");Q1=makeQuery(id+"F1.opExtrude","CAP_EDGE",EDGE,{"disambiguationData":[OSD([subQ1]),TDD([makeQuery(id+"F0.imprint","IMPRINT",EDGE,{"disambiguationData":[TD([[makeQuery(id+"F0.imprint","INTERSECT",VERTEX,{"disambiguationData":[OD(0.0)],"derivedFrom":[subQ1,subQ0]}),-1.0]])],"derivedFrom":subQ1})])],"isStart":false});}
            var Q2;
            {var subQ0=sQuery(id+"F0.wireOp",EDGE,"E13");var subQ1=makeQuery(id+"F0.imprint","INTERSECT",VERTEX,{"disambiguationData":[OD(0.0)],"derivedFrom":[sQuery(id+"F0.wireOp",EDGE,"E2"),subQ0]});Q2=makeQuery(id+"F1.opExtrude","CAP_EDGE",EDGE,{"disambiguationData":[OSD([subQ0]),TDD([makeQuery(id+"F0.imprint","IMPRINT",EDGE,{"disambiguationData":[TD([[subQ1,1.0]])],"derivedFrom":subQ0}),makeQuery(id+"F0.imprint","IMPRINT",EDGE,{"disambiguationData":[TD([[makeQuery(id+"F0.imprint","INTERSECT",VERTEX,{"disambiguationData":[OD(1.0)],"derivedFrom":[sQuery(id+"F0.wireOp",EDGE,"E10"),subQ0]}),1.0]])],"derivedFrom":subQ0})])],"isStart":false});}
            var Q3;
            {var subQ0=sQuery(id+"F0.wireOp",EDGE,"E13");var subQ1=sQuery(id+"F0.wireOp",EDGE,"E11");Q3=makeQuery(id+"F1.opExtrude","CAP_EDGE",EDGE,{"disambiguationData":[OSD([subQ1]),TDD([makeQuery(id+"F0.imprint","IMPRINT",EDGE,{"disambiguationData":[TD([[makeQuery(id+"F0.imprint","INTERSECT",VERTEX,{"disambiguationData":[OD(0.0)],"derivedFrom":[subQ1,subQ0]}),1.0]])],"derivedFrom":subQ1})])],"isStart":false});}
            var Q4;
            {var subQ0=sQuery(id+"F0.wireOp",EDGE,"E13");var subQ1=makeQuery(id+"F0.imprint","INTERSECT",VERTEX,{"disambiguationData":[OD(1.0)],"derivedFrom":[sQuery(id+"F0.wireOp",EDGE,"E2"),subQ0]});Q4=makeQuery(id+"F1.opExtrude","CAP_EDGE",EDGE,{"disambiguationData":[OSD([subQ0]),TDD([makeQuery(id+"F0.imprint","IMPRINT",EDGE,{"disambiguationData":[TD([[makeQuery(id+"F0.imprint","INTERSECT",VERTEX,{"disambiguationData":[OD(0.0)],"derivedFrom":[sQuery(id+"F0.wireOp",EDGE,"E10"),subQ0]}),-1.0]])],"derivedFrom":subQ0}),makeQuery(id+"F0.imprint","IMPRINT",EDGE,{"disambiguationData":[TD([[subQ1,-1.0]])],"derivedFrom":subQ0})])],"isStart":false});}
            var Q5;
            {var subQ0=sQuery(id+"F0.wireOp",EDGE,"E12");var subQ1=makeQuery(id+"F0.imprint","INTERSECT",VERTEX,{"disambiguationData":[OD(1.0)],"derivedFrom":[sQuery(id+"F0.wireOp",EDGE,"E2"),subQ0]});Q5=makeQuery(id+"F1.opExtrude","CAP_EDGE",EDGE,{"disambiguationData":[OSD([subQ0]),TDD([makeQuery(id+"F0.imprint","IMPRINT",EDGE,{"disambiguationData":[TD([[makeQuery(id+"F0.imprint","INTERSECT",VERTEX,{"disambiguationData":[OD(0.0)],"derivedFrom":[sQuery(id+"F0.wireOp",EDGE,"E10"),subQ0]}),-1.0]])],"derivedFrom":subQ0}),makeQuery(id+"F0.imprint","IMPRINT",EDGE,{"disambiguationData":[TD([[subQ1,-1.0]])],"derivedFrom":subQ0})])],"isStart":false});}
            var Q6;
            {var subQ0=sQuery(id+"F0.wireOp",EDGE,"E12");var subQ1=sQuery(id+"F0.wireOp",EDGE,"E11");Q6=makeQuery(id+"F1.opExtrude","CAP_EDGE",EDGE,{"disambiguationData":[OSD([subQ1]),TDD([makeQuery(id+"F0.imprint","IMPRINT",EDGE,{"disambiguationData":[TD([[makeQuery(id+"F0.imprint","INTERSECT",VERTEX,{"disambiguationData":[OD(0.0)],"derivedFrom":[subQ1,subQ0]}),-1.0]])],"derivedFrom":subQ1})])],"isStart":false});}
            var Q7;
            {var subQ0=sQuery(id+"F0.wireOp",EDGE,"E12");var subQ1=makeQuery(id+"F0.imprint","INTERSECT",VERTEX,{"disambiguationData":[OD(0.0)],"derivedFrom":[sQuery(id+"F0.wireOp",EDGE,"E2"),subQ0]});Q7=makeQuery(id+"F1.opExtrude","CAP_EDGE",EDGE,{"disambiguationData":[OSD([subQ0]),TDD([makeQuery(id+"F0.imprint","IMPRINT",EDGE,{"disambiguationData":[TD([[subQ1,1.0]])],"derivedFrom":subQ0}),makeQuery(id+"F0.imprint","IMPRINT",EDGE,{"disambiguationData":[TD([[makeQuery(id+"F0.imprint","INTERSECT",VERTEX,{"disambiguationData":[OD(1.0)],"derivedFrom":[sQuery(id+"F0.wireOp",EDGE,"E10"),subQ0]}),1.0]])],"derivedFrom":subQ0})])],"isStart":false});}
            var Q8;
            Q8=makeQuery(id+"F31.opExtrude","CAP_EDGE",EDGE,{"disambiguationData":[OSD([sQuery(id+"F30.wireOp",EDGE,"E148")])],"isStart":true});
            var Q9;
            Q9=makeQuery(id+"F31.opExtrude","CAP_EDGE",EDGE,{"disambiguationData":[OSD([sQuery(id+"F30.wireOp",EDGE,"E146")])],"isStart":true});
            var Q10;
            Q10=makeQuery(id+"F31.opExtrude","CAP_EDGE",EDGE,{"disambiguationData":[OSD([sQuery(id+"F30.wireOp",EDGE,"E149")])],"isStart":true});
            var Q11;
            Q11=makeQuery(id+"F31.opExtrude","CAP_EDGE",EDGE,{"disambiguationData":[OSD([sQuery(id+"F30.wireOp",EDGE,"E151")])],"isStart":true});
            var Q12;
            {var subQ1=sQuery(id+"F0.wireOp",EDGE,"E0");var subQ3=sQuery(id+"F30.wireOp",EDGE,"E148");Q12=makeQuery(id+"F31.boolean.opBoolean","SPLIT",EDGE,{"disambiguationData":[TD([makeQuery(id+"F31.opExtrude","SWEPT_FACE",FACE,{"disambiguationData":[OSD([subQ3])]})])],"derivedFrom":makeQuery(id+"F1.opExtrude","CAP_EDGE",EDGE,{"disambiguationData":[OSD([subQ1])],"isStart":false})});}
            var Q13;
            {var subQ1=sQuery(id+"F0.wireOp",EDGE,"E0");var subQ2=sQuery(id+"F30.wireOp",EDGE,"E146");Q13=makeQuery(id+"F31.boolean.opBoolean","SPLIT",EDGE,{"disambiguationData":[TD([makeQuery(id+"F31.opExtrude","SWEPT_FACE",FACE,{"disambiguationData":[OSD([subQ2])]})])],"derivedFrom":makeQuery(id+"F1.opExtrude","CAP_EDGE",EDGE,{"disambiguationData":[OSD([subQ1])],"isStart":false})});}
            chamfer(context, id + "F33", {"entities" : qUnion([Q0, Q1, Q2, Q3, Q4, Q5, Q6, Q7, Q8, Q9, Q10, Q11, Q12, Q13]), "chamferType" : ChamferType.TWO_OFFSETS, "width1" : 1 * mm, "oppositeDirection" : false, "width2" : .5 * mm, "tangentPropagation" : true});
        }
        {
            var Q0;
            Q0=makeQuery(id+"F31.opExtrude","SWEPT_FACE",FACE,{"disambiguationData":[OSD([sQuery(id+"F30.wireOp",EDGE,"E147")])]});
            var Q1;
            Q1=makeQuery(id+"F31.opExtrude","SWEPT_FACE",FACE,{"disambiguationData":[OSD([sQuery(id+"F30.wireOp",EDGE,"E150")])]});
            fillet(context, id + "F34", {"entities" : qUnion([Q0, Q1]), "radius" : .5 * mm, "tangentPropagation" : true, "allowEdgeOverflow" : false});
        }
        {
            var Q0;
            Q0=makeQuery(id+"F31.opExtrude","SWEPT_FACE",FACE,{"disambiguationData":[OSD([sQuery(id+"F30.wireOp",EDGE,"E147")])]});
            var sketch = newSketch(context, id + "F35", { "sketchPlane" : qUnion([Q0])});
            skLineSegment(sketch, "E153", {"start": v(0, 0) * mm, "end": v(0, -1.5) * mm});
            skLineSegment(sketch, "E154", {"start": v(0, -1.5) * mm, "end": v(-1.25, -1.5) * mm});
            skLineSegment(sketch, "E155", {"start": v(-1.25, -1.5) * mm, "end": v(0, 0) * mm});
            skLineSegment(sketch, "E156", {"start": v(0, -1.5) * mm, "end": v(1.25, -1.5) * mm});
            skLineSegment(sketch, "E157", {"start": v(1.25, -1.5) * mm, "end": v(0, 0) * mm});
            skSolve(sketch);
        }
        {
            var Q0;
            Q0=makeQuery(id+"F35.imprint","IMPRINT",FACE,{"disambiguationData":[TD([[makeQuery(id+"F35.imprint","IMPRINT",EDGE,{"derivedFrom":sQuery(id+"F35.wireOp",EDGE,"E153")}),-1.0]])]});
            var Q1;
            Q1=makeQuery(id+"F35.imprint","IMPRINT",FACE,{"disambiguationData":[TD([[makeQuery(id+"F35.imprint","IMPRINT",EDGE,{"derivedFrom":sQuery(id+"F35.wireOp",EDGE,"E153")}),1.0]])]});
            extrude(context, id + "F36", {"entities" : qUnion([Q0, Q1]), "operationType" : NewBodyOperationType.REMOVE, "oppositeDirection" : true, "depth" : 5 * mm, "offsetDistance" : 25 * mm});
        }
        {
            var Q0;
            Q0=makeQuery(id+"F31.opExtrude","SWEPT_FACE",FACE,{"disambiguationData":[OSD([sQuery(id+"F30.wireOp",EDGE,"E150")])]});
            var sketch = newSketch(context, id + "F37", { "sketchPlane" : qUnion([Q0])});
            skLineSegment(sketch, "E158", {"start": v(0, 0) * mm, "end": v(0, -1.5) * mm});
            skLineSegment(sketch, "E159", {"start": v(0, -1.5) * mm, "end": v(-1.25, -1.5) * mm});
            skLineSegment(sketch, "E160", {"start": v(-1.25, -1.5) * mm, "end": v(0, 0) * mm});
            skLineSegment(sketch, "E161", {"start": v(0, -1.5) * mm, "end": v(1.25, -1.5) * mm});
            skLineSegment(sketch, "E162", {"start": v(1.25, -1.5) * mm, "end": v(0, 0) * mm});
            skSolve(sketch);
        }
        {
            var Q0;
            Q0 = qSketchRegion(id + "F37", true);
            extrude(context, id + "F38", {"entities" : qUnion([Q0]), "operationType" : NewBodyOperationType.REMOVE, "oppositeDirection" : true, "depth" : 5 * mm, "offsetDistance" : 25 * mm});
        }
    });
